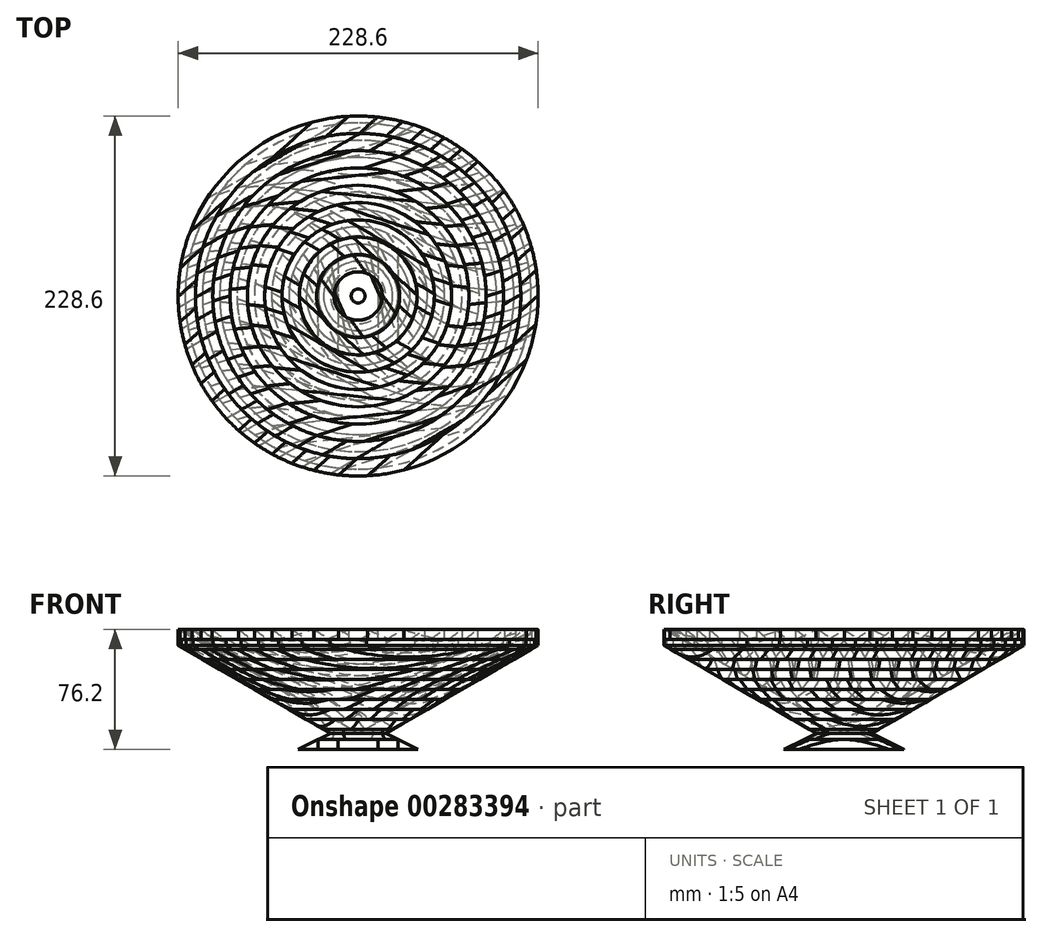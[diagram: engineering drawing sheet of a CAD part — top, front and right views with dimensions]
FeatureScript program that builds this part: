
annotation { "Feature Type Name" : "Feature", "Feature Type Description" : "" }
export const myFeature = defineFeature(function(context is Context, id is Id, definition is map)
    precondition{}
    {
        {
            var Q0;
            Q0=qCreatedBy(makeId("Top.planeOp"),FACE);
            var sketch = newSketch(context, id + "F0", { "sketchPlane" : qUnion([Q0])});
            skLineSegment(sketch, "E0.bottom", {"start": v(114.3, -114.3) * mm, "end": v(-114.3, -114.3) * mm});
            skLineSegment(sketch, "E0.top", {"start": v(114.3, 114.3) * mm, "end": v(-114.3, 114.3) * mm});
            skLineSegment(sketch, "E0.left", {"start": v(114.3, -114.3) * mm, "end": v(114.3, 114.3) * mm});
            skLineSegment(sketch, "E0.right", {"start": v(-114.3, -114.3) * mm, "end": v(-114.3, 114.3) * mm});
            skPoint(sketch, "E0.middle", {"position": v(0, 0) * mm});
            skLineSegment(sketch, "E1.bottom", {"start": v(-12.7, 114.3) * mm, "end": v(12.7, 114.3) * mm});
            skLineSegment(sketch, "E1.top", {"start": v(-12.7, -114.3) * mm, "end": v(12.7, -114.3) * mm});
            skLineSegment(sketch, "E1.left", {"start": v(-12.7, 114.3) * mm, "end": v(-12.7, -114.3) * mm});
            skLineSegment(sketch, "E1.right", {"start": v(12.7, 114.3) * mm, "end": v(12.7, -114.3) * mm});
            skLineSegment(sketch, "E2.bottom", {"start": v(-25.4, 114.3) * mm, "end": v(25.4, 114.3) * mm});
            skLineSegment(sketch, "E2.top", {"start": v(-25.4, -114.3) * mm, "end": v(25.4, -114.3) * mm});
            skLineSegment(sketch, "E2.left", {"start": v(-25.4, 114.3) * mm, "end": v(-25.4, -114.3) * mm});
            skLineSegment(sketch, "E2.right", {"start": v(25.4, 114.3) * mm, "end": v(25.4, -114.3) * mm});
            skLineSegment(sketch, "E3.bottom", {"start": v(-38.1, 114.3) * mm, "end": v(38.1, 114.3) * mm});
            skLineSegment(sketch, "E3.top", {"start": v(-38.1, -114.3) * mm, "end": v(38.1, -114.3) * mm});
            skLineSegment(sketch, "E3.left", {"start": v(-38.1, 114.3) * mm, "end": v(-38.1, -114.3) * mm});
            skLineSegment(sketch, "E3.right", {"start": v(38.1, 114.3) * mm, "end": v(38.1, -114.3) * mm});
            skLineSegment(sketch, "E4.bottom", {"start": v(-50.8, 114.3) * mm, "end": v(50.8, 114.3) * mm});
            skLineSegment(sketch, "E4.top", {"start": v(-50.8, -114.3) * mm, "end": v(50.8, -114.3) * mm});
            skLineSegment(sketch, "E4.left", {"start": v(-50.8, 114.3) * mm, "end": v(-50.8, -114.3) * mm});
            skLineSegment(sketch, "E4.right", {"start": v(50.8, 114.3) * mm, "end": v(50.8, -114.3) * mm});
            skLineSegment(sketch, "E5.bottom", {"start": v(-63.5, 114.3) * mm, "end": v(63.5, 114.3) * mm});
            skLineSegment(sketch, "E5.top", {"start": v(-63.5, -114.3) * mm, "end": v(63.5, -114.3) * mm});
            skLineSegment(sketch, "E5.left", {"start": v(-63.5, 114.3) * mm, "end": v(-63.5, -114.3) * mm});
            skLineSegment(sketch, "E5.right", {"start": v(63.5, 114.3) * mm, "end": v(63.5, -114.3) * mm});
            skLineSegment(sketch, "E6.bottom", {"start": v(-76.2, 114.3) * mm, "end": v(76.2, 114.3) * mm});
            skLineSegment(sketch, "E6.top", {"start": v(-76.2, -114.3) * mm, "end": v(76.2, -114.3) * mm});
            skLineSegment(sketch, "E6.left", {"start": v(-76.2, 114.3) * mm, "end": v(-76.2, -114.3) * mm});
            skLineSegment(sketch, "E6.right", {"start": v(76.2, 114.3) * mm, "end": v(76.2, -114.3) * mm});
            skLineSegment(sketch, "E7.bottom", {"start": v(-88.9, 114.3) * mm, "end": v(88.9, 114.3) * mm});
            skLineSegment(sketch, "E7.top", {"start": v(-88.9, -114.3) * mm, "end": v(88.9, -114.3) * mm});
            skLineSegment(sketch, "E7.left", {"start": v(-88.9, 114.3) * mm, "end": v(-88.9, -114.3) * mm});
            skLineSegment(sketch, "E7.right", {"start": v(88.9, 114.3) * mm, "end": v(88.9, -114.3) * mm});
            skLineSegment(sketch, "E8.bottom", {"start": v(-101.6, 114.3) * mm, "end": v(101.6, 114.3) * mm});
            skLineSegment(sketch, "E8.top", {"start": v(-101.6, -114.3) * mm, "end": v(101.6, -114.3) * mm});
            skLineSegment(sketch, "E8.left", {"start": v(-101.6, 114.3) * mm, "end": v(-101.6, -114.3) * mm});
            skLineSegment(sketch, "E8.right", {"start": v(101.6, 114.3) * mm, "end": v(101.6, -114.3) * mm});
            skSolve(sketch);
        }
        {
            var Q0;
            {var subQ0=sQuery(id+"F0.wireOp",EDGE,"E0.right");Q0=makeQuery(id+"F0.imprint","IMPRINT",FACE,{"disambiguationData":[TD([[makeQuery(id+"F0.imprint","IMPRINT",EDGE,{"derivedFrom":subQ0}),-1.0]])]});}
            var Q1;
            {var subQ0=sQuery(id+"F0.wireOp",EDGE,"E6.left");Q1=makeQuery(id+"F0.imprint","IMPRINT",FACE,{"disambiguationData":[TD([[makeQuery(id+"F0.imprint","IMPRINT",EDGE,{"derivedFrom":subQ0}),-1.0]])]});}
            var Q2;
            {var subQ0=sQuery(id+"F0.wireOp",EDGE,"E4.left");Q2=makeQuery(id+"F0.imprint","IMPRINT",FACE,{"disambiguationData":[TD([[makeQuery(id+"F0.imprint","IMPRINT",EDGE,{"derivedFrom":subQ0}),-1.0]])]});}
            var Q3;
            {var subQ0=sQuery(id+"F0.wireOp",EDGE,"E2.left");Q3=makeQuery(id+"F0.imprint","IMPRINT",FACE,{"disambiguationData":[TD([[makeQuery(id+"F0.imprint","IMPRINT",EDGE,{"derivedFrom":subQ0}),-1.0]])]});}
            var Q4;
            {var subQ0=sQuery(id+"F0.wireOp",EDGE,"E1.left");Q4=makeQuery(id+"F0.imprint","IMPRINT",FACE,{"disambiguationData":[TD([[makeQuery(id+"F0.imprint","IMPRINT",EDGE,{"derivedFrom":subQ0}),1.0]])]});}
            var Q5;
            {var subQ0=sQuery(id+"F0.wireOp",EDGE,"E2.right");Q5=makeQuery(id+"F0.imprint","IMPRINT",FACE,{"disambiguationData":[TD([[makeQuery(id+"F0.imprint","IMPRINT",EDGE,{"derivedFrom":subQ0}),1.0]])]});}
            var Q6;
            {var subQ0=sQuery(id+"F0.wireOp",EDGE,"E4.right");Q6=makeQuery(id+"F0.imprint","IMPRINT",FACE,{"disambiguationData":[TD([[makeQuery(id+"F0.imprint","IMPRINT",EDGE,{"derivedFrom":subQ0}),1.0]])]});}
            var Q7;
            {var subQ0=sQuery(id+"F0.wireOp",EDGE,"E6.right");Q7=makeQuery(id+"F0.imprint","IMPRINT",FACE,{"disambiguationData":[TD([[makeQuery(id+"F0.imprint","IMPRINT",EDGE,{"derivedFrom":subQ0}),1.0]])]});}
            var Q8;
            {var subQ0=sQuery(id+"F0.wireOp",EDGE,"E0.left");Q8=makeQuery(id+"F0.imprint","IMPRINT",FACE,{"disambiguationData":[TD([[makeQuery(id+"F0.imprint","IMPRINT",EDGE,{"derivedFrom":subQ0}),1.0]])]});}
            extrude(context, id + "F1", {"entities" : qUnion([Q0, Q1, Q2, Q3, Q4, Q5, Q6, Q7, Q8]), "depth" : 6.35 * mm});
        }
        {
            var Q0;
            {var subQ0=sQuery(id+"F0.wireOp",EDGE,"E7.right");Q0=makeQuery(id+"F0.imprint","IMPRINT",FACE,{"disambiguationData":[TD([[makeQuery(id+"F0.imprint","IMPRINT",EDGE,{"derivedFrom":subQ0}),1.0]])]});}
            var Q1;
            {var subQ0=sQuery(id+"F0.wireOp",EDGE,"E5.right");Q1=makeQuery(id+"F0.imprint","IMPRINT",FACE,{"disambiguationData":[TD([[makeQuery(id+"F0.imprint","IMPRINT",EDGE,{"derivedFrom":subQ0}),1.0]])]});}
            var Q2;
            {var subQ0=sQuery(id+"F0.wireOp",EDGE,"E3.right");Q2=makeQuery(id+"F0.imprint","IMPRINT",FACE,{"disambiguationData":[TD([[makeQuery(id+"F0.imprint","IMPRINT",EDGE,{"derivedFrom":subQ0}),1.0]])]});}
            var Q3;
            {var subQ0=sQuery(id+"F0.wireOp",EDGE,"E1.right");Q3=makeQuery(id+"F0.imprint","IMPRINT",FACE,{"disambiguationData":[TD([[makeQuery(id+"F0.imprint","IMPRINT",EDGE,{"derivedFrom":subQ0}),1.0]])]});}
            var Q4;
            {var subQ0=sQuery(id+"F0.wireOp",EDGE,"E1.left");Q4=makeQuery(id+"F0.imprint","IMPRINT",FACE,{"disambiguationData":[TD([[makeQuery(id+"F0.imprint","IMPRINT",EDGE,{"derivedFrom":subQ0}),-1.0]])]});}
            var Q5;
            {var subQ0=sQuery(id+"F0.wireOp",EDGE,"E3.left");Q5=makeQuery(id+"F0.imprint","IMPRINT",FACE,{"disambiguationData":[TD([[makeQuery(id+"F0.imprint","IMPRINT",EDGE,{"derivedFrom":subQ0}),-1.0]])]});}
            var Q6;
            {var subQ0=sQuery(id+"F0.wireOp",EDGE,"E5.left");Q6=makeQuery(id+"F0.imprint","IMPRINT",FACE,{"disambiguationData":[TD([[makeQuery(id+"F0.imprint","IMPRINT",EDGE,{"derivedFrom":subQ0}),-1.0]])]});}
            var Q7;
            {var subQ0=sQuery(id+"F0.wireOp",EDGE,"E7.left");Q7=makeQuery(id+"F0.imprint","IMPRINT",FACE,{"disambiguationData":[TD([[makeQuery(id+"F0.imprint","IMPRINT",EDGE,{"derivedFrom":subQ0}),-1.0]])]});}
            extrude(context, id + "F2", {"entities" : qUnion([Q0, Q1, Q2, Q3, Q4, Q5, Q6, Q7]), "depth" : 6.35 * mm});
        }
        {
            var Q0;
            Q0=makeQuery(id+"F2.opExtrude","SWEPT_BODY",BODY,{"disambiguationData":[OSD([sQuery(id+"F0.wireOp",EDGE,"E1.left"),sQuery(id+"F0.wireOp",EDGE,"E2.left"),sQuery(id+"F0.wireOp",EDGE,"E8.bottom"),sQuery(id+"F0.wireOp",EDGE,"E8.top")])]});
            var Q1;
            Q1=makeQuery(id+"F2.opExtrude","SWEPT_BODY",BODY,{"disambiguationData":[OSD([sQuery(id+"F0.wireOp",EDGE,"E1.right"),sQuery(id+"F0.wireOp",EDGE,"E2.right"),sQuery(id+"F0.wireOp",EDGE,"E8.bottom"),sQuery(id+"F0.wireOp",EDGE,"E8.top")])]});
            var Q2;
            Q2=makeQuery(id+"F2.opExtrude","SWEPT_BODY",BODY,{"disambiguationData":[OSD([sQuery(id+"F0.wireOp",EDGE,"E3.right"),sQuery(id+"F0.wireOp",EDGE,"E4.right"),sQuery(id+"F0.wireOp",EDGE,"E8.bottom"),sQuery(id+"F0.wireOp",EDGE,"E8.top")])]});
            var Q3;
            Q3=makeQuery(id+"F2.opExtrude","SWEPT_BODY",BODY,{"disambiguationData":[OSD([sQuery(id+"F0.wireOp",EDGE,"E5.right"),sQuery(id+"F0.wireOp",EDGE,"E6.right"),sQuery(id+"F0.wireOp",EDGE,"E8.bottom"),sQuery(id+"F0.wireOp",EDGE,"E8.top")])]});
            var Q4;
            Q4=makeQuery(id+"F2.opExtrude","SWEPT_BODY",BODY,{"disambiguationData":[OSD([sQuery(id+"F0.wireOp",EDGE,"E3.left"),sQuery(id+"F0.wireOp",EDGE,"E4.left"),sQuery(id+"F0.wireOp",EDGE,"E8.bottom"),sQuery(id+"F0.wireOp",EDGE,"E8.top")])]});
            var Q5;
            Q5=makeQuery(id+"F1.opExtrude","SWEPT_BODY",BODY,{"disambiguationData":[OSD([sQuery(id+"F0.wireOp",EDGE,"E6.right"),sQuery(id+"F0.wireOp",EDGE,"E7.right"),sQuery(id+"F0.wireOp",EDGE,"E8.bottom"),sQuery(id+"F0.wireOp",EDGE,"E8.top")])]});
            var Q6;
            Q6=makeQuery(id+"F1.opExtrude","SWEPT_BODY",BODY,{"disambiguationData":[OSD([sQuery(id+"F0.wireOp",EDGE,"E6.left"),sQuery(id+"F0.wireOp",EDGE,"E7.left"),sQuery(id+"F0.wireOp",EDGE,"E8.bottom"),sQuery(id+"F0.wireOp",EDGE,"E8.top")])]});
            var Q7;
            Q7=makeQuery(id+"F1.opExtrude","SWEPT_BODY",BODY,{"disambiguationData":[OSD([sQuery(id+"F0.wireOp",EDGE,"E4.right"),sQuery(id+"F0.wireOp",EDGE,"E5.right"),sQuery(id+"F0.wireOp",EDGE,"E8.bottom"),sQuery(id+"F0.wireOp",EDGE,"E8.top")])]});
            var Q8;
            Q8=makeQuery(id+"F1.opExtrude","SWEPT_BODY",BODY,{"disambiguationData":[OSD([sQuery(id+"F0.wireOp",EDGE,"E4.left"),sQuery(id+"F0.wireOp",EDGE,"E5.left"),sQuery(id+"F0.wireOp",EDGE,"E8.bottom"),sQuery(id+"F0.wireOp",EDGE,"E8.top")])]});
            var Q9;
            Q9=makeQuery(id+"F1.opExtrude","SWEPT_BODY",BODY,{"disambiguationData":[OSD([sQuery(id+"F0.wireOp",EDGE,"E2.right"),sQuery(id+"F0.wireOp",EDGE,"E3.right"),sQuery(id+"F0.wireOp",EDGE,"E8.bottom"),sQuery(id+"F0.wireOp",EDGE,"E8.top")])]});
            var Q10;
            Q10=makeQuery(id+"F1.opExtrude","SWEPT_BODY",BODY,{"disambiguationData":[OSD([sQuery(id+"F0.wireOp",EDGE,"E2.left"),sQuery(id+"F0.wireOp",EDGE,"E3.left"),sQuery(id+"F0.wireOp",EDGE,"E8.bottom"),sQuery(id+"F0.wireOp",EDGE,"E8.top")])]});
            var Q11;
            Q11=makeQuery(id+"F1.opExtrude","SWEPT_BODY",BODY,{"disambiguationData":[OSD([sQuery(id+"F0.wireOp",EDGE,"E0.bottom"),sQuery(id+"F0.wireOp",EDGE,"E0.top"),sQuery(id+"F0.wireOp",EDGE,"E0.right"),sQuery(id+"F0.wireOp",EDGE,"E8.left")])]});
            var Q12;
            Q12=makeQuery(id+"F1.opExtrude","SWEPT_BODY",BODY,{"disambiguationData":[OSD([sQuery(id+"F0.wireOp",EDGE,"E1.left"),sQuery(id+"F0.wireOp",EDGE,"E1.right"),sQuery(id+"F0.wireOp",EDGE,"E8.bottom"),sQuery(id+"F0.wireOp",EDGE,"E8.top")])]});
            var Q13;
            Q13=makeQuery(id+"F2.opExtrude","SWEPT_BODY",BODY,{"disambiguationData":[OSD([sQuery(id+"F0.wireOp",EDGE,"E5.left"),sQuery(id+"F0.wireOp",EDGE,"E6.left"),sQuery(id+"F0.wireOp",EDGE,"E8.bottom"),sQuery(id+"F0.wireOp",EDGE,"E8.top")])]});
            var Q14;
            Q14=makeQuery(id+"F1.opExtrude","SWEPT_BODY",BODY,{"disambiguationData":[OSD([sQuery(id+"F0.wireOp",EDGE,"E0.bottom"),sQuery(id+"F0.wireOp",EDGE,"E0.top"),sQuery(id+"F0.wireOp",EDGE,"E0.left"),sQuery(id+"F0.wireOp",EDGE,"E8.right")])]});
            var Q15;
            Q15=makeQuery(id+"F2.opExtrude","SWEPT_BODY",BODY,{"disambiguationData":[OSD([sQuery(id+"F0.wireOp",EDGE,"E7.right"),sQuery(id+"F0.wireOp",EDGE,"E8.bottom"),sQuery(id+"F0.wireOp",EDGE,"E8.top"),sQuery(id+"F0.wireOp",EDGE,"E8.right")])]});
            var Q16;
            Q16=makeQuery(id+"F2.opExtrude","SWEPT_BODY",BODY,{"disambiguationData":[OSD([sQuery(id+"F0.wireOp",EDGE,"E7.left"),sQuery(id+"F0.wireOp",EDGE,"E8.bottom"),sQuery(id+"F0.wireOp",EDGE,"E8.top"),sQuery(id+"F0.wireOp",EDGE,"E8.left")])]});
            transform(context, id + "F3", {"entities" : qUnion([Q0, Q1, Q2, Q3, Q4, Q5, Q6, Q7, Q8, Q9, Q10, Q11, Q12, Q13, Q14, Q15, Q16]), "transformType" : TransformType.TRANSLATION_3D, "dx" : 0 * mm, "dy" : 0 * mm, "dz" : 6.35 * mm, "makeCopy" : true});
        }
        {
            var Q0;
            Q0=qCreatedBy(makeId("Front.planeOp"),FACE);
            var sketch = newSketch(context, id + "F4", { "sketchPlane" : qUnion([Q0])});
            skLineSegment(sketch, "E9", {"start": v(0, 0) * mm, "end": v(0, 114.3) * mm, "construction": true});
            skSolve(sketch);
        }
        {
            var Q0;
            Q0=makeQuery(id+"F3.opPattern","COPY",BODY,{"derivedFrom":makeQuery(id+"F1.opExtrude","SWEPT_BODY",BODY,{"disambiguationData":[OSD([sQuery(id+"F0.wireOp",EDGE,"E0.bottom"),sQuery(id+"F0.wireOp",EDGE,"E0.top"),sQuery(id+"F0.wireOp",EDGE,"E0.right"),sQuery(id+"F0.wireOp",EDGE,"E8.left")])]}),"instanceName":"1"});
            var Q1;
            Q1=makeQuery(id+"F3.opPattern","COPY",BODY,{"derivedFrom":makeQuery(id+"F2.opExtrude","SWEPT_BODY",BODY,{"disambiguationData":[OSD([sQuery(id+"F0.wireOp",EDGE,"E7.left"),sQuery(id+"F0.wireOp",EDGE,"E8.bottom"),sQuery(id+"F0.wireOp",EDGE,"E8.top"),sQuery(id+"F0.wireOp",EDGE,"E8.left")])]}),"instanceName":"1"});
            var Q2;
            Q2=makeQuery(id+"F3.opPattern","COPY",BODY,{"derivedFrom":makeQuery(id+"F1.opExtrude","SWEPT_BODY",BODY,{"disambiguationData":[OSD([sQuery(id+"F0.wireOp",EDGE,"E6.left"),sQuery(id+"F0.wireOp",EDGE,"E7.left"),sQuery(id+"F0.wireOp",EDGE,"E8.bottom"),sQuery(id+"F0.wireOp",EDGE,"E8.top")])]}),"instanceName":"1"});
            var Q3;
            Q3=makeQuery(id+"F3.opPattern","COPY",BODY,{"derivedFrom":makeQuery(id+"F1.opExtrude","SWEPT_BODY",BODY,{"disambiguationData":[OSD([sQuery(id+"F0.wireOp",EDGE,"E4.left"),sQuery(id+"F0.wireOp",EDGE,"E5.left"),sQuery(id+"F0.wireOp",EDGE,"E8.bottom"),sQuery(id+"F0.wireOp",EDGE,"E8.top")])]}),"instanceName":"1"});
            var Q4;
            Q4=makeQuery(id+"F3.opPattern","COPY",BODY,{"derivedFrom":makeQuery(id+"F2.opExtrude","SWEPT_BODY",BODY,{"disambiguationData":[OSD([sQuery(id+"F0.wireOp",EDGE,"E5.left"),sQuery(id+"F0.wireOp",EDGE,"E6.left"),sQuery(id+"F0.wireOp",EDGE,"E8.bottom"),sQuery(id+"F0.wireOp",EDGE,"E8.top")])]}),"instanceName":"1"});
            var Q5;
            Q5=makeQuery(id+"F3.opPattern","COPY",BODY,{"derivedFrom":makeQuery(id+"F2.opExtrude","SWEPT_BODY",BODY,{"disambiguationData":[OSD([sQuery(id+"F0.wireOp",EDGE,"E3.left"),sQuery(id+"F0.wireOp",EDGE,"E4.left"),sQuery(id+"F0.wireOp",EDGE,"E8.bottom"),sQuery(id+"F0.wireOp",EDGE,"E8.top")])]}),"instanceName":"1"});
            var Q6;
            Q6=makeQuery(id+"F3.opPattern","COPY",BODY,{"derivedFrom":makeQuery(id+"F1.opExtrude","SWEPT_BODY",BODY,{"disambiguationData":[OSD([sQuery(id+"F0.wireOp",EDGE,"E2.left"),sQuery(id+"F0.wireOp",EDGE,"E3.left"),sQuery(id+"F0.wireOp",EDGE,"E8.bottom"),sQuery(id+"F0.wireOp",EDGE,"E8.top")])]}),"instanceName":"1"});
            var Q7;
            Q7=makeQuery(id+"F3.opPattern","COPY",BODY,{"derivedFrom":makeQuery(id+"F2.opExtrude","SWEPT_BODY",BODY,{"disambiguationData":[OSD([sQuery(id+"F0.wireOp",EDGE,"E1.left"),sQuery(id+"F0.wireOp",EDGE,"E2.left"),sQuery(id+"F0.wireOp",EDGE,"E8.bottom"),sQuery(id+"F0.wireOp",EDGE,"E8.top")])]}),"instanceName":"1"});
            var Q8;
            Q8=makeQuery(id+"F3.opPattern","COPY",BODY,{"derivedFrom":makeQuery(id+"F1.opExtrude","SWEPT_BODY",BODY,{"disambiguationData":[OSD([sQuery(id+"F0.wireOp",EDGE,"E1.left"),sQuery(id+"F0.wireOp",EDGE,"E1.right"),sQuery(id+"F0.wireOp",EDGE,"E8.bottom"),sQuery(id+"F0.wireOp",EDGE,"E8.top")])]}),"instanceName":"1"});
            var Q9;
            Q9=makeQuery(id+"F3.opPattern","COPY",BODY,{"derivedFrom":makeQuery(id+"F2.opExtrude","SWEPT_BODY",BODY,{"disambiguationData":[OSD([sQuery(id+"F0.wireOp",EDGE,"E1.right"),sQuery(id+"F0.wireOp",EDGE,"E2.right"),sQuery(id+"F0.wireOp",EDGE,"E8.bottom"),sQuery(id+"F0.wireOp",EDGE,"E8.top")])]}),"instanceName":"1"});
            var Q10;
            Q10=makeQuery(id+"F3.opPattern","COPY",BODY,{"derivedFrom":makeQuery(id+"F1.opExtrude","SWEPT_BODY",BODY,{"disambiguationData":[OSD([sQuery(id+"F0.wireOp",EDGE,"E2.right"),sQuery(id+"F0.wireOp",EDGE,"E3.right"),sQuery(id+"F0.wireOp",EDGE,"E8.bottom"),sQuery(id+"F0.wireOp",EDGE,"E8.top")])]}),"instanceName":"1"});
            var Q11;
            Q11=makeQuery(id+"F3.opPattern","COPY",BODY,{"derivedFrom":makeQuery(id+"F2.opExtrude","SWEPT_BODY",BODY,{"disambiguationData":[OSD([sQuery(id+"F0.wireOp",EDGE,"E3.right"),sQuery(id+"F0.wireOp",EDGE,"E4.right"),sQuery(id+"F0.wireOp",EDGE,"E8.bottom"),sQuery(id+"F0.wireOp",EDGE,"E8.top")])]}),"instanceName":"1"});
            var Q12;
            Q12=makeQuery(id+"F3.opPattern","COPY",BODY,{"derivedFrom":makeQuery(id+"F1.opExtrude","SWEPT_BODY",BODY,{"disambiguationData":[OSD([sQuery(id+"F0.wireOp",EDGE,"E4.right"),sQuery(id+"F0.wireOp",EDGE,"E5.right"),sQuery(id+"F0.wireOp",EDGE,"E8.bottom"),sQuery(id+"F0.wireOp",EDGE,"E8.top")])]}),"instanceName":"1"});
            var Q13;
            Q13=makeQuery(id+"F3.opPattern","COPY",BODY,{"derivedFrom":makeQuery(id+"F2.opExtrude","SWEPT_BODY",BODY,{"disambiguationData":[OSD([sQuery(id+"F0.wireOp",EDGE,"E5.right"),sQuery(id+"F0.wireOp",EDGE,"E6.right"),sQuery(id+"F0.wireOp",EDGE,"E8.bottom"),sQuery(id+"F0.wireOp",EDGE,"E8.top")])]}),"instanceName":"1"});
            var Q14;
            Q14=makeQuery(id+"F3.opPattern","COPY",BODY,{"derivedFrom":makeQuery(id+"F1.opExtrude","SWEPT_BODY",BODY,{"disambiguationData":[OSD([sQuery(id+"F0.wireOp",EDGE,"E6.right"),sQuery(id+"F0.wireOp",EDGE,"E7.right"),sQuery(id+"F0.wireOp",EDGE,"E8.bottom"),sQuery(id+"F0.wireOp",EDGE,"E8.top")])]}),"instanceName":"1"});
            var Q15;
            Q15=makeQuery(id+"F3.opPattern","COPY",BODY,{"derivedFrom":makeQuery(id+"F2.opExtrude","SWEPT_BODY",BODY,{"disambiguationData":[OSD([sQuery(id+"F0.wireOp",EDGE,"E7.right"),sQuery(id+"F0.wireOp",EDGE,"E8.bottom"),sQuery(id+"F0.wireOp",EDGE,"E8.top"),sQuery(id+"F0.wireOp",EDGE,"E8.right")])]}),"instanceName":"1"});
            var Q16;
            Q16=makeQuery(id+"F3.opPattern","COPY",BODY,{"derivedFrom":makeQuery(id+"F1.opExtrude","SWEPT_BODY",BODY,{"disambiguationData":[OSD([sQuery(id+"F0.wireOp",EDGE,"E0.bottom"),sQuery(id+"F0.wireOp",EDGE,"E0.top"),sQuery(id+"F0.wireOp",EDGE,"E0.left"),sQuery(id+"F0.wireOp",EDGE,"E8.right")])]}),"instanceName":"1"});
            var Q17;
            Q17=sQuery(id+"F4.wireOp",EDGE,"E9");
            transform(context, id + "F5", {"entities" : qUnion([Q0, Q1, Q2, Q3, Q4, Q5, Q6, Q7, Q8, Q9, Q10, Q11, Q12, Q13, Q14, Q15, Q16]), "transformType" : TransformType.ROTATION, "transformAxis" : qUnion([Q17]), "angle" : 12 * degree, "makeCopy" : false});
        }
        {
            var Q0;
            Q0=makeQuery(id+"F3.opPattern","COPY",BODY,{"derivedFrom":makeQuery(id+"F2.opExtrude","SWEPT_BODY",BODY,{"disambiguationData":[OSD([sQuery(id+"F0.wireOp",EDGE,"E1.right"),sQuery(id+"F0.wireOp",EDGE,"E2.right"),sQuery(id+"F0.wireOp",EDGE,"E8.bottom"),sQuery(id+"F0.wireOp",EDGE,"E8.top")])]}),"instanceName":"1"});
            var Q1;
            Q1=makeQuery(id+"F3.opPattern","COPY",BODY,{"derivedFrom":makeQuery(id+"F2.opExtrude","SWEPT_BODY",BODY,{"disambiguationData":[OSD([sQuery(id+"F0.wireOp",EDGE,"E3.left"),sQuery(id+"F0.wireOp",EDGE,"E4.left"),sQuery(id+"F0.wireOp",EDGE,"E8.bottom"),sQuery(id+"F0.wireOp",EDGE,"E8.top")])]}),"instanceName":"1"});
            var Q2;
            Q2=makeQuery(id+"F3.opPattern","COPY",BODY,{"derivedFrom":makeQuery(id+"F2.opExtrude","SWEPT_BODY",BODY,{"disambiguationData":[OSD([sQuery(id+"F0.wireOp",EDGE,"E3.right"),sQuery(id+"F0.wireOp",EDGE,"E4.right"),sQuery(id+"F0.wireOp",EDGE,"E8.bottom"),sQuery(id+"F0.wireOp",EDGE,"E8.top")])]}),"instanceName":"1"});
            var Q3;
            Q3=makeQuery(id+"F3.opPattern","COPY",BODY,{"derivedFrom":makeQuery(id+"F2.opExtrude","SWEPT_BODY",BODY,{"disambiguationData":[OSD([sQuery(id+"F0.wireOp",EDGE,"E5.left"),sQuery(id+"F0.wireOp",EDGE,"E6.left"),sQuery(id+"F0.wireOp",EDGE,"E8.bottom"),sQuery(id+"F0.wireOp",EDGE,"E8.top")])]}),"instanceName":"1"});
            var Q4;
            Q4=makeQuery(id+"F3.opPattern","COPY",BODY,{"derivedFrom":makeQuery(id+"F1.opExtrude","SWEPT_BODY",BODY,{"disambiguationData":[OSD([sQuery(id+"F0.wireOp",EDGE,"E6.right"),sQuery(id+"F0.wireOp",EDGE,"E7.right"),sQuery(id+"F0.wireOp",EDGE,"E8.bottom"),sQuery(id+"F0.wireOp",EDGE,"E8.top")])]}),"instanceName":"1"});
            var Q5;
            Q5=makeQuery(id+"F3.opPattern","COPY",BODY,{"derivedFrom":makeQuery(id+"F2.opExtrude","SWEPT_BODY",BODY,{"disambiguationData":[OSD([sQuery(id+"F0.wireOp",EDGE,"E1.left"),sQuery(id+"F0.wireOp",EDGE,"E2.left"),sQuery(id+"F0.wireOp",EDGE,"E8.bottom"),sQuery(id+"F0.wireOp",EDGE,"E8.top")])]}),"instanceName":"1"});
            var Q6;
            Q6=makeQuery(id+"F3.opPattern","COPY",BODY,{"derivedFrom":makeQuery(id+"F1.opExtrude","SWEPT_BODY",BODY,{"disambiguationData":[OSD([sQuery(id+"F0.wireOp",EDGE,"E4.right"),sQuery(id+"F0.wireOp",EDGE,"E5.right"),sQuery(id+"F0.wireOp",EDGE,"E8.bottom"),sQuery(id+"F0.wireOp",EDGE,"E8.top")])]}),"instanceName":"1"});
            var Q7;
            Q7=makeQuery(id+"F3.opPattern","COPY",BODY,{"derivedFrom":makeQuery(id+"F1.opExtrude","SWEPT_BODY",BODY,{"disambiguationData":[OSD([sQuery(id+"F0.wireOp",EDGE,"E6.left"),sQuery(id+"F0.wireOp",EDGE,"E7.left"),sQuery(id+"F0.wireOp",EDGE,"E8.bottom"),sQuery(id+"F0.wireOp",EDGE,"E8.top")])]}),"instanceName":"1"});
            var Q8;
            Q8=makeQuery(id+"F3.opPattern","COPY",BODY,{"derivedFrom":makeQuery(id+"F1.opExtrude","SWEPT_BODY",BODY,{"disambiguationData":[OSD([sQuery(id+"F0.wireOp",EDGE,"E4.left"),sQuery(id+"F0.wireOp",EDGE,"E5.left"),sQuery(id+"F0.wireOp",EDGE,"E8.bottom"),sQuery(id+"F0.wireOp",EDGE,"E8.top")])]}),"instanceName":"1"});
            var Q9;
            Q9=makeQuery(id+"F3.opPattern","COPY",BODY,{"derivedFrom":makeQuery(id+"F1.opExtrude","SWEPT_BODY",BODY,{"disambiguationData":[OSD([sQuery(id+"F0.wireOp",EDGE,"E2.right"),sQuery(id+"F0.wireOp",EDGE,"E3.right"),sQuery(id+"F0.wireOp",EDGE,"E8.bottom"),sQuery(id+"F0.wireOp",EDGE,"E8.top")])]}),"instanceName":"1"});
            var Q10;
            Q10=makeQuery(id+"F3.opPattern","COPY",BODY,{"derivedFrom":makeQuery(id+"F1.opExtrude","SWEPT_BODY",BODY,{"disambiguationData":[OSD([sQuery(id+"F0.wireOp",EDGE,"E2.left"),sQuery(id+"F0.wireOp",EDGE,"E3.left"),sQuery(id+"F0.wireOp",EDGE,"E8.bottom"),sQuery(id+"F0.wireOp",EDGE,"E8.top")])]}),"instanceName":"1"});
            var Q11;
            Q11=makeQuery(id+"F3.opPattern","COPY",BODY,{"derivedFrom":makeQuery(id+"F1.opExtrude","SWEPT_BODY",BODY,{"disambiguationData":[OSD([sQuery(id+"F0.wireOp",EDGE,"E1.left"),sQuery(id+"F0.wireOp",EDGE,"E1.right"),sQuery(id+"F0.wireOp",EDGE,"E8.bottom"),sQuery(id+"F0.wireOp",EDGE,"E8.top")])]}),"instanceName":"1"});
            var Q12;
            Q12=makeQuery(id+"F3.opPattern","COPY",BODY,{"derivedFrom":makeQuery(id+"F1.opExtrude","SWEPT_BODY",BODY,{"disambiguationData":[OSD([sQuery(id+"F0.wireOp",EDGE,"E0.bottom"),sQuery(id+"F0.wireOp",EDGE,"E0.top"),sQuery(id+"F0.wireOp",EDGE,"E0.right"),sQuery(id+"F0.wireOp",EDGE,"E8.left")])]}),"instanceName":"1"});
            var Q13;
            Q13=makeQuery(id+"F3.opPattern","COPY",BODY,{"derivedFrom":makeQuery(id+"F1.opExtrude","SWEPT_BODY",BODY,{"disambiguationData":[OSD([sQuery(id+"F0.wireOp",EDGE,"E0.bottom"),sQuery(id+"F0.wireOp",EDGE,"E0.top"),sQuery(id+"F0.wireOp",EDGE,"E0.left"),sQuery(id+"F0.wireOp",EDGE,"E8.right")])]}),"instanceName":"1"});
            var Q14;
            Q14=makeQuery(id+"F3.opPattern","COPY",BODY,{"derivedFrom":makeQuery(id+"F2.opExtrude","SWEPT_BODY",BODY,{"disambiguationData":[OSD([sQuery(id+"F0.wireOp",EDGE,"E5.right"),sQuery(id+"F0.wireOp",EDGE,"E6.right"),sQuery(id+"F0.wireOp",EDGE,"E8.bottom"),sQuery(id+"F0.wireOp",EDGE,"E8.top")])]}),"instanceName":"1"});
            var Q15;
            Q15=makeQuery(id+"F3.opPattern","COPY",BODY,{"derivedFrom":makeQuery(id+"F2.opExtrude","SWEPT_BODY",BODY,{"disambiguationData":[OSD([sQuery(id+"F0.wireOp",EDGE,"E7.left"),sQuery(id+"F0.wireOp",EDGE,"E8.bottom"),sQuery(id+"F0.wireOp",EDGE,"E8.top"),sQuery(id+"F0.wireOp",EDGE,"E8.left")])]}),"instanceName":"1"});
            var Q16;
            Q16=makeQuery(id+"F3.opPattern","COPY",BODY,{"derivedFrom":makeQuery(id+"F2.opExtrude","SWEPT_BODY",BODY,{"disambiguationData":[OSD([sQuery(id+"F0.wireOp",EDGE,"E7.right"),sQuery(id+"F0.wireOp",EDGE,"E8.bottom"),sQuery(id+"F0.wireOp",EDGE,"E8.top"),sQuery(id+"F0.wireOp",EDGE,"E8.right")])]}),"instanceName":"1"});
            var Q17;
            Q17=makeQuery(id+"F2.opExtrude","SWEPT_BODY",BODY,{"disambiguationData":[OSD([sQuery(id+"F0.wireOp",EDGE,"E1.left"),sQuery(id+"F0.wireOp",EDGE,"E2.left"),sQuery(id+"F0.wireOp",EDGE,"E8.bottom"),sQuery(id+"F0.wireOp",EDGE,"E8.top")])]});
            var Q18;
            Q18=makeQuery(id+"F2.opExtrude","SWEPT_BODY",BODY,{"disambiguationData":[OSD([sQuery(id+"F0.wireOp",EDGE,"E1.right"),sQuery(id+"F0.wireOp",EDGE,"E2.right"),sQuery(id+"F0.wireOp",EDGE,"E8.bottom"),sQuery(id+"F0.wireOp",EDGE,"E8.top")])]});
            var Q19;
            Q19=makeQuery(id+"F2.opExtrude","SWEPT_BODY",BODY,{"disambiguationData":[OSD([sQuery(id+"F0.wireOp",EDGE,"E3.right"),sQuery(id+"F0.wireOp",EDGE,"E4.right"),sQuery(id+"F0.wireOp",EDGE,"E8.bottom"),sQuery(id+"F0.wireOp",EDGE,"E8.top")])]});
            var Q20;
            Q20=makeQuery(id+"F2.opExtrude","SWEPT_BODY",BODY,{"disambiguationData":[OSD([sQuery(id+"F0.wireOp",EDGE,"E5.right"),sQuery(id+"F0.wireOp",EDGE,"E6.right"),sQuery(id+"F0.wireOp",EDGE,"E8.bottom"),sQuery(id+"F0.wireOp",EDGE,"E8.top")])]});
            var Q21;
            Q21=makeQuery(id+"F2.opExtrude","SWEPT_BODY",BODY,{"disambiguationData":[OSD([sQuery(id+"F0.wireOp",EDGE,"E3.left"),sQuery(id+"F0.wireOp",EDGE,"E4.left"),sQuery(id+"F0.wireOp",EDGE,"E8.bottom"),sQuery(id+"F0.wireOp",EDGE,"E8.top")])]});
            var Q22;
            Q22=makeQuery(id+"F1.opExtrude","SWEPT_BODY",BODY,{"disambiguationData":[OSD([sQuery(id+"F0.wireOp",EDGE,"E6.right"),sQuery(id+"F0.wireOp",EDGE,"E7.right"),sQuery(id+"F0.wireOp",EDGE,"E8.bottom"),sQuery(id+"F0.wireOp",EDGE,"E8.top")])]});
            var Q23;
            Q23=makeQuery(id+"F1.opExtrude","SWEPT_BODY",BODY,{"disambiguationData":[OSD([sQuery(id+"F0.wireOp",EDGE,"E6.left"),sQuery(id+"F0.wireOp",EDGE,"E7.left"),sQuery(id+"F0.wireOp",EDGE,"E8.bottom"),sQuery(id+"F0.wireOp",EDGE,"E8.top")])]});
            var Q24;
            Q24=makeQuery(id+"F1.opExtrude","SWEPT_BODY",BODY,{"disambiguationData":[OSD([sQuery(id+"F0.wireOp",EDGE,"E4.right"),sQuery(id+"F0.wireOp",EDGE,"E5.right"),sQuery(id+"F0.wireOp",EDGE,"E8.bottom"),sQuery(id+"F0.wireOp",EDGE,"E8.top")])]});
            var Q25;
            Q25=makeQuery(id+"F1.opExtrude","SWEPT_BODY",BODY,{"disambiguationData":[OSD([sQuery(id+"F0.wireOp",EDGE,"E4.left"),sQuery(id+"F0.wireOp",EDGE,"E5.left"),sQuery(id+"F0.wireOp",EDGE,"E8.bottom"),sQuery(id+"F0.wireOp",EDGE,"E8.top")])]});
            var Q26;
            Q26=makeQuery(id+"F1.opExtrude","SWEPT_BODY",BODY,{"disambiguationData":[OSD([sQuery(id+"F0.wireOp",EDGE,"E2.right"),sQuery(id+"F0.wireOp",EDGE,"E3.right"),sQuery(id+"F0.wireOp",EDGE,"E8.bottom"),sQuery(id+"F0.wireOp",EDGE,"E8.top")])]});
            var Q27;
            Q27=makeQuery(id+"F1.opExtrude","SWEPT_BODY",BODY,{"disambiguationData":[OSD([sQuery(id+"F0.wireOp",EDGE,"E2.left"),sQuery(id+"F0.wireOp",EDGE,"E3.left"),sQuery(id+"F0.wireOp",EDGE,"E8.bottom"),sQuery(id+"F0.wireOp",EDGE,"E8.top")])]});
            var Q28;
            Q28=makeQuery(id+"F1.opExtrude","SWEPT_BODY",BODY,{"disambiguationData":[OSD([sQuery(id+"F0.wireOp",EDGE,"E0.bottom"),sQuery(id+"F0.wireOp",EDGE,"E0.top"),sQuery(id+"F0.wireOp",EDGE,"E0.right"),sQuery(id+"F0.wireOp",EDGE,"E8.left")])]});
            var Q29;
            Q29=makeQuery(id+"F1.opExtrude","SWEPT_BODY",BODY,{"disambiguationData":[OSD([sQuery(id+"F0.wireOp",EDGE,"E1.left"),sQuery(id+"F0.wireOp",EDGE,"E1.right"),sQuery(id+"F0.wireOp",EDGE,"E8.bottom"),sQuery(id+"F0.wireOp",EDGE,"E8.top")])]});
            var Q30;
            Q30=makeQuery(id+"F2.opExtrude","SWEPT_BODY",BODY,{"disambiguationData":[OSD([sQuery(id+"F0.wireOp",EDGE,"E5.left"),sQuery(id+"F0.wireOp",EDGE,"E6.left"),sQuery(id+"F0.wireOp",EDGE,"E8.bottom"),sQuery(id+"F0.wireOp",EDGE,"E8.top")])]});
            var Q31;
            Q31=makeQuery(id+"F1.opExtrude","SWEPT_BODY",BODY,{"disambiguationData":[OSD([sQuery(id+"F0.wireOp",EDGE,"E0.bottom"),sQuery(id+"F0.wireOp",EDGE,"E0.top"),sQuery(id+"F0.wireOp",EDGE,"E0.left"),sQuery(id+"F0.wireOp",EDGE,"E8.right")])]});
            var Q32;
            Q32=makeQuery(id+"F2.opExtrude","SWEPT_BODY",BODY,{"disambiguationData":[OSD([sQuery(id+"F0.wireOp",EDGE,"E7.right"),sQuery(id+"F0.wireOp",EDGE,"E8.bottom"),sQuery(id+"F0.wireOp",EDGE,"E8.top"),sQuery(id+"F0.wireOp",EDGE,"E8.right")])]});
            var Q33;
            Q33=makeQuery(id+"F2.opExtrude","SWEPT_BODY",BODY,{"disambiguationData":[OSD([sQuery(id+"F0.wireOp",EDGE,"E7.left"),sQuery(id+"F0.wireOp",EDGE,"E8.bottom"),sQuery(id+"F0.wireOp",EDGE,"E8.top"),sQuery(id+"F0.wireOp",EDGE,"E8.left")])]});
            transform(context, id + "F6", {"entities" : qUnion([Q0, Q1, Q2, Q3, Q4, Q5, Q6, Q7, Q8, Q9, Q10, Q11, Q12, Q13, Q14, Q15, Q16, Q17, Q18, Q19, Q20, Q21, Q22, Q23, Q24, Q25, Q26, Q27, Q28, Q29, Q30, Q31, Q32, Q33]), "transformType" : TransformType.TRANSLATION_3D, "dx" : 0 * mm, "dy" : 0 * mm, "dz" : 12.7 * mm, "makeCopy" : true});
        }
        {
            var Q0;
            Q0=makeQuery(id+"F6.opPattern","COPY",BODY,{"derivedFrom":makeQuery(id+"F3.opPattern","COPY",BODY,{"derivedFrom":makeQuery(id+"F2.opExtrude","SWEPT_BODY",BODY,{"disambiguationData":[OSD([sQuery(id+"F0.wireOp",EDGE,"E3.right"),sQuery(id+"F0.wireOp",EDGE,"E4.right"),sQuery(id+"F0.wireOp",EDGE,"E8.bottom"),sQuery(id+"F0.wireOp",EDGE,"E8.top")])]}),"instanceName":"1"}),"instanceName":"1"});
            var Q1;
            Q1=makeQuery(id+"F6.opPattern","COPY",BODY,{"derivedFrom":makeQuery(id+"F1.opExtrude","SWEPT_BODY",BODY,{"disambiguationData":[OSD([sQuery(id+"F0.wireOp",EDGE,"E0.bottom"),sQuery(id+"F0.wireOp",EDGE,"E0.top"),sQuery(id+"F0.wireOp",EDGE,"E0.left"),sQuery(id+"F0.wireOp",EDGE,"E8.right")])]}),"instanceName":"1"});
            var Q2;
            Q2=makeQuery(id+"F6.opPattern","COPY",BODY,{"derivedFrom":makeQuery(id+"F3.opPattern","COPY",BODY,{"derivedFrom":makeQuery(id+"F2.opExtrude","SWEPT_BODY",BODY,{"disambiguationData":[OSD([sQuery(id+"F0.wireOp",EDGE,"E5.right"),sQuery(id+"F0.wireOp",EDGE,"E6.right"),sQuery(id+"F0.wireOp",EDGE,"E8.bottom"),sQuery(id+"F0.wireOp",EDGE,"E8.top")])]}),"instanceName":"1"}),"instanceName":"1"});
            var Q3;
            Q3=makeQuery(id+"F6.opPattern","COPY",BODY,{"derivedFrom":makeQuery(id+"F3.opPattern","COPY",BODY,{"derivedFrom":makeQuery(id+"F2.opExtrude","SWEPT_BODY",BODY,{"disambiguationData":[OSD([sQuery(id+"F0.wireOp",EDGE,"E1.right"),sQuery(id+"F0.wireOp",EDGE,"E2.right"),sQuery(id+"F0.wireOp",EDGE,"E8.bottom"),sQuery(id+"F0.wireOp",EDGE,"E8.top")])]}),"instanceName":"1"}),"instanceName":"1"});
            var Q4;
            Q4=makeQuery(id+"F6.opPattern","COPY",BODY,{"derivedFrom":makeQuery(id+"F3.opPattern","COPY",BODY,{"derivedFrom":makeQuery(id+"F2.opExtrude","SWEPT_BODY",BODY,{"disambiguationData":[OSD([sQuery(id+"F0.wireOp",EDGE,"E1.left"),sQuery(id+"F0.wireOp",EDGE,"E2.left"),sQuery(id+"F0.wireOp",EDGE,"E8.bottom"),sQuery(id+"F0.wireOp",EDGE,"E8.top")])]}),"instanceName":"1"}),"instanceName":"1"});
            var Q5;
            Q5=makeQuery(id+"F6.opPattern","COPY",BODY,{"derivedFrom":makeQuery(id+"F3.opPattern","COPY",BODY,{"derivedFrom":makeQuery(id+"F1.opExtrude","SWEPT_BODY",BODY,{"disambiguationData":[OSD([sQuery(id+"F0.wireOp",EDGE,"E6.left"),sQuery(id+"F0.wireOp",EDGE,"E7.left"),sQuery(id+"F0.wireOp",EDGE,"E8.bottom"),sQuery(id+"F0.wireOp",EDGE,"E8.top")])]}),"instanceName":"1"}),"instanceName":"1"});
            var Q6;
            Q6=makeQuery(id+"F6.opPattern","COPY",BODY,{"derivedFrom":makeQuery(id+"F3.opPattern","COPY",BODY,{"derivedFrom":makeQuery(id+"F1.opExtrude","SWEPT_BODY",BODY,{"disambiguationData":[OSD([sQuery(id+"F0.wireOp",EDGE,"E6.right"),sQuery(id+"F0.wireOp",EDGE,"E7.right"),sQuery(id+"F0.wireOp",EDGE,"E8.bottom"),sQuery(id+"F0.wireOp",EDGE,"E8.top")])]}),"instanceName":"1"}),"instanceName":"1"});
            var Q7;
            Q7=makeQuery(id+"F6.opPattern","COPY",BODY,{"derivedFrom":makeQuery(id+"F3.opPattern","COPY",BODY,{"derivedFrom":makeQuery(id+"F1.opExtrude","SWEPT_BODY",BODY,{"disambiguationData":[OSD([sQuery(id+"F0.wireOp",EDGE,"E4.right"),sQuery(id+"F0.wireOp",EDGE,"E5.right"),sQuery(id+"F0.wireOp",EDGE,"E8.bottom"),sQuery(id+"F0.wireOp",EDGE,"E8.top")])]}),"instanceName":"1"}),"instanceName":"1"});
            var Q8;
            Q8=makeQuery(id+"F6.opPattern","COPY",BODY,{"derivedFrom":makeQuery(id+"F3.opPattern","COPY",BODY,{"derivedFrom":makeQuery(id+"F1.opExtrude","SWEPT_BODY",BODY,{"disambiguationData":[OSD([sQuery(id+"F0.wireOp",EDGE,"E4.left"),sQuery(id+"F0.wireOp",EDGE,"E5.left"),sQuery(id+"F0.wireOp",EDGE,"E8.bottom"),sQuery(id+"F0.wireOp",EDGE,"E8.top")])]}),"instanceName":"1"}),"instanceName":"1"});
            var Q9;
            Q9=makeQuery(id+"F6.opPattern","COPY",BODY,{"derivedFrom":makeQuery(id+"F3.opPattern","COPY",BODY,{"derivedFrom":makeQuery(id+"F1.opExtrude","SWEPT_BODY",BODY,{"disambiguationData":[OSD([sQuery(id+"F0.wireOp",EDGE,"E2.right"),sQuery(id+"F0.wireOp",EDGE,"E3.right"),sQuery(id+"F0.wireOp",EDGE,"E8.bottom"),sQuery(id+"F0.wireOp",EDGE,"E8.top")])]}),"instanceName":"1"}),"instanceName":"1"});
            var Q10;
            Q10=makeQuery(id+"F6.opPattern","COPY",BODY,{"derivedFrom":makeQuery(id+"F3.opPattern","COPY",BODY,{"derivedFrom":makeQuery(id+"F1.opExtrude","SWEPT_BODY",BODY,{"disambiguationData":[OSD([sQuery(id+"F0.wireOp",EDGE,"E2.left"),sQuery(id+"F0.wireOp",EDGE,"E3.left"),sQuery(id+"F0.wireOp",EDGE,"E8.bottom"),sQuery(id+"F0.wireOp",EDGE,"E8.top")])]}),"instanceName":"1"}),"instanceName":"1"});
            var Q11;
            Q11=makeQuery(id+"F6.opPattern","COPY",BODY,{"derivedFrom":makeQuery(id+"F3.opPattern","COPY",BODY,{"derivedFrom":makeQuery(id+"F1.opExtrude","SWEPT_BODY",BODY,{"disambiguationData":[OSD([sQuery(id+"F0.wireOp",EDGE,"E1.left"),sQuery(id+"F0.wireOp",EDGE,"E1.right"),sQuery(id+"F0.wireOp",EDGE,"E8.bottom"),sQuery(id+"F0.wireOp",EDGE,"E8.top")])]}),"instanceName":"1"}),"instanceName":"1"});
            var Q12;
            Q12=makeQuery(id+"F6.opPattern","COPY",BODY,{"derivedFrom":makeQuery(id+"F3.opPattern","COPY",BODY,{"derivedFrom":makeQuery(id+"F1.opExtrude","SWEPT_BODY",BODY,{"disambiguationData":[OSD([sQuery(id+"F0.wireOp",EDGE,"E0.bottom"),sQuery(id+"F0.wireOp",EDGE,"E0.top"),sQuery(id+"F0.wireOp",EDGE,"E0.right"),sQuery(id+"F0.wireOp",EDGE,"E8.left")])]}),"instanceName":"1"}),"instanceName":"1"});
            var Q13;
            Q13=makeQuery(id+"F6.opPattern","COPY",BODY,{"derivedFrom":makeQuery(id+"F3.opPattern","COPY",BODY,{"derivedFrom":makeQuery(id+"F1.opExtrude","SWEPT_BODY",BODY,{"disambiguationData":[OSD([sQuery(id+"F0.wireOp",EDGE,"E0.bottom"),sQuery(id+"F0.wireOp",EDGE,"E0.top"),sQuery(id+"F0.wireOp",EDGE,"E0.left"),sQuery(id+"F0.wireOp",EDGE,"E8.right")])]}),"instanceName":"1"}),"instanceName":"1"});
            var Q14;
            Q14=makeQuery(id+"F6.opPattern","COPY",BODY,{"derivedFrom":makeQuery(id+"F2.opExtrude","SWEPT_BODY",BODY,{"disambiguationData":[OSD([sQuery(id+"F0.wireOp",EDGE,"E7.right"),sQuery(id+"F0.wireOp",EDGE,"E8.bottom"),sQuery(id+"F0.wireOp",EDGE,"E8.top"),sQuery(id+"F0.wireOp",EDGE,"E8.right")])]}),"instanceName":"1"});
            var Q15;
            Q15=makeQuery(id+"F6.opPattern","COPY",BODY,{"derivedFrom":makeQuery(id+"F2.opExtrude","SWEPT_BODY",BODY,{"disambiguationData":[OSD([sQuery(id+"F0.wireOp",EDGE,"E7.left"),sQuery(id+"F0.wireOp",EDGE,"E8.bottom"),sQuery(id+"F0.wireOp",EDGE,"E8.top"),sQuery(id+"F0.wireOp",EDGE,"E8.left")])]}),"instanceName":"1"});
            var Q16;
            Q16=makeQuery(id+"F6.opPattern","COPY",BODY,{"derivedFrom":makeQuery(id+"F2.opExtrude","SWEPT_BODY",BODY,{"disambiguationData":[OSD([sQuery(id+"F0.wireOp",EDGE,"E5.right"),sQuery(id+"F0.wireOp",EDGE,"E6.right"),sQuery(id+"F0.wireOp",EDGE,"E8.bottom"),sQuery(id+"F0.wireOp",EDGE,"E8.top")])]}),"instanceName":"1"});
            var Q17;
            Q17=makeQuery(id+"F6.opPattern","COPY",BODY,{"derivedFrom":makeQuery(id+"F2.opExtrude","SWEPT_BODY",BODY,{"disambiguationData":[OSD([sQuery(id+"F0.wireOp",EDGE,"E5.left"),sQuery(id+"F0.wireOp",EDGE,"E6.left"),sQuery(id+"F0.wireOp",EDGE,"E8.bottom"),sQuery(id+"F0.wireOp",EDGE,"E8.top")])]}),"instanceName":"1"});
            var Q18;
            Q18=makeQuery(id+"F6.opPattern","COPY",BODY,{"derivedFrom":makeQuery(id+"F2.opExtrude","SWEPT_BODY",BODY,{"disambiguationData":[OSD([sQuery(id+"F0.wireOp",EDGE,"E3.left"),sQuery(id+"F0.wireOp",EDGE,"E4.left"),sQuery(id+"F0.wireOp",EDGE,"E8.bottom"),sQuery(id+"F0.wireOp",EDGE,"E8.top")])]}),"instanceName":"1"});
            var Q19;
            Q19=makeQuery(id+"F6.opPattern","COPY",BODY,{"derivedFrom":makeQuery(id+"F2.opExtrude","SWEPT_BODY",BODY,{"disambiguationData":[OSD([sQuery(id+"F0.wireOp",EDGE,"E3.right"),sQuery(id+"F0.wireOp",EDGE,"E4.right"),sQuery(id+"F0.wireOp",EDGE,"E8.bottom"),sQuery(id+"F0.wireOp",EDGE,"E8.top")])]}),"instanceName":"1"});
            var Q20;
            Q20=makeQuery(id+"F6.opPattern","COPY",BODY,{"derivedFrom":makeQuery(id+"F2.opExtrude","SWEPT_BODY",BODY,{"disambiguationData":[OSD([sQuery(id+"F0.wireOp",EDGE,"E1.right"),sQuery(id+"F0.wireOp",EDGE,"E2.right"),sQuery(id+"F0.wireOp",EDGE,"E8.bottom"),sQuery(id+"F0.wireOp",EDGE,"E8.top")])]}),"instanceName":"1"});
            var Q21;
            Q21=makeQuery(id+"F6.opPattern","COPY",BODY,{"derivedFrom":makeQuery(id+"F2.opExtrude","SWEPT_BODY",BODY,{"disambiguationData":[OSD([sQuery(id+"F0.wireOp",EDGE,"E1.left"),sQuery(id+"F0.wireOp",EDGE,"E2.left"),sQuery(id+"F0.wireOp",EDGE,"E8.bottom"),sQuery(id+"F0.wireOp",EDGE,"E8.top")])]}),"instanceName":"1"});
            var Q22;
            Q22=makeQuery(id+"F6.opPattern","COPY",BODY,{"derivedFrom":makeQuery(id+"F1.opExtrude","SWEPT_BODY",BODY,{"disambiguationData":[OSD([sQuery(id+"F0.wireOp",EDGE,"E6.right"),sQuery(id+"F0.wireOp",EDGE,"E7.right"),sQuery(id+"F0.wireOp",EDGE,"E8.bottom"),sQuery(id+"F0.wireOp",EDGE,"E8.top")])]}),"instanceName":"1"});
            var Q23;
            Q23=makeQuery(id+"F6.opPattern","COPY",BODY,{"derivedFrom":makeQuery(id+"F1.opExtrude","SWEPT_BODY",BODY,{"disambiguationData":[OSD([sQuery(id+"F0.wireOp",EDGE,"E6.left"),sQuery(id+"F0.wireOp",EDGE,"E7.left"),sQuery(id+"F0.wireOp",EDGE,"E8.bottom"),sQuery(id+"F0.wireOp",EDGE,"E8.top")])]}),"instanceName":"1"});
            var Q24;
            Q24=makeQuery(id+"F6.opPattern","COPY",BODY,{"derivedFrom":makeQuery(id+"F1.opExtrude","SWEPT_BODY",BODY,{"disambiguationData":[OSD([sQuery(id+"F0.wireOp",EDGE,"E4.right"),sQuery(id+"F0.wireOp",EDGE,"E5.right"),sQuery(id+"F0.wireOp",EDGE,"E8.bottom"),sQuery(id+"F0.wireOp",EDGE,"E8.top")])]}),"instanceName":"1"});
            var Q25;
            Q25=makeQuery(id+"F6.opPattern","COPY",BODY,{"derivedFrom":makeQuery(id+"F1.opExtrude","SWEPT_BODY",BODY,{"disambiguationData":[OSD([sQuery(id+"F0.wireOp",EDGE,"E4.left"),sQuery(id+"F0.wireOp",EDGE,"E5.left"),sQuery(id+"F0.wireOp",EDGE,"E8.bottom"),sQuery(id+"F0.wireOp",EDGE,"E8.top")])]}),"instanceName":"1"});
            var Q26;
            Q26=makeQuery(id+"F6.opPattern","COPY",BODY,{"derivedFrom":makeQuery(id+"F1.opExtrude","SWEPT_BODY",BODY,{"disambiguationData":[OSD([sQuery(id+"F0.wireOp",EDGE,"E2.right"),sQuery(id+"F0.wireOp",EDGE,"E3.right"),sQuery(id+"F0.wireOp",EDGE,"E8.bottom"),sQuery(id+"F0.wireOp",EDGE,"E8.top")])]}),"instanceName":"1"});
            var Q27;
            Q27=makeQuery(id+"F6.opPattern","COPY",BODY,{"derivedFrom":makeQuery(id+"F1.opExtrude","SWEPT_BODY",BODY,{"disambiguationData":[OSD([sQuery(id+"F0.wireOp",EDGE,"E2.left"),sQuery(id+"F0.wireOp",EDGE,"E3.left"),sQuery(id+"F0.wireOp",EDGE,"E8.bottom"),sQuery(id+"F0.wireOp",EDGE,"E8.top")])]}),"instanceName":"1"});
            var Q28;
            Q28=makeQuery(id+"F6.opPattern","COPY",BODY,{"derivedFrom":makeQuery(id+"F1.opExtrude","SWEPT_BODY",BODY,{"disambiguationData":[OSD([sQuery(id+"F0.wireOp",EDGE,"E1.left"),sQuery(id+"F0.wireOp",EDGE,"E1.right"),sQuery(id+"F0.wireOp",EDGE,"E8.bottom"),sQuery(id+"F0.wireOp",EDGE,"E8.top")])]}),"instanceName":"1"});
            var Q29;
            Q29=makeQuery(id+"F6.opPattern","COPY",BODY,{"derivedFrom":makeQuery(id+"F1.opExtrude","SWEPT_BODY",BODY,{"disambiguationData":[OSD([sQuery(id+"F0.wireOp",EDGE,"E0.bottom"),sQuery(id+"F0.wireOp",EDGE,"E0.top"),sQuery(id+"F0.wireOp",EDGE,"E0.right"),sQuery(id+"F0.wireOp",EDGE,"E8.left")])]}),"instanceName":"1"});
            var Q30;
            Q30=makeQuery(id+"F6.opPattern","COPY",BODY,{"derivedFrom":makeQuery(id+"F3.opPattern","COPY",BODY,{"derivedFrom":makeQuery(id+"F2.opExtrude","SWEPT_BODY",BODY,{"disambiguationData":[OSD([sQuery(id+"F0.wireOp",EDGE,"E5.left"),sQuery(id+"F0.wireOp",EDGE,"E6.left"),sQuery(id+"F0.wireOp",EDGE,"E8.bottom"),sQuery(id+"F0.wireOp",EDGE,"E8.top")])]}),"instanceName":"1"}),"instanceName":"1"});
            var Q31;
            Q31=makeQuery(id+"F6.opPattern","COPY",BODY,{"derivedFrom":makeQuery(id+"F3.opPattern","COPY",BODY,{"derivedFrom":makeQuery(id+"F2.opExtrude","SWEPT_BODY",BODY,{"disambiguationData":[OSD([sQuery(id+"F0.wireOp",EDGE,"E7.left"),sQuery(id+"F0.wireOp",EDGE,"E8.bottom"),sQuery(id+"F0.wireOp",EDGE,"E8.top"),sQuery(id+"F0.wireOp",EDGE,"E8.left")])]}),"instanceName":"1"}),"instanceName":"1"});
            var Q32;
            Q32=makeQuery(id+"F6.opPattern","COPY",BODY,{"derivedFrom":makeQuery(id+"F3.opPattern","COPY",BODY,{"derivedFrom":makeQuery(id+"F2.opExtrude","SWEPT_BODY",BODY,{"disambiguationData":[OSD([sQuery(id+"F0.wireOp",EDGE,"E3.left"),sQuery(id+"F0.wireOp",EDGE,"E4.left"),sQuery(id+"F0.wireOp",EDGE,"E8.bottom"),sQuery(id+"F0.wireOp",EDGE,"E8.top")])]}),"instanceName":"1"}),"instanceName":"1"});
            var Q33;
            Q33=makeQuery(id+"F6.opPattern","COPY",BODY,{"derivedFrom":makeQuery(id+"F3.opPattern","COPY",BODY,{"derivedFrom":makeQuery(id+"F2.opExtrude","SWEPT_BODY",BODY,{"disambiguationData":[OSD([sQuery(id+"F0.wireOp",EDGE,"E7.right"),sQuery(id+"F0.wireOp",EDGE,"E8.bottom"),sQuery(id+"F0.wireOp",EDGE,"E8.top"),sQuery(id+"F0.wireOp",EDGE,"E8.right")])]}),"instanceName":"1"}),"instanceName":"1"});
            var Q34;
            Q34=sQuery(id+"F4.wireOp",EDGE,"E9");
            transform(context, id + "F7", {"entities" : qUnion([Q0, Q1, Q2, Q3, Q4, Q5, Q6, Q7, Q8, Q9, Q10, Q11, Q12, Q13, Q14, Q15, Q16, Q17, Q18, Q19, Q20, Q21, Q22, Q23, Q24, Q25, Q26, Q27, Q28, Q29, Q30, Q31, Q32, Q33]), "transformType" : TransformType.ROTATION, "transformAxis" : qUnion([Q34]), "angle" : 24 * degree, "makeCopy" : false});
        }
        {
            var Q0;
            Q0=makeQuery(id+"F3.opPattern","COPY",BODY,{"derivedFrom":makeQuery(id+"F2.opExtrude","SWEPT_BODY",BODY,{"disambiguationData":[OSD([sQuery(id+"F0.wireOp",EDGE,"E1.right"),sQuery(id+"F0.wireOp",EDGE,"E2.right"),sQuery(id+"F0.wireOp",EDGE,"E8.bottom"),sQuery(id+"F0.wireOp",EDGE,"E8.top")])]}),"instanceName":"1"});
            var Q1;
            Q1=makeQuery(id+"F3.opPattern","COPY",BODY,{"derivedFrom":makeQuery(id+"F2.opExtrude","SWEPT_BODY",BODY,{"disambiguationData":[OSD([sQuery(id+"F0.wireOp",EDGE,"E3.left"),sQuery(id+"F0.wireOp",EDGE,"E4.left"),sQuery(id+"F0.wireOp",EDGE,"E8.bottom"),sQuery(id+"F0.wireOp",EDGE,"E8.top")])]}),"instanceName":"1"});
            var Q2;
            Q2=makeQuery(id+"F3.opPattern","COPY",BODY,{"derivedFrom":makeQuery(id+"F2.opExtrude","SWEPT_BODY",BODY,{"disambiguationData":[OSD([sQuery(id+"F0.wireOp",EDGE,"E3.right"),sQuery(id+"F0.wireOp",EDGE,"E4.right"),sQuery(id+"F0.wireOp",EDGE,"E8.bottom"),sQuery(id+"F0.wireOp",EDGE,"E8.top")])]}),"instanceName":"1"});
            var Q3;
            Q3=makeQuery(id+"F3.opPattern","COPY",BODY,{"derivedFrom":makeQuery(id+"F2.opExtrude","SWEPT_BODY",BODY,{"disambiguationData":[OSD([sQuery(id+"F0.wireOp",EDGE,"E5.left"),sQuery(id+"F0.wireOp",EDGE,"E6.left"),sQuery(id+"F0.wireOp",EDGE,"E8.bottom"),sQuery(id+"F0.wireOp",EDGE,"E8.top")])]}),"instanceName":"1"});
            var Q4;
            Q4=makeQuery(id+"F6.opPattern","COPY",BODY,{"derivedFrom":makeQuery(id+"F1.opExtrude","SWEPT_BODY",BODY,{"disambiguationData":[OSD([sQuery(id+"F0.wireOp",EDGE,"E0.bottom"),sQuery(id+"F0.wireOp",EDGE,"E0.top"),sQuery(id+"F0.wireOp",EDGE,"E0.right"),sQuery(id+"F0.wireOp",EDGE,"E8.left")])]}),"instanceName":"1"});
            var Q5;
            Q5=makeQuery(id+"F6.opPattern","COPY",BODY,{"derivedFrom":makeQuery(id+"F3.opPattern","COPY",BODY,{"derivedFrom":makeQuery(id+"F2.opExtrude","SWEPT_BODY",BODY,{"disambiguationData":[OSD([sQuery(id+"F0.wireOp",EDGE,"E5.left"),sQuery(id+"F0.wireOp",EDGE,"E6.left"),sQuery(id+"F0.wireOp",EDGE,"E8.bottom"),sQuery(id+"F0.wireOp",EDGE,"E8.top")])]}),"instanceName":"1"}),"instanceName":"1"});
            var Q6;
            Q6=makeQuery(id+"F6.opPattern","COPY",BODY,{"derivedFrom":makeQuery(id+"F3.opPattern","COPY",BODY,{"derivedFrom":makeQuery(id+"F2.opExtrude","SWEPT_BODY",BODY,{"disambiguationData":[OSD([sQuery(id+"F0.wireOp",EDGE,"E7.left"),sQuery(id+"F0.wireOp",EDGE,"E8.bottom"),sQuery(id+"F0.wireOp",EDGE,"E8.top"),sQuery(id+"F0.wireOp",EDGE,"E8.left")])]}),"instanceName":"1"}),"instanceName":"1"});
            var Q7;
            Q7=makeQuery(id+"F6.opPattern","COPY",BODY,{"derivedFrom":makeQuery(id+"F3.opPattern","COPY",BODY,{"derivedFrom":makeQuery(id+"F2.opExtrude","SWEPT_BODY",BODY,{"disambiguationData":[OSD([sQuery(id+"F0.wireOp",EDGE,"E5.right"),sQuery(id+"F0.wireOp",EDGE,"E6.right"),sQuery(id+"F0.wireOp",EDGE,"E8.bottom"),sQuery(id+"F0.wireOp",EDGE,"E8.top")])]}),"instanceName":"1"}),"instanceName":"1"});
            var Q8;
            Q8=makeQuery(id+"F6.opPattern","COPY",BODY,{"derivedFrom":makeQuery(id+"F3.opPattern","COPY",BODY,{"derivedFrom":makeQuery(id+"F2.opExtrude","SWEPT_BODY",BODY,{"disambiguationData":[OSD([sQuery(id+"F0.wireOp",EDGE,"E7.right"),sQuery(id+"F0.wireOp",EDGE,"E8.bottom"),sQuery(id+"F0.wireOp",EDGE,"E8.top"),sQuery(id+"F0.wireOp",EDGE,"E8.right")])]}),"instanceName":"1"}),"instanceName":"1"});
            var Q9;
            Q9=makeQuery(id+"F3.opPattern","COPY",BODY,{"derivedFrom":makeQuery(id+"F1.opExtrude","SWEPT_BODY",BODY,{"disambiguationData":[OSD([sQuery(id+"F0.wireOp",EDGE,"E6.right"),sQuery(id+"F0.wireOp",EDGE,"E7.right"),sQuery(id+"F0.wireOp",EDGE,"E8.bottom"),sQuery(id+"F0.wireOp",EDGE,"E8.top")])]}),"instanceName":"1"});
            var Q10;
            Q10=makeQuery(id+"F3.opPattern","COPY",BODY,{"derivedFrom":makeQuery(id+"F1.opExtrude","SWEPT_BODY",BODY,{"disambiguationData":[OSD([sQuery(id+"F0.wireOp",EDGE,"E4.right"),sQuery(id+"F0.wireOp",EDGE,"E5.right"),sQuery(id+"F0.wireOp",EDGE,"E8.bottom"),sQuery(id+"F0.wireOp",EDGE,"E8.top")])]}),"instanceName":"1"});
            var Q11;
            Q11=makeQuery(id+"F3.opPattern","COPY",BODY,{"derivedFrom":makeQuery(id+"F1.opExtrude","SWEPT_BODY",BODY,{"disambiguationData":[OSD([sQuery(id+"F0.wireOp",EDGE,"E6.left"),sQuery(id+"F0.wireOp",EDGE,"E7.left"),sQuery(id+"F0.wireOp",EDGE,"E8.bottom"),sQuery(id+"F0.wireOp",EDGE,"E8.top")])]}),"instanceName":"1"});
            var Q12;
            Q12=makeQuery(id+"F3.opPattern","COPY",BODY,{"derivedFrom":makeQuery(id+"F1.opExtrude","SWEPT_BODY",BODY,{"disambiguationData":[OSD([sQuery(id+"F0.wireOp",EDGE,"E4.left"),sQuery(id+"F0.wireOp",EDGE,"E5.left"),sQuery(id+"F0.wireOp",EDGE,"E8.bottom"),sQuery(id+"F0.wireOp",EDGE,"E8.top")])]}),"instanceName":"1"});
            var Q13;
            Q13=makeQuery(id+"F3.opPattern","COPY",BODY,{"derivedFrom":makeQuery(id+"F1.opExtrude","SWEPT_BODY",BODY,{"disambiguationData":[OSD([sQuery(id+"F0.wireOp",EDGE,"E2.right"),sQuery(id+"F0.wireOp",EDGE,"E3.right"),sQuery(id+"F0.wireOp",EDGE,"E8.bottom"),sQuery(id+"F0.wireOp",EDGE,"E8.top")])]}),"instanceName":"1"});
            var Q14;
            Q14=makeQuery(id+"F3.opPattern","COPY",BODY,{"derivedFrom":makeQuery(id+"F1.opExtrude","SWEPT_BODY",BODY,{"disambiguationData":[OSD([sQuery(id+"F0.wireOp",EDGE,"E2.left"),sQuery(id+"F0.wireOp",EDGE,"E3.left"),sQuery(id+"F0.wireOp",EDGE,"E8.bottom"),sQuery(id+"F0.wireOp",EDGE,"E8.top")])]}),"instanceName":"1"});
            var Q15;
            Q15=makeQuery(id+"F3.opPattern","COPY",BODY,{"derivedFrom":makeQuery(id+"F1.opExtrude","SWEPT_BODY",BODY,{"disambiguationData":[OSD([sQuery(id+"F0.wireOp",EDGE,"E0.bottom"),sQuery(id+"F0.wireOp",EDGE,"E0.top"),sQuery(id+"F0.wireOp",EDGE,"E0.right"),sQuery(id+"F0.wireOp",EDGE,"E8.left")])]}),"instanceName":"1"});
            var Q16;
            Q16=makeQuery(id+"F3.opPattern","COPY",BODY,{"derivedFrom":makeQuery(id+"F1.opExtrude","SWEPT_BODY",BODY,{"disambiguationData":[OSD([sQuery(id+"F0.wireOp",EDGE,"E0.bottom"),sQuery(id+"F0.wireOp",EDGE,"E0.top"),sQuery(id+"F0.wireOp",EDGE,"E0.left"),sQuery(id+"F0.wireOp",EDGE,"E8.right")])]}),"instanceName":"1"});
            var Q17;
            Q17=makeQuery(id+"F6.opPattern","COPY",BODY,{"derivedFrom":makeQuery(id+"F1.opExtrude","SWEPT_BODY",BODY,{"disambiguationData":[OSD([sQuery(id+"F0.wireOp",EDGE,"E2.right"),sQuery(id+"F0.wireOp",EDGE,"E3.right"),sQuery(id+"F0.wireOp",EDGE,"E8.bottom"),sQuery(id+"F0.wireOp",EDGE,"E8.top")])]}),"instanceName":"1"});
            var Q18;
            Q18=makeQuery(id+"F6.opPattern","COPY",BODY,{"derivedFrom":makeQuery(id+"F1.opExtrude","SWEPT_BODY",BODY,{"disambiguationData":[OSD([sQuery(id+"F0.wireOp",EDGE,"E4.right"),sQuery(id+"F0.wireOp",EDGE,"E5.right"),sQuery(id+"F0.wireOp",EDGE,"E8.bottom"),sQuery(id+"F0.wireOp",EDGE,"E8.top")])]}),"instanceName":"1"});
            var Q19;
            Q19=makeQuery(id+"F6.opPattern","COPY",BODY,{"derivedFrom":makeQuery(id+"F1.opExtrude","SWEPT_BODY",BODY,{"disambiguationData":[OSD([sQuery(id+"F0.wireOp",EDGE,"E4.left"),sQuery(id+"F0.wireOp",EDGE,"E5.left"),sQuery(id+"F0.wireOp",EDGE,"E8.bottom"),sQuery(id+"F0.wireOp",EDGE,"E8.top")])]}),"instanceName":"1"});
            var Q20;
            Q20=makeQuery(id+"F6.opPattern","COPY",BODY,{"derivedFrom":makeQuery(id+"F1.opExtrude","SWEPT_BODY",BODY,{"disambiguationData":[OSD([sQuery(id+"F0.wireOp",EDGE,"E6.left"),sQuery(id+"F0.wireOp",EDGE,"E7.left"),sQuery(id+"F0.wireOp",EDGE,"E8.bottom"),sQuery(id+"F0.wireOp",EDGE,"E8.top")])]}),"instanceName":"1"});
            var Q21;
            Q21=makeQuery(id+"F6.opPattern","COPY",BODY,{"derivedFrom":makeQuery(id+"F1.opExtrude","SWEPT_BODY",BODY,{"disambiguationData":[OSD([sQuery(id+"F0.wireOp",EDGE,"E6.right"),sQuery(id+"F0.wireOp",EDGE,"E7.right"),sQuery(id+"F0.wireOp",EDGE,"E8.bottom"),sQuery(id+"F0.wireOp",EDGE,"E8.top")])]}),"instanceName":"1"});
            var Q22;
            Q22=makeQuery(id+"F6.opPattern","COPY",BODY,{"derivedFrom":makeQuery(id+"F2.opExtrude","SWEPT_BODY",BODY,{"disambiguationData":[OSD([sQuery(id+"F0.wireOp",EDGE,"E1.left"),sQuery(id+"F0.wireOp",EDGE,"E2.left"),sQuery(id+"F0.wireOp",EDGE,"E8.bottom"),sQuery(id+"F0.wireOp",EDGE,"E8.top")])]}),"instanceName":"1"});
            var Q23;
            Q23=makeQuery(id+"F6.opPattern","COPY",BODY,{"derivedFrom":makeQuery(id+"F2.opExtrude","SWEPT_BODY",BODY,{"disambiguationData":[OSD([sQuery(id+"F0.wireOp",EDGE,"E1.right"),sQuery(id+"F0.wireOp",EDGE,"E2.right"),sQuery(id+"F0.wireOp",EDGE,"E8.bottom"),sQuery(id+"F0.wireOp",EDGE,"E8.top")])]}),"instanceName":"1"});
            var Q24;
            Q24=makeQuery(id+"F6.opPattern","COPY",BODY,{"derivedFrom":makeQuery(id+"F2.opExtrude","SWEPT_BODY",BODY,{"disambiguationData":[OSD([sQuery(id+"F0.wireOp",EDGE,"E3.right"),sQuery(id+"F0.wireOp",EDGE,"E4.right"),sQuery(id+"F0.wireOp",EDGE,"E8.bottom"),sQuery(id+"F0.wireOp",EDGE,"E8.top")])]}),"instanceName":"1"});
            var Q25;
            Q25=makeQuery(id+"F6.opPattern","COPY",BODY,{"derivedFrom":makeQuery(id+"F2.opExtrude","SWEPT_BODY",BODY,{"disambiguationData":[OSD([sQuery(id+"F0.wireOp",EDGE,"E5.left"),sQuery(id+"F0.wireOp",EDGE,"E6.left"),sQuery(id+"F0.wireOp",EDGE,"E8.bottom"),sQuery(id+"F0.wireOp",EDGE,"E8.top")])]}),"instanceName":"1"});
            var Q26;
            Q26=makeQuery(id+"F6.opPattern","COPY",BODY,{"derivedFrom":makeQuery(id+"F2.opExtrude","SWEPT_BODY",BODY,{"disambiguationData":[OSD([sQuery(id+"F0.wireOp",EDGE,"E5.right"),sQuery(id+"F0.wireOp",EDGE,"E6.right"),sQuery(id+"F0.wireOp",EDGE,"E8.bottom"),sQuery(id+"F0.wireOp",EDGE,"E8.top")])]}),"instanceName":"1"});
            var Q27;
            Q27=makeQuery(id+"F6.opPattern","COPY",BODY,{"derivedFrom":makeQuery(id+"F2.opExtrude","SWEPT_BODY",BODY,{"disambiguationData":[OSD([sQuery(id+"F0.wireOp",EDGE,"E7.left"),sQuery(id+"F0.wireOp",EDGE,"E8.bottom"),sQuery(id+"F0.wireOp",EDGE,"E8.top"),sQuery(id+"F0.wireOp",EDGE,"E8.left")])]}),"instanceName":"1"});
            var Q28;
            Q28=makeQuery(id+"F6.opPattern","COPY",BODY,{"derivedFrom":makeQuery(id+"F2.opExtrude","SWEPT_BODY",BODY,{"disambiguationData":[OSD([sQuery(id+"F0.wireOp",EDGE,"E7.right"),sQuery(id+"F0.wireOp",EDGE,"E8.bottom"),sQuery(id+"F0.wireOp",EDGE,"E8.top"),sQuery(id+"F0.wireOp",EDGE,"E8.right")])]}),"instanceName":"1"});
            var Q29;
            Q29=makeQuery(id+"F6.opPattern","COPY",BODY,{"derivedFrom":makeQuery(id+"F3.opPattern","COPY",BODY,{"derivedFrom":makeQuery(id+"F1.opExtrude","SWEPT_BODY",BODY,{"disambiguationData":[OSD([sQuery(id+"F0.wireOp",EDGE,"E0.bottom"),sQuery(id+"F0.wireOp",EDGE,"E0.top"),sQuery(id+"F0.wireOp",EDGE,"E0.left"),sQuery(id+"F0.wireOp",EDGE,"E8.right")])]}),"instanceName":"1"}),"instanceName":"1"});
            var Q30;
            Q30=makeQuery(id+"F6.opPattern","COPY",BODY,{"derivedFrom":makeQuery(id+"F3.opPattern","COPY",BODY,{"derivedFrom":makeQuery(id+"F1.opExtrude","SWEPT_BODY",BODY,{"disambiguationData":[OSD([sQuery(id+"F0.wireOp",EDGE,"E1.left"),sQuery(id+"F0.wireOp",EDGE,"E1.right"),sQuery(id+"F0.wireOp",EDGE,"E8.bottom"),sQuery(id+"F0.wireOp",EDGE,"E8.top")])]}),"instanceName":"1"}),"instanceName":"1"});
            var Q31;
            Q31=makeQuery(id+"F6.opPattern","COPY",BODY,{"derivedFrom":makeQuery(id+"F3.opPattern","COPY",BODY,{"derivedFrom":makeQuery(id+"F1.opExtrude","SWEPT_BODY",BODY,{"disambiguationData":[OSD([sQuery(id+"F0.wireOp",EDGE,"E0.bottom"),sQuery(id+"F0.wireOp",EDGE,"E0.top"),sQuery(id+"F0.wireOp",EDGE,"E0.right"),sQuery(id+"F0.wireOp",EDGE,"E8.left")])]}),"instanceName":"1"}),"instanceName":"1"});
            var Q32;
            Q32=makeQuery(id+"F6.opPattern","COPY",BODY,{"derivedFrom":makeQuery(id+"F3.opPattern","COPY",BODY,{"derivedFrom":makeQuery(id+"F1.opExtrude","SWEPT_BODY",BODY,{"disambiguationData":[OSD([sQuery(id+"F0.wireOp",EDGE,"E2.left"),sQuery(id+"F0.wireOp",EDGE,"E3.left"),sQuery(id+"F0.wireOp",EDGE,"E8.bottom"),sQuery(id+"F0.wireOp",EDGE,"E8.top")])]}),"instanceName":"1"}),"instanceName":"1"});
            var Q33;
            Q33=makeQuery(id+"F6.opPattern","COPY",BODY,{"derivedFrom":makeQuery(id+"F3.opPattern","COPY",BODY,{"derivedFrom":makeQuery(id+"F1.opExtrude","SWEPT_BODY",BODY,{"disambiguationData":[OSD([sQuery(id+"F0.wireOp",EDGE,"E2.right"),sQuery(id+"F0.wireOp",EDGE,"E3.right"),sQuery(id+"F0.wireOp",EDGE,"E8.bottom"),sQuery(id+"F0.wireOp",EDGE,"E8.top")])]}),"instanceName":"1"}),"instanceName":"1"});
            var Q34;
            Q34=makeQuery(id+"F6.opPattern","COPY",BODY,{"derivedFrom":makeQuery(id+"F3.opPattern","COPY",BODY,{"derivedFrom":makeQuery(id+"F1.opExtrude","SWEPT_BODY",BODY,{"disambiguationData":[OSD([sQuery(id+"F0.wireOp",EDGE,"E4.left"),sQuery(id+"F0.wireOp",EDGE,"E5.left"),sQuery(id+"F0.wireOp",EDGE,"E8.bottom"),sQuery(id+"F0.wireOp",EDGE,"E8.top")])]}),"instanceName":"1"}),"instanceName":"1"});
            var Q35;
            Q35=makeQuery(id+"F6.opPattern","COPY",BODY,{"derivedFrom":makeQuery(id+"F3.opPattern","COPY",BODY,{"derivedFrom":makeQuery(id+"F1.opExtrude","SWEPT_BODY",BODY,{"disambiguationData":[OSD([sQuery(id+"F0.wireOp",EDGE,"E4.right"),sQuery(id+"F0.wireOp",EDGE,"E5.right"),sQuery(id+"F0.wireOp",EDGE,"E8.bottom"),sQuery(id+"F0.wireOp",EDGE,"E8.top")])]}),"instanceName":"1"}),"instanceName":"1"});
            var Q36;
            Q36=makeQuery(id+"F6.opPattern","COPY",BODY,{"derivedFrom":makeQuery(id+"F3.opPattern","COPY",BODY,{"derivedFrom":makeQuery(id+"F1.opExtrude","SWEPT_BODY",BODY,{"disambiguationData":[OSD([sQuery(id+"F0.wireOp",EDGE,"E6.left"),sQuery(id+"F0.wireOp",EDGE,"E7.left"),sQuery(id+"F0.wireOp",EDGE,"E8.bottom"),sQuery(id+"F0.wireOp",EDGE,"E8.top")])]}),"instanceName":"1"}),"instanceName":"1"});
            var Q37;
            Q37=makeQuery(id+"F6.opPattern","COPY",BODY,{"derivedFrom":makeQuery(id+"F3.opPattern","COPY",BODY,{"derivedFrom":makeQuery(id+"F1.opExtrude","SWEPT_BODY",BODY,{"disambiguationData":[OSD([sQuery(id+"F0.wireOp",EDGE,"E6.right"),sQuery(id+"F0.wireOp",EDGE,"E7.right"),sQuery(id+"F0.wireOp",EDGE,"E8.bottom"),sQuery(id+"F0.wireOp",EDGE,"E8.top")])]}),"instanceName":"1"}),"instanceName":"1"});
            var Q38;
            Q38=makeQuery(id+"F6.opPattern","COPY",BODY,{"derivedFrom":makeQuery(id+"F3.opPattern","COPY",BODY,{"derivedFrom":makeQuery(id+"F2.opExtrude","SWEPT_BODY",BODY,{"disambiguationData":[OSD([sQuery(id+"F0.wireOp",EDGE,"E1.left"),sQuery(id+"F0.wireOp",EDGE,"E2.left"),sQuery(id+"F0.wireOp",EDGE,"E8.bottom"),sQuery(id+"F0.wireOp",EDGE,"E8.top")])]}),"instanceName":"1"}),"instanceName":"1"});
            var Q39;
            Q39=makeQuery(id+"F6.opPattern","COPY",BODY,{"derivedFrom":makeQuery(id+"F3.opPattern","COPY",BODY,{"derivedFrom":makeQuery(id+"F2.opExtrude","SWEPT_BODY",BODY,{"disambiguationData":[OSD([sQuery(id+"F0.wireOp",EDGE,"E1.right"),sQuery(id+"F0.wireOp",EDGE,"E2.right"),sQuery(id+"F0.wireOp",EDGE,"E8.bottom"),sQuery(id+"F0.wireOp",EDGE,"E8.top")])]}),"instanceName":"1"}),"instanceName":"1"});
            var Q40;
            Q40=makeQuery(id+"F6.opPattern","COPY",BODY,{"derivedFrom":makeQuery(id+"F3.opPattern","COPY",BODY,{"derivedFrom":makeQuery(id+"F2.opExtrude","SWEPT_BODY",BODY,{"disambiguationData":[OSD([sQuery(id+"F0.wireOp",EDGE,"E3.left"),sQuery(id+"F0.wireOp",EDGE,"E4.left"),sQuery(id+"F0.wireOp",EDGE,"E8.bottom"),sQuery(id+"F0.wireOp",EDGE,"E8.top")])]}),"instanceName":"1"}),"instanceName":"1"});
            var Q41;
            Q41=makeQuery(id+"F6.opPattern","COPY",BODY,{"derivedFrom":makeQuery(id+"F3.opPattern","COPY",BODY,{"derivedFrom":makeQuery(id+"F2.opExtrude","SWEPT_BODY",BODY,{"disambiguationData":[OSD([sQuery(id+"F0.wireOp",EDGE,"E3.right"),sQuery(id+"F0.wireOp",EDGE,"E4.right"),sQuery(id+"F0.wireOp",EDGE,"E8.bottom"),sQuery(id+"F0.wireOp",EDGE,"E8.top")])]}),"instanceName":"1"}),"instanceName":"1"});
            var Q42;
            Q42=makeQuery(id+"F6.opPattern","COPY",BODY,{"derivedFrom":makeQuery(id+"F1.opExtrude","SWEPT_BODY",BODY,{"disambiguationData":[OSD([sQuery(id+"F0.wireOp",EDGE,"E0.bottom"),sQuery(id+"F0.wireOp",EDGE,"E0.top"),sQuery(id+"F0.wireOp",EDGE,"E0.left"),sQuery(id+"F0.wireOp",EDGE,"E8.right")])]}),"instanceName":"1"});
            var Q43;
            Q43=makeQuery(id+"F3.opPattern","COPY",BODY,{"derivedFrom":makeQuery(id+"F2.opExtrude","SWEPT_BODY",BODY,{"disambiguationData":[OSD([sQuery(id+"F0.wireOp",EDGE,"E5.right"),sQuery(id+"F0.wireOp",EDGE,"E6.right"),sQuery(id+"F0.wireOp",EDGE,"E8.bottom"),sQuery(id+"F0.wireOp",EDGE,"E8.top")])]}),"instanceName":"1"});
            var Q44;
            Q44=makeQuery(id+"F3.opPattern","COPY",BODY,{"derivedFrom":makeQuery(id+"F2.opExtrude","SWEPT_BODY",BODY,{"disambiguationData":[OSD([sQuery(id+"F0.wireOp",EDGE,"E7.left"),sQuery(id+"F0.wireOp",EDGE,"E8.bottom"),sQuery(id+"F0.wireOp",EDGE,"E8.top"),sQuery(id+"F0.wireOp",EDGE,"E8.left")])]}),"instanceName":"1"});
            var Q45;
            Q45=makeQuery(id+"F3.opPattern","COPY",BODY,{"derivedFrom":makeQuery(id+"F2.opExtrude","SWEPT_BODY",BODY,{"disambiguationData":[OSD([sQuery(id+"F0.wireOp",EDGE,"E7.right"),sQuery(id+"F0.wireOp",EDGE,"E8.bottom"),sQuery(id+"F0.wireOp",EDGE,"E8.top"),sQuery(id+"F0.wireOp",EDGE,"E8.right")])]}),"instanceName":"1"});
            var Q46;
            Q46=makeQuery(id+"F2.opExtrude","SWEPT_BODY",BODY,{"disambiguationData":[OSD([sQuery(id+"F0.wireOp",EDGE,"E1.left"),sQuery(id+"F0.wireOp",EDGE,"E2.left"),sQuery(id+"F0.wireOp",EDGE,"E8.bottom"),sQuery(id+"F0.wireOp",EDGE,"E8.top")])]});
            var Q47;
            Q47=makeQuery(id+"F2.opExtrude","SWEPT_BODY",BODY,{"disambiguationData":[OSD([sQuery(id+"F0.wireOp",EDGE,"E1.right"),sQuery(id+"F0.wireOp",EDGE,"E2.right"),sQuery(id+"F0.wireOp",EDGE,"E8.bottom"),sQuery(id+"F0.wireOp",EDGE,"E8.top")])]});
            var Q48;
            Q48=makeQuery(id+"F2.opExtrude","SWEPT_BODY",BODY,{"disambiguationData":[OSD([sQuery(id+"F0.wireOp",EDGE,"E3.right"),sQuery(id+"F0.wireOp",EDGE,"E4.right"),sQuery(id+"F0.wireOp",EDGE,"E8.bottom"),sQuery(id+"F0.wireOp",EDGE,"E8.top")])]});
            var Q49;
            Q49=makeQuery(id+"F2.opExtrude","SWEPT_BODY",BODY,{"disambiguationData":[OSD([sQuery(id+"F0.wireOp",EDGE,"E5.right"),sQuery(id+"F0.wireOp",EDGE,"E6.right"),sQuery(id+"F0.wireOp",EDGE,"E8.bottom"),sQuery(id+"F0.wireOp",EDGE,"E8.top")])]});
            var Q50;
            Q50=makeQuery(id+"F2.opExtrude","SWEPT_BODY",BODY,{"disambiguationData":[OSD([sQuery(id+"F0.wireOp",EDGE,"E3.left"),sQuery(id+"F0.wireOp",EDGE,"E4.left"),sQuery(id+"F0.wireOp",EDGE,"E8.bottom"),sQuery(id+"F0.wireOp",EDGE,"E8.top")])]});
            var Q51;
            Q51=makeQuery(id+"F1.opExtrude","SWEPT_BODY",BODY,{"disambiguationData":[OSD([sQuery(id+"F0.wireOp",EDGE,"E6.right"),sQuery(id+"F0.wireOp",EDGE,"E7.right"),sQuery(id+"F0.wireOp",EDGE,"E8.bottom"),sQuery(id+"F0.wireOp",EDGE,"E8.top")])]});
            var Q52;
            Q52=makeQuery(id+"F1.opExtrude","SWEPT_BODY",BODY,{"disambiguationData":[OSD([sQuery(id+"F0.wireOp",EDGE,"E6.left"),sQuery(id+"F0.wireOp",EDGE,"E7.left"),sQuery(id+"F0.wireOp",EDGE,"E8.bottom"),sQuery(id+"F0.wireOp",EDGE,"E8.top")])]});
            var Q53;
            Q53=makeQuery(id+"F1.opExtrude","SWEPT_BODY",BODY,{"disambiguationData":[OSD([sQuery(id+"F0.wireOp",EDGE,"E4.right"),sQuery(id+"F0.wireOp",EDGE,"E5.right"),sQuery(id+"F0.wireOp",EDGE,"E8.bottom"),sQuery(id+"F0.wireOp",EDGE,"E8.top")])]});
            var Q54;
            Q54=makeQuery(id+"F1.opExtrude","SWEPT_BODY",BODY,{"disambiguationData":[OSD([sQuery(id+"F0.wireOp",EDGE,"E4.left"),sQuery(id+"F0.wireOp",EDGE,"E5.left"),sQuery(id+"F0.wireOp",EDGE,"E8.bottom"),sQuery(id+"F0.wireOp",EDGE,"E8.top")])]});
            var Q55;
            Q55=makeQuery(id+"F1.opExtrude","SWEPT_BODY",BODY,{"disambiguationData":[OSD([sQuery(id+"F0.wireOp",EDGE,"E2.right"),sQuery(id+"F0.wireOp",EDGE,"E3.right"),sQuery(id+"F0.wireOp",EDGE,"E8.bottom"),sQuery(id+"F0.wireOp",EDGE,"E8.top")])]});
            var Q56;
            Q56=makeQuery(id+"F1.opExtrude","SWEPT_BODY",BODY,{"disambiguationData":[OSD([sQuery(id+"F0.wireOp",EDGE,"E2.left"),sQuery(id+"F0.wireOp",EDGE,"E3.left"),sQuery(id+"F0.wireOp",EDGE,"E8.bottom"),sQuery(id+"F0.wireOp",EDGE,"E8.top")])]});
            var Q57;
            Q57=makeQuery(id+"F1.opExtrude","SWEPT_BODY",BODY,{"disambiguationData":[OSD([sQuery(id+"F0.wireOp",EDGE,"E0.bottom"),sQuery(id+"F0.wireOp",EDGE,"E0.top"),sQuery(id+"F0.wireOp",EDGE,"E0.right"),sQuery(id+"F0.wireOp",EDGE,"E8.left")])]});
            var Q58;
            Q58=makeQuery(id+"F1.opExtrude","SWEPT_BODY",BODY,{"disambiguationData":[OSD([sQuery(id+"F0.wireOp",EDGE,"E1.left"),sQuery(id+"F0.wireOp",EDGE,"E1.right"),sQuery(id+"F0.wireOp",EDGE,"E8.bottom"),sQuery(id+"F0.wireOp",EDGE,"E8.top")])]});
            var Q59;
            Q59=makeQuery(id+"F2.opExtrude","SWEPT_BODY",BODY,{"disambiguationData":[OSD([sQuery(id+"F0.wireOp",EDGE,"E5.left"),sQuery(id+"F0.wireOp",EDGE,"E6.left"),sQuery(id+"F0.wireOp",EDGE,"E8.bottom"),sQuery(id+"F0.wireOp",EDGE,"E8.top")])]});
            var Q60;
            Q60=makeQuery(id+"F1.opExtrude","SWEPT_BODY",BODY,{"disambiguationData":[OSD([sQuery(id+"F0.wireOp",EDGE,"E0.bottom"),sQuery(id+"F0.wireOp",EDGE,"E0.top"),sQuery(id+"F0.wireOp",EDGE,"E0.left"),sQuery(id+"F0.wireOp",EDGE,"E8.right")])]});
            var Q61;
            Q61=makeQuery(id+"F2.opExtrude","SWEPT_BODY",BODY,{"disambiguationData":[OSD([sQuery(id+"F0.wireOp",EDGE,"E7.right"),sQuery(id+"F0.wireOp",EDGE,"E8.bottom"),sQuery(id+"F0.wireOp",EDGE,"E8.top"),sQuery(id+"F0.wireOp",EDGE,"E8.right")])]});
            var Q62;
            Q62=makeQuery(id+"F2.opExtrude","SWEPT_BODY",BODY,{"disambiguationData":[OSD([sQuery(id+"F0.wireOp",EDGE,"E7.left"),sQuery(id+"F0.wireOp",EDGE,"E8.bottom"),sQuery(id+"F0.wireOp",EDGE,"E8.top"),sQuery(id+"F0.wireOp",EDGE,"E8.left")])]});
            var Q63;
            Q63=makeQuery(id+"F3.opPattern","COPY",BODY,{"derivedFrom":makeQuery(id+"F2.opExtrude","SWEPT_BODY",BODY,{"disambiguationData":[OSD([sQuery(id+"F0.wireOp",EDGE,"E1.left"),sQuery(id+"F0.wireOp",EDGE,"E2.left"),sQuery(id+"F0.wireOp",EDGE,"E8.bottom"),sQuery(id+"F0.wireOp",EDGE,"E8.top")])]}),"instanceName":"1"});
            var Q64;
            Q64=makeQuery(id+"F6.opPattern","COPY",BODY,{"derivedFrom":makeQuery(id+"F1.opExtrude","SWEPT_BODY",BODY,{"disambiguationData":[OSD([sQuery(id+"F0.wireOp",EDGE,"E2.left"),sQuery(id+"F0.wireOp",EDGE,"E3.left"),sQuery(id+"F0.wireOp",EDGE,"E8.bottom"),sQuery(id+"F0.wireOp",EDGE,"E8.top")])]}),"instanceName":"1"});
            var Q65;
            Q65=makeQuery(id+"F6.opPattern","COPY",BODY,{"derivedFrom":makeQuery(id+"F2.opExtrude","SWEPT_BODY",BODY,{"disambiguationData":[OSD([sQuery(id+"F0.wireOp",EDGE,"E3.left"),sQuery(id+"F0.wireOp",EDGE,"E4.left"),sQuery(id+"F0.wireOp",EDGE,"E8.bottom"),sQuery(id+"F0.wireOp",EDGE,"E8.top")])]}),"instanceName":"1"});
            var Q66;
            Q66=makeQuery(id+"F3.opPattern","COPY",BODY,{"derivedFrom":makeQuery(id+"F1.opExtrude","SWEPT_BODY",BODY,{"disambiguationData":[OSD([sQuery(id+"F0.wireOp",EDGE,"E1.left"),sQuery(id+"F0.wireOp",EDGE,"E1.right"),sQuery(id+"F0.wireOp",EDGE,"E8.bottom"),sQuery(id+"F0.wireOp",EDGE,"E8.top")])]}),"instanceName":"1"});
            var Q67;
            Q67=makeQuery(id+"F6.opPattern","COPY",BODY,{"derivedFrom":makeQuery(id+"F1.opExtrude","SWEPT_BODY",BODY,{"disambiguationData":[OSD([sQuery(id+"F0.wireOp",EDGE,"E1.left"),sQuery(id+"F0.wireOp",EDGE,"E1.right"),sQuery(id+"F0.wireOp",EDGE,"E8.bottom"),sQuery(id+"F0.wireOp",EDGE,"E8.top")])]}),"instanceName":"1"});
            transform(context, id + "F8", {"entities" : qUnion([Q0, Q1, Q2, Q3, Q4, Q5, Q6, Q7, Q8, Q9, Q10, Q11, Q12, Q13, Q14, Q15, Q16, Q17, Q18, Q19, Q20, Q21, Q22, Q23, Q24, Q25, Q26, Q27, Q28, Q29, Q30, Q31, Q32, Q33, Q34, Q35, Q36, Q37, Q38, Q39, Q40, Q41, Q42, Q43, Q44, Q45, Q46, Q47, Q48, Q49, Q50, Q51, Q52, Q53, Q54, Q55, Q56, Q57, Q58, Q59, Q60, Q61, Q62, Q63, Q64, Q65, Q66, Q67]), "transformType" : TransformType.TRANSLATION_3D, "dx" : 0 * mm, "dy" : 0 * mm, "dz" : 25.4 * mm, "makeCopy" : true});
        }
        {
            var Q0;
            Q0=makeQuery(id+"F8.opPattern","COPY",BODY,{"derivedFrom":makeQuery(id+"F6.opPattern","COPY",BODY,{"derivedFrom":makeQuery(id+"F1.opExtrude","SWEPT_BODY",BODY,{"disambiguationData":[OSD([sQuery(id+"F0.wireOp",EDGE,"E2.left"),sQuery(id+"F0.wireOp",EDGE,"E3.left"),sQuery(id+"F0.wireOp",EDGE,"E8.bottom"),sQuery(id+"F0.wireOp",EDGE,"E8.top")])]}),"instanceName":"1"}),"instanceName":"1"});
            var Q1;
            Q1=makeQuery(id+"F8.opPattern","COPY",BODY,{"derivedFrom":makeQuery(id+"F6.opPattern","COPY",BODY,{"derivedFrom":makeQuery(id+"F1.opExtrude","SWEPT_BODY",BODY,{"disambiguationData":[OSD([sQuery(id+"F0.wireOp",EDGE,"E6.left"),sQuery(id+"F0.wireOp",EDGE,"E7.left"),sQuery(id+"F0.wireOp",EDGE,"E8.bottom"),sQuery(id+"F0.wireOp",EDGE,"E8.top")])]}),"instanceName":"1"}),"instanceName":"1"});
            var Q2;
            Q2=makeQuery(id+"F8.opPattern","COPY",BODY,{"derivedFrom":makeQuery(id+"F3.opPattern","COPY",BODY,{"derivedFrom":makeQuery(id+"F1.opExtrude","SWEPT_BODY",BODY,{"disambiguationData":[OSD([sQuery(id+"F0.wireOp",EDGE,"E4.right"),sQuery(id+"F0.wireOp",EDGE,"E5.right"),sQuery(id+"F0.wireOp",EDGE,"E8.bottom"),sQuery(id+"F0.wireOp",EDGE,"E8.top")])]}),"instanceName":"1"}),"instanceName":"1"});
            var Q3;
            Q3=makeQuery(id+"F8.opPattern","COPY",BODY,{"derivedFrom":makeQuery(id+"F6.opPattern","COPY",BODY,{"derivedFrom":makeQuery(id+"F1.opExtrude","SWEPT_BODY",BODY,{"disambiguationData":[OSD([sQuery(id+"F0.wireOp",EDGE,"E0.bottom"),sQuery(id+"F0.wireOp",EDGE,"E0.top"),sQuery(id+"F0.wireOp",EDGE,"E0.right"),sQuery(id+"F0.wireOp",EDGE,"E8.left")])]}),"instanceName":"1"}),"instanceName":"1"});
            var Q4;
            Q4=makeQuery(id+"F8.opPattern","COPY",BODY,{"derivedFrom":makeQuery(id+"F6.opPattern","COPY",BODY,{"derivedFrom":makeQuery(id+"F1.opExtrude","SWEPT_BODY",BODY,{"disambiguationData":[OSD([sQuery(id+"F0.wireOp",EDGE,"E0.bottom"),sQuery(id+"F0.wireOp",EDGE,"E0.top"),sQuery(id+"F0.wireOp",EDGE,"E0.left"),sQuery(id+"F0.wireOp",EDGE,"E8.right")])]}),"instanceName":"1"}),"instanceName":"1"});
            var Q5;
            Q5=makeQuery(id+"F8.opPattern","COPY",BODY,{"derivedFrom":makeQuery(id+"F3.opPattern","COPY",BODY,{"derivedFrom":makeQuery(id+"F2.opExtrude","SWEPT_BODY",BODY,{"disambiguationData":[OSD([sQuery(id+"F0.wireOp",EDGE,"E7.right"),sQuery(id+"F0.wireOp",EDGE,"E8.bottom"),sQuery(id+"F0.wireOp",EDGE,"E8.top"),sQuery(id+"F0.wireOp",EDGE,"E8.right")])]}),"instanceName":"1"}),"instanceName":"1"});
            var Q6;
            Q6=makeQuery(id+"F8.opPattern","COPY",BODY,{"derivedFrom":makeQuery(id+"F3.opPattern","COPY",BODY,{"derivedFrom":makeQuery(id+"F2.opExtrude","SWEPT_BODY",BODY,{"disambiguationData":[OSD([sQuery(id+"F0.wireOp",EDGE,"E7.left"),sQuery(id+"F0.wireOp",EDGE,"E8.bottom"),sQuery(id+"F0.wireOp",EDGE,"E8.top"),sQuery(id+"F0.wireOp",EDGE,"E8.left")])]}),"instanceName":"1"}),"instanceName":"1"});
            var Q7;
            Q7=makeQuery(id+"F8.opPattern","COPY",BODY,{"derivedFrom":makeQuery(id+"F3.opPattern","COPY",BODY,{"derivedFrom":makeQuery(id+"F2.opExtrude","SWEPT_BODY",BODY,{"disambiguationData":[OSD([sQuery(id+"F0.wireOp",EDGE,"E5.right"),sQuery(id+"F0.wireOp",EDGE,"E6.right"),sQuery(id+"F0.wireOp",EDGE,"E8.bottom"),sQuery(id+"F0.wireOp",EDGE,"E8.top")])]}),"instanceName":"1"}),"instanceName":"1"});
            var Q8;
            Q8=makeQuery(id+"F8.opPattern","COPY",BODY,{"derivedFrom":makeQuery(id+"F3.opPattern","COPY",BODY,{"derivedFrom":makeQuery(id+"F2.opExtrude","SWEPT_BODY",BODY,{"disambiguationData":[OSD([sQuery(id+"F0.wireOp",EDGE,"E5.left"),sQuery(id+"F0.wireOp",EDGE,"E6.left"),sQuery(id+"F0.wireOp",EDGE,"E8.bottom"),sQuery(id+"F0.wireOp",EDGE,"E8.top")])]}),"instanceName":"1"}),"instanceName":"1"});
            var Q9;
            Q9=makeQuery(id+"F8.opPattern","COPY",BODY,{"derivedFrom":makeQuery(id+"F3.opPattern","COPY",BODY,{"derivedFrom":makeQuery(id+"F2.opExtrude","SWEPT_BODY",BODY,{"disambiguationData":[OSD([sQuery(id+"F0.wireOp",EDGE,"E3.right"),sQuery(id+"F0.wireOp",EDGE,"E4.right"),sQuery(id+"F0.wireOp",EDGE,"E8.bottom"),sQuery(id+"F0.wireOp",EDGE,"E8.top")])]}),"instanceName":"1"}),"instanceName":"1"});
            var Q10;
            Q10=makeQuery(id+"F8.opPattern","COPY",BODY,{"derivedFrom":makeQuery(id+"F3.opPattern","COPY",BODY,{"derivedFrom":makeQuery(id+"F2.opExtrude","SWEPT_BODY",BODY,{"disambiguationData":[OSD([sQuery(id+"F0.wireOp",EDGE,"E3.left"),sQuery(id+"F0.wireOp",EDGE,"E4.left"),sQuery(id+"F0.wireOp",EDGE,"E8.bottom"),sQuery(id+"F0.wireOp",EDGE,"E8.top")])]}),"instanceName":"1"}),"instanceName":"1"});
            var Q11;
            Q11=makeQuery(id+"F8.opPattern","COPY",BODY,{"derivedFrom":makeQuery(id+"F3.opPattern","COPY",BODY,{"derivedFrom":makeQuery(id+"F2.opExtrude","SWEPT_BODY",BODY,{"disambiguationData":[OSD([sQuery(id+"F0.wireOp",EDGE,"E1.right"),sQuery(id+"F0.wireOp",EDGE,"E2.right"),sQuery(id+"F0.wireOp",EDGE,"E8.bottom"),sQuery(id+"F0.wireOp",EDGE,"E8.top")])]}),"instanceName":"1"}),"instanceName":"1"});
            var Q12;
            Q12=makeQuery(id+"F8.opPattern","COPY",BODY,{"derivedFrom":makeQuery(id+"F3.opPattern","COPY",BODY,{"derivedFrom":makeQuery(id+"F2.opExtrude","SWEPT_BODY",BODY,{"disambiguationData":[OSD([sQuery(id+"F0.wireOp",EDGE,"E1.left"),sQuery(id+"F0.wireOp",EDGE,"E2.left"),sQuery(id+"F0.wireOp",EDGE,"E8.bottom"),sQuery(id+"F0.wireOp",EDGE,"E8.top")])]}),"instanceName":"1"}),"instanceName":"1"});
            var Q13;
            Q13=makeQuery(id+"F8.opPattern","COPY",BODY,{"derivedFrom":makeQuery(id+"F3.opPattern","COPY",BODY,{"derivedFrom":makeQuery(id+"F1.opExtrude","SWEPT_BODY",BODY,{"disambiguationData":[OSD([sQuery(id+"F0.wireOp",EDGE,"E6.right"),sQuery(id+"F0.wireOp",EDGE,"E7.right"),sQuery(id+"F0.wireOp",EDGE,"E8.bottom"),sQuery(id+"F0.wireOp",EDGE,"E8.top")])]}),"instanceName":"1"}),"instanceName":"1"});
            var Q14;
            Q14=makeQuery(id+"F8.opPattern","COPY",BODY,{"derivedFrom":makeQuery(id+"F6.opPattern","COPY",BODY,{"derivedFrom":makeQuery(id+"F1.opExtrude","SWEPT_BODY",BODY,{"disambiguationData":[OSD([sQuery(id+"F0.wireOp",EDGE,"E4.right"),sQuery(id+"F0.wireOp",EDGE,"E5.right"),sQuery(id+"F0.wireOp",EDGE,"E8.bottom"),sQuery(id+"F0.wireOp",EDGE,"E8.top")])]}),"instanceName":"1"}),"instanceName":"1"});
            var Q15;
            Q15=makeQuery(id+"F8.opPattern","COPY",BODY,{"derivedFrom":makeQuery(id+"F6.opPattern","COPY",BODY,{"derivedFrom":makeQuery(id+"F1.opExtrude","SWEPT_BODY",BODY,{"disambiguationData":[OSD([sQuery(id+"F0.wireOp",EDGE,"E4.left"),sQuery(id+"F0.wireOp",EDGE,"E5.left"),sQuery(id+"F0.wireOp",EDGE,"E8.bottom"),sQuery(id+"F0.wireOp",EDGE,"E8.top")])]}),"instanceName":"1"}),"instanceName":"1"});
            var Q16;
            Q16=makeQuery(id+"F8.opPattern","COPY",BODY,{"derivedFrom":makeQuery(id+"F3.opPattern","COPY",BODY,{"derivedFrom":makeQuery(id+"F1.opExtrude","SWEPT_BODY",BODY,{"disambiguationData":[OSD([sQuery(id+"F0.wireOp",EDGE,"E4.left"),sQuery(id+"F0.wireOp",EDGE,"E5.left"),sQuery(id+"F0.wireOp",EDGE,"E8.bottom"),sQuery(id+"F0.wireOp",EDGE,"E8.top")])]}),"instanceName":"1"}),"instanceName":"1"});
            var Q17;
            Q17=makeQuery(id+"F8.opPattern","COPY",BODY,{"derivedFrom":makeQuery(id+"F3.opPattern","COPY",BODY,{"derivedFrom":makeQuery(id+"F1.opExtrude","SWEPT_BODY",BODY,{"disambiguationData":[OSD([sQuery(id+"F0.wireOp",EDGE,"E2.right"),sQuery(id+"F0.wireOp",EDGE,"E3.right"),sQuery(id+"F0.wireOp",EDGE,"E8.bottom"),sQuery(id+"F0.wireOp",EDGE,"E8.top")])]}),"instanceName":"1"}),"instanceName":"1"});
            var Q18;
            Q18=makeQuery(id+"F8.opPattern","COPY",BODY,{"derivedFrom":makeQuery(id+"F3.opPattern","COPY",BODY,{"derivedFrom":makeQuery(id+"F1.opExtrude","SWEPT_BODY",BODY,{"disambiguationData":[OSD([sQuery(id+"F0.wireOp",EDGE,"E2.left"),sQuery(id+"F0.wireOp",EDGE,"E3.left"),sQuery(id+"F0.wireOp",EDGE,"E8.bottom"),sQuery(id+"F0.wireOp",EDGE,"E8.top")])]}),"instanceName":"1"}),"instanceName":"1"});
            var Q19;
            Q19=makeQuery(id+"F8.opPattern","COPY",BODY,{"derivedFrom":makeQuery(id+"F1.opExtrude","SWEPT_BODY",BODY,{"disambiguationData":[OSD([sQuery(id+"F0.wireOp",EDGE,"E0.bottom"),sQuery(id+"F0.wireOp",EDGE,"E0.top"),sQuery(id+"F0.wireOp",EDGE,"E0.left"),sQuery(id+"F0.wireOp",EDGE,"E8.right")])]}),"instanceName":"1"});
            var Q20;
            Q20=makeQuery(id+"F8.opPattern","COPY",BODY,{"derivedFrom":makeQuery(id+"F1.opExtrude","SWEPT_BODY",BODY,{"disambiguationData":[OSD([sQuery(id+"F0.wireOp",EDGE,"E0.bottom"),sQuery(id+"F0.wireOp",EDGE,"E0.top"),sQuery(id+"F0.wireOp",EDGE,"E0.right"),sQuery(id+"F0.wireOp",EDGE,"E8.left")])]}),"instanceName":"1"});
            var Q21;
            Q21=makeQuery(id+"F8.opPattern","COPY",BODY,{"derivedFrom":makeQuery(id+"F1.opExtrude","SWEPT_BODY",BODY,{"disambiguationData":[OSD([sQuery(id+"F0.wireOp",EDGE,"E1.left"),sQuery(id+"F0.wireOp",EDGE,"E1.right"),sQuery(id+"F0.wireOp",EDGE,"E8.bottom"),sQuery(id+"F0.wireOp",EDGE,"E8.top")])]}),"instanceName":"1"});
            var Q22;
            Q22=makeQuery(id+"F8.opPattern","COPY",BODY,{"derivedFrom":makeQuery(id+"F1.opExtrude","SWEPT_BODY",BODY,{"disambiguationData":[OSD([sQuery(id+"F0.wireOp",EDGE,"E2.left"),sQuery(id+"F0.wireOp",EDGE,"E3.left"),sQuery(id+"F0.wireOp",EDGE,"E8.bottom"),sQuery(id+"F0.wireOp",EDGE,"E8.top")])]}),"instanceName":"1"});
            var Q23;
            Q23=makeQuery(id+"F8.opPattern","COPY",BODY,{"derivedFrom":makeQuery(id+"F1.opExtrude","SWEPT_BODY",BODY,{"disambiguationData":[OSD([sQuery(id+"F0.wireOp",EDGE,"E2.right"),sQuery(id+"F0.wireOp",EDGE,"E3.right"),sQuery(id+"F0.wireOp",EDGE,"E8.bottom"),sQuery(id+"F0.wireOp",EDGE,"E8.top")])]}),"instanceName":"1"});
            var Q24;
            Q24=makeQuery(id+"F8.opPattern","COPY",BODY,{"derivedFrom":makeQuery(id+"F1.opExtrude","SWEPT_BODY",BODY,{"disambiguationData":[OSD([sQuery(id+"F0.wireOp",EDGE,"E4.right"),sQuery(id+"F0.wireOp",EDGE,"E5.right"),sQuery(id+"F0.wireOp",EDGE,"E8.bottom"),sQuery(id+"F0.wireOp",EDGE,"E8.top")])]}),"instanceName":"1"});
            var Q25;
            Q25=makeQuery(id+"F8.opPattern","COPY",BODY,{"derivedFrom":makeQuery(id+"F1.opExtrude","SWEPT_BODY",BODY,{"disambiguationData":[OSD([sQuery(id+"F0.wireOp",EDGE,"E4.left"),sQuery(id+"F0.wireOp",EDGE,"E5.left"),sQuery(id+"F0.wireOp",EDGE,"E8.bottom"),sQuery(id+"F0.wireOp",EDGE,"E8.top")])]}),"instanceName":"1"});
            var Q26;
            Q26=makeQuery(id+"F8.opPattern","COPY",BODY,{"derivedFrom":makeQuery(id+"F1.opExtrude","SWEPT_BODY",BODY,{"disambiguationData":[OSD([sQuery(id+"F0.wireOp",EDGE,"E6.left"),sQuery(id+"F0.wireOp",EDGE,"E7.left"),sQuery(id+"F0.wireOp",EDGE,"E8.bottom"),sQuery(id+"F0.wireOp",EDGE,"E8.top")])]}),"instanceName":"1"});
            var Q27;
            Q27=makeQuery(id+"F8.opPattern","COPY",BODY,{"derivedFrom":makeQuery(id+"F1.opExtrude","SWEPT_BODY",BODY,{"disambiguationData":[OSD([sQuery(id+"F0.wireOp",EDGE,"E6.right"),sQuery(id+"F0.wireOp",EDGE,"E7.right"),sQuery(id+"F0.wireOp",EDGE,"E8.bottom"),sQuery(id+"F0.wireOp",EDGE,"E8.top")])]}),"instanceName":"1"});
            var Q28;
            Q28=makeQuery(id+"F8.opPattern","COPY",BODY,{"derivedFrom":makeQuery(id+"F2.opExtrude","SWEPT_BODY",BODY,{"disambiguationData":[OSD([sQuery(id+"F0.wireOp",EDGE,"E1.left"),sQuery(id+"F0.wireOp",EDGE,"E2.left"),sQuery(id+"F0.wireOp",EDGE,"E8.bottom"),sQuery(id+"F0.wireOp",EDGE,"E8.top")])]}),"instanceName":"1"});
            var Q29;
            Q29=makeQuery(id+"F8.opPattern","COPY",BODY,{"derivedFrom":makeQuery(id+"F2.opExtrude","SWEPT_BODY",BODY,{"disambiguationData":[OSD([sQuery(id+"F0.wireOp",EDGE,"E1.right"),sQuery(id+"F0.wireOp",EDGE,"E2.right"),sQuery(id+"F0.wireOp",EDGE,"E8.bottom"),sQuery(id+"F0.wireOp",EDGE,"E8.top")])]}),"instanceName":"1"});
            var Q30;
            Q30=makeQuery(id+"F8.opPattern","COPY",BODY,{"derivedFrom":makeQuery(id+"F2.opExtrude","SWEPT_BODY",BODY,{"disambiguationData":[OSD([sQuery(id+"F0.wireOp",EDGE,"E3.left"),sQuery(id+"F0.wireOp",EDGE,"E4.left"),sQuery(id+"F0.wireOp",EDGE,"E8.bottom"),sQuery(id+"F0.wireOp",EDGE,"E8.top")])]}),"instanceName":"1"});
            var Q31;
            Q31=makeQuery(id+"F8.opPattern","COPY",BODY,{"derivedFrom":makeQuery(id+"F2.opExtrude","SWEPT_BODY",BODY,{"disambiguationData":[OSD([sQuery(id+"F0.wireOp",EDGE,"E3.right"),sQuery(id+"F0.wireOp",EDGE,"E4.right"),sQuery(id+"F0.wireOp",EDGE,"E8.bottom"),sQuery(id+"F0.wireOp",EDGE,"E8.top")])]}),"instanceName":"1"});
            var Q32;
            Q32=makeQuery(id+"F8.opPattern","COPY",BODY,{"derivedFrom":makeQuery(id+"F2.opExtrude","SWEPT_BODY",BODY,{"disambiguationData":[OSD([sQuery(id+"F0.wireOp",EDGE,"E5.left"),sQuery(id+"F0.wireOp",EDGE,"E6.left"),sQuery(id+"F0.wireOp",EDGE,"E8.bottom"),sQuery(id+"F0.wireOp",EDGE,"E8.top")])]}),"instanceName":"1"});
            var Q33;
            Q33=makeQuery(id+"F8.opPattern","COPY",BODY,{"derivedFrom":makeQuery(id+"F2.opExtrude","SWEPT_BODY",BODY,{"disambiguationData":[OSD([sQuery(id+"F0.wireOp",EDGE,"E5.right"),sQuery(id+"F0.wireOp",EDGE,"E6.right"),sQuery(id+"F0.wireOp",EDGE,"E8.bottom"),sQuery(id+"F0.wireOp",EDGE,"E8.top")])]}),"instanceName":"1"});
            var Q34;
            Q34=makeQuery(id+"F8.opPattern","COPY",BODY,{"derivedFrom":makeQuery(id+"F2.opExtrude","SWEPT_BODY",BODY,{"disambiguationData":[OSD([sQuery(id+"F0.wireOp",EDGE,"E7.left"),sQuery(id+"F0.wireOp",EDGE,"E8.bottom"),sQuery(id+"F0.wireOp",EDGE,"E8.top"),sQuery(id+"F0.wireOp",EDGE,"E8.left")])]}),"instanceName":"1"});
            var Q35;
            Q35=makeQuery(id+"F8.opPattern","COPY",BODY,{"derivedFrom":makeQuery(id+"F2.opExtrude","SWEPT_BODY",BODY,{"disambiguationData":[OSD([sQuery(id+"F0.wireOp",EDGE,"E7.right"),sQuery(id+"F0.wireOp",EDGE,"E8.bottom"),sQuery(id+"F0.wireOp",EDGE,"E8.top"),sQuery(id+"F0.wireOp",EDGE,"E8.right")])]}),"instanceName":"1"});
            var Q36;
            Q36=makeQuery(id+"F8.opPattern","COPY",BODY,{"derivedFrom":makeQuery(id+"F3.opPattern","COPY",BODY,{"derivedFrom":makeQuery(id+"F1.opExtrude","SWEPT_BODY",BODY,{"disambiguationData":[OSD([sQuery(id+"F0.wireOp",EDGE,"E0.bottom"),sQuery(id+"F0.wireOp",EDGE,"E0.top"),sQuery(id+"F0.wireOp",EDGE,"E0.left"),sQuery(id+"F0.wireOp",EDGE,"E8.right")])]}),"instanceName":"1"}),"instanceName":"1"});
            var Q37;
            Q37=makeQuery(id+"F8.opPattern","COPY",BODY,{"derivedFrom":makeQuery(id+"F3.opPattern","COPY",BODY,{"derivedFrom":makeQuery(id+"F1.opExtrude","SWEPT_BODY",BODY,{"disambiguationData":[OSD([sQuery(id+"F0.wireOp",EDGE,"E0.bottom"),sQuery(id+"F0.wireOp",EDGE,"E0.top"),sQuery(id+"F0.wireOp",EDGE,"E0.right"),sQuery(id+"F0.wireOp",EDGE,"E8.left")])]}),"instanceName":"1"}),"instanceName":"1"});
            var Q38;
            Q38=makeQuery(id+"F8.opPattern","COPY",BODY,{"derivedFrom":makeQuery(id+"F3.opPattern","COPY",BODY,{"derivedFrom":makeQuery(id+"F1.opExtrude","SWEPT_BODY",BODY,{"disambiguationData":[OSD([sQuery(id+"F0.wireOp",EDGE,"E6.left"),sQuery(id+"F0.wireOp",EDGE,"E7.left"),sQuery(id+"F0.wireOp",EDGE,"E8.bottom"),sQuery(id+"F0.wireOp",EDGE,"E8.top")])]}),"instanceName":"1"}),"instanceName":"1"});
            var Q39;
            Q39=makeQuery(id+"F8.opPattern","COPY",BODY,{"derivedFrom":makeQuery(id+"F6.opPattern","COPY",BODY,{"derivedFrom":makeQuery(id+"F1.opExtrude","SWEPT_BODY",BODY,{"disambiguationData":[OSD([sQuery(id+"F0.wireOp",EDGE,"E2.right"),sQuery(id+"F0.wireOp",EDGE,"E3.right"),sQuery(id+"F0.wireOp",EDGE,"E8.bottom"),sQuery(id+"F0.wireOp",EDGE,"E8.top")])]}),"instanceName":"1"}),"instanceName":"1"});
            var Q40;
            Q40=makeQuery(id+"F8.opPattern","COPY",BODY,{"derivedFrom":makeQuery(id+"F6.opPattern","COPY",BODY,{"derivedFrom":makeQuery(id+"F2.opExtrude","SWEPT_BODY",BODY,{"disambiguationData":[OSD([sQuery(id+"F0.wireOp",EDGE,"E1.left"),sQuery(id+"F0.wireOp",EDGE,"E2.left"),sQuery(id+"F0.wireOp",EDGE,"E8.bottom"),sQuery(id+"F0.wireOp",EDGE,"E8.top")])]}),"instanceName":"1"}),"instanceName":"1"});
            var Q41;
            Q41=makeQuery(id+"F8.opPattern","COPY",BODY,{"derivedFrom":makeQuery(id+"F6.opPattern","COPY",BODY,{"derivedFrom":makeQuery(id+"F1.opExtrude","SWEPT_BODY",BODY,{"disambiguationData":[OSD([sQuery(id+"F0.wireOp",EDGE,"E6.right"),sQuery(id+"F0.wireOp",EDGE,"E7.right"),sQuery(id+"F0.wireOp",EDGE,"E8.bottom"),sQuery(id+"F0.wireOp",EDGE,"E8.top")])]}),"instanceName":"1"}),"instanceName":"1"});
            var Q42;
            Q42=makeQuery(id+"F8.opPattern","COPY",BODY,{"derivedFrom":makeQuery(id+"F6.opPattern","COPY",BODY,{"derivedFrom":makeQuery(id+"F2.opExtrude","SWEPT_BODY",BODY,{"disambiguationData":[OSD([sQuery(id+"F0.wireOp",EDGE,"E1.right"),sQuery(id+"F0.wireOp",EDGE,"E2.right"),sQuery(id+"F0.wireOp",EDGE,"E8.bottom"),sQuery(id+"F0.wireOp",EDGE,"E8.top")])]}),"instanceName":"1"}),"instanceName":"1"});
            var Q43;
            Q43=makeQuery(id+"F8.opPattern","COPY",BODY,{"derivedFrom":makeQuery(id+"F6.opPattern","COPY",BODY,{"derivedFrom":makeQuery(id+"F2.opExtrude","SWEPT_BODY",BODY,{"disambiguationData":[OSD([sQuery(id+"F0.wireOp",EDGE,"E3.left"),sQuery(id+"F0.wireOp",EDGE,"E4.left"),sQuery(id+"F0.wireOp",EDGE,"E8.bottom"),sQuery(id+"F0.wireOp",EDGE,"E8.top")])]}),"instanceName":"1"}),"instanceName":"1"});
            var Q44;
            Q44=makeQuery(id+"F8.opPattern","COPY",BODY,{"derivedFrom":makeQuery(id+"F6.opPattern","COPY",BODY,{"derivedFrom":makeQuery(id+"F2.opExtrude","SWEPT_BODY",BODY,{"disambiguationData":[OSD([sQuery(id+"F0.wireOp",EDGE,"E3.right"),sQuery(id+"F0.wireOp",EDGE,"E4.right"),sQuery(id+"F0.wireOp",EDGE,"E8.bottom"),sQuery(id+"F0.wireOp",EDGE,"E8.top")])]}),"instanceName":"1"}),"instanceName":"1"});
            var Q45;
            Q45=makeQuery(id+"F8.opPattern","COPY",BODY,{"derivedFrom":makeQuery(id+"F6.opPattern","COPY",BODY,{"derivedFrom":makeQuery(id+"F2.opExtrude","SWEPT_BODY",BODY,{"disambiguationData":[OSD([sQuery(id+"F0.wireOp",EDGE,"E5.left"),sQuery(id+"F0.wireOp",EDGE,"E6.left"),sQuery(id+"F0.wireOp",EDGE,"E8.bottom"),sQuery(id+"F0.wireOp",EDGE,"E8.top")])]}),"instanceName":"1"}),"instanceName":"1"});
            var Q46;
            Q46=makeQuery(id+"F8.opPattern","COPY",BODY,{"derivedFrom":makeQuery(id+"F6.opPattern","COPY",BODY,{"derivedFrom":makeQuery(id+"F2.opExtrude","SWEPT_BODY",BODY,{"disambiguationData":[OSD([sQuery(id+"F0.wireOp",EDGE,"E5.right"),sQuery(id+"F0.wireOp",EDGE,"E6.right"),sQuery(id+"F0.wireOp",EDGE,"E8.bottom"),sQuery(id+"F0.wireOp",EDGE,"E8.top")])]}),"instanceName":"1"}),"instanceName":"1"});
            var Q47;
            Q47=makeQuery(id+"F8.opPattern","COPY",BODY,{"derivedFrom":makeQuery(id+"F6.opPattern","COPY",BODY,{"derivedFrom":makeQuery(id+"F2.opExtrude","SWEPT_BODY",BODY,{"disambiguationData":[OSD([sQuery(id+"F0.wireOp",EDGE,"E7.left"),sQuery(id+"F0.wireOp",EDGE,"E8.bottom"),sQuery(id+"F0.wireOp",EDGE,"E8.top"),sQuery(id+"F0.wireOp",EDGE,"E8.left")])]}),"instanceName":"1"}),"instanceName":"1"});
            var Q48;
            Q48=makeQuery(id+"F8.opPattern","COPY",BODY,{"derivedFrom":makeQuery(id+"F6.opPattern","COPY",BODY,{"derivedFrom":makeQuery(id+"F2.opExtrude","SWEPT_BODY",BODY,{"disambiguationData":[OSD([sQuery(id+"F0.wireOp",EDGE,"E7.right"),sQuery(id+"F0.wireOp",EDGE,"E8.bottom"),sQuery(id+"F0.wireOp",EDGE,"E8.top"),sQuery(id+"F0.wireOp",EDGE,"E8.right")])]}),"instanceName":"1"}),"instanceName":"1"});
            var Q49;
            Q49=makeQuery(id+"F8.opPattern","COPY",BODY,{"derivedFrom":makeQuery(id+"F6.opPattern","COPY",BODY,{"derivedFrom":makeQuery(id+"F3.opPattern","COPY",BODY,{"derivedFrom":makeQuery(id+"F1.opExtrude","SWEPT_BODY",BODY,{"disambiguationData":[OSD([sQuery(id+"F0.wireOp",EDGE,"E0.bottom"),sQuery(id+"F0.wireOp",EDGE,"E0.top"),sQuery(id+"F0.wireOp",EDGE,"E0.left"),sQuery(id+"F0.wireOp",EDGE,"E8.right")])]}),"instanceName":"1"}),"instanceName":"1"}),"instanceName":"1"});
            var Q50;
            Q50=makeQuery(id+"F8.opPattern","COPY",BODY,{"derivedFrom":makeQuery(id+"F6.opPattern","COPY",BODY,{"derivedFrom":makeQuery(id+"F3.opPattern","COPY",BODY,{"derivedFrom":makeQuery(id+"F1.opExtrude","SWEPT_BODY",BODY,{"disambiguationData":[OSD([sQuery(id+"F0.wireOp",EDGE,"E0.bottom"),sQuery(id+"F0.wireOp",EDGE,"E0.top"),sQuery(id+"F0.wireOp",EDGE,"E0.right"),sQuery(id+"F0.wireOp",EDGE,"E8.left")])]}),"instanceName":"1"}),"instanceName":"1"}),"instanceName":"1"});
            var Q51;
            Q51=makeQuery(id+"F8.opPattern","COPY",BODY,{"derivedFrom":makeQuery(id+"F6.opPattern","COPY",BODY,{"derivedFrom":makeQuery(id+"F3.opPattern","COPY",BODY,{"derivedFrom":makeQuery(id+"F1.opExtrude","SWEPT_BODY",BODY,{"disambiguationData":[OSD([sQuery(id+"F0.wireOp",EDGE,"E1.left"),sQuery(id+"F0.wireOp",EDGE,"E1.right"),sQuery(id+"F0.wireOp",EDGE,"E8.bottom"),sQuery(id+"F0.wireOp",EDGE,"E8.top")])]}),"instanceName":"1"}),"instanceName":"1"}),"instanceName":"1"});
            var Q52;
            Q52=makeQuery(id+"F8.opPattern","COPY",BODY,{"derivedFrom":makeQuery(id+"F6.opPattern","COPY",BODY,{"derivedFrom":makeQuery(id+"F3.opPattern","COPY",BODY,{"derivedFrom":makeQuery(id+"F1.opExtrude","SWEPT_BODY",BODY,{"disambiguationData":[OSD([sQuery(id+"F0.wireOp",EDGE,"E2.left"),sQuery(id+"F0.wireOp",EDGE,"E3.left"),sQuery(id+"F0.wireOp",EDGE,"E8.bottom"),sQuery(id+"F0.wireOp",EDGE,"E8.top")])]}),"instanceName":"1"}),"instanceName":"1"}),"instanceName":"1"});
            var Q53;
            Q53=makeQuery(id+"F8.opPattern","COPY",BODY,{"derivedFrom":makeQuery(id+"F6.opPattern","COPY",BODY,{"derivedFrom":makeQuery(id+"F3.opPattern","COPY",BODY,{"derivedFrom":makeQuery(id+"F1.opExtrude","SWEPT_BODY",BODY,{"disambiguationData":[OSD([sQuery(id+"F0.wireOp",EDGE,"E2.right"),sQuery(id+"F0.wireOp",EDGE,"E3.right"),sQuery(id+"F0.wireOp",EDGE,"E8.bottom"),sQuery(id+"F0.wireOp",EDGE,"E8.top")])]}),"instanceName":"1"}),"instanceName":"1"}),"instanceName":"1"});
            var Q54;
            Q54=makeQuery(id+"F8.opPattern","COPY",BODY,{"derivedFrom":makeQuery(id+"F6.opPattern","COPY",BODY,{"derivedFrom":makeQuery(id+"F3.opPattern","COPY",BODY,{"derivedFrom":makeQuery(id+"F1.opExtrude","SWEPT_BODY",BODY,{"disambiguationData":[OSD([sQuery(id+"F0.wireOp",EDGE,"E4.left"),sQuery(id+"F0.wireOp",EDGE,"E5.left"),sQuery(id+"F0.wireOp",EDGE,"E8.bottom"),sQuery(id+"F0.wireOp",EDGE,"E8.top")])]}),"instanceName":"1"}),"instanceName":"1"}),"instanceName":"1"});
            var Q55;
            Q55=makeQuery(id+"F8.opPattern","COPY",BODY,{"derivedFrom":makeQuery(id+"F6.opPattern","COPY",BODY,{"derivedFrom":makeQuery(id+"F3.opPattern","COPY",BODY,{"derivedFrom":makeQuery(id+"F1.opExtrude","SWEPT_BODY",BODY,{"disambiguationData":[OSD([sQuery(id+"F0.wireOp",EDGE,"E4.right"),sQuery(id+"F0.wireOp",EDGE,"E5.right"),sQuery(id+"F0.wireOp",EDGE,"E8.bottom"),sQuery(id+"F0.wireOp",EDGE,"E8.top")])]}),"instanceName":"1"}),"instanceName":"1"}),"instanceName":"1"});
            var Q56;
            Q56=makeQuery(id+"F8.opPattern","COPY",BODY,{"derivedFrom":makeQuery(id+"F6.opPattern","COPY",BODY,{"derivedFrom":makeQuery(id+"F3.opPattern","COPY",BODY,{"derivedFrom":makeQuery(id+"F1.opExtrude","SWEPT_BODY",BODY,{"disambiguationData":[OSD([sQuery(id+"F0.wireOp",EDGE,"E6.left"),sQuery(id+"F0.wireOp",EDGE,"E7.left"),sQuery(id+"F0.wireOp",EDGE,"E8.bottom"),sQuery(id+"F0.wireOp",EDGE,"E8.top")])]}),"instanceName":"1"}),"instanceName":"1"}),"instanceName":"1"});
            var Q57;
            Q57=makeQuery(id+"F8.opPattern","COPY",BODY,{"derivedFrom":makeQuery(id+"F6.opPattern","COPY",BODY,{"derivedFrom":makeQuery(id+"F3.opPattern","COPY",BODY,{"derivedFrom":makeQuery(id+"F1.opExtrude","SWEPT_BODY",BODY,{"disambiguationData":[OSD([sQuery(id+"F0.wireOp",EDGE,"E6.right"),sQuery(id+"F0.wireOp",EDGE,"E7.right"),sQuery(id+"F0.wireOp",EDGE,"E8.bottom"),sQuery(id+"F0.wireOp",EDGE,"E8.top")])]}),"instanceName":"1"}),"instanceName":"1"}),"instanceName":"1"});
            var Q58;
            Q58=makeQuery(id+"F8.opPattern","COPY",BODY,{"derivedFrom":makeQuery(id+"F6.opPattern","COPY",BODY,{"derivedFrom":makeQuery(id+"F3.opPattern","COPY",BODY,{"derivedFrom":makeQuery(id+"F2.opExtrude","SWEPT_BODY",BODY,{"disambiguationData":[OSD([sQuery(id+"F0.wireOp",EDGE,"E1.left"),sQuery(id+"F0.wireOp",EDGE,"E2.left"),sQuery(id+"F0.wireOp",EDGE,"E8.bottom"),sQuery(id+"F0.wireOp",EDGE,"E8.top")])]}),"instanceName":"1"}),"instanceName":"1"}),"instanceName":"1"});
            var Q59;
            Q59=makeQuery(id+"F8.opPattern","COPY",BODY,{"derivedFrom":makeQuery(id+"F6.opPattern","COPY",BODY,{"derivedFrom":makeQuery(id+"F3.opPattern","COPY",BODY,{"derivedFrom":makeQuery(id+"F2.opExtrude","SWEPT_BODY",BODY,{"disambiguationData":[OSD([sQuery(id+"F0.wireOp",EDGE,"E1.right"),sQuery(id+"F0.wireOp",EDGE,"E2.right"),sQuery(id+"F0.wireOp",EDGE,"E8.bottom"),sQuery(id+"F0.wireOp",EDGE,"E8.top")])]}),"instanceName":"1"}),"instanceName":"1"}),"instanceName":"1"});
            var Q60;
            Q60=makeQuery(id+"F8.opPattern","COPY",BODY,{"derivedFrom":makeQuery(id+"F6.opPattern","COPY",BODY,{"derivedFrom":makeQuery(id+"F3.opPattern","COPY",BODY,{"derivedFrom":makeQuery(id+"F2.opExtrude","SWEPT_BODY",BODY,{"disambiguationData":[OSD([sQuery(id+"F0.wireOp",EDGE,"E3.left"),sQuery(id+"F0.wireOp",EDGE,"E4.left"),sQuery(id+"F0.wireOp",EDGE,"E8.bottom"),sQuery(id+"F0.wireOp",EDGE,"E8.top")])]}),"instanceName":"1"}),"instanceName":"1"}),"instanceName":"1"});
            var Q61;
            Q61=makeQuery(id+"F8.opPattern","COPY",BODY,{"derivedFrom":makeQuery(id+"F6.opPattern","COPY",BODY,{"derivedFrom":makeQuery(id+"F3.opPattern","COPY",BODY,{"derivedFrom":makeQuery(id+"F2.opExtrude","SWEPT_BODY",BODY,{"disambiguationData":[OSD([sQuery(id+"F0.wireOp",EDGE,"E3.right"),sQuery(id+"F0.wireOp",EDGE,"E4.right"),sQuery(id+"F0.wireOp",EDGE,"E8.bottom"),sQuery(id+"F0.wireOp",EDGE,"E8.top")])]}),"instanceName":"1"}),"instanceName":"1"}),"instanceName":"1"});
            var Q62;
            Q62=makeQuery(id+"F8.opPattern","COPY",BODY,{"derivedFrom":makeQuery(id+"F6.opPattern","COPY",BODY,{"derivedFrom":makeQuery(id+"F3.opPattern","COPY",BODY,{"derivedFrom":makeQuery(id+"F2.opExtrude","SWEPT_BODY",BODY,{"disambiguationData":[OSD([sQuery(id+"F0.wireOp",EDGE,"E5.left"),sQuery(id+"F0.wireOp",EDGE,"E6.left"),sQuery(id+"F0.wireOp",EDGE,"E8.bottom"),sQuery(id+"F0.wireOp",EDGE,"E8.top")])]}),"instanceName":"1"}),"instanceName":"1"}),"instanceName":"1"});
            var Q63;
            Q63=makeQuery(id+"F8.opPattern","COPY",BODY,{"derivedFrom":makeQuery(id+"F6.opPattern","COPY",BODY,{"derivedFrom":makeQuery(id+"F3.opPattern","COPY",BODY,{"derivedFrom":makeQuery(id+"F2.opExtrude","SWEPT_BODY",BODY,{"disambiguationData":[OSD([sQuery(id+"F0.wireOp",EDGE,"E5.right"),sQuery(id+"F0.wireOp",EDGE,"E6.right"),sQuery(id+"F0.wireOp",EDGE,"E8.bottom"),sQuery(id+"F0.wireOp",EDGE,"E8.top")])]}),"instanceName":"1"}),"instanceName":"1"}),"instanceName":"1"});
            var Q64;
            Q64=makeQuery(id+"F8.opPattern","COPY",BODY,{"derivedFrom":makeQuery(id+"F6.opPattern","COPY",BODY,{"derivedFrom":makeQuery(id+"F3.opPattern","COPY",BODY,{"derivedFrom":makeQuery(id+"F2.opExtrude","SWEPT_BODY",BODY,{"disambiguationData":[OSD([sQuery(id+"F0.wireOp",EDGE,"E7.left"),sQuery(id+"F0.wireOp",EDGE,"E8.bottom"),sQuery(id+"F0.wireOp",EDGE,"E8.top"),sQuery(id+"F0.wireOp",EDGE,"E8.left")])]}),"instanceName":"1"}),"instanceName":"1"}),"instanceName":"1"});
            var Q65;
            Q65=makeQuery(id+"F8.opPattern","COPY",BODY,{"derivedFrom":makeQuery(id+"F6.opPattern","COPY",BODY,{"derivedFrom":makeQuery(id+"F3.opPattern","COPY",BODY,{"derivedFrom":makeQuery(id+"F2.opExtrude","SWEPT_BODY",BODY,{"disambiguationData":[OSD([sQuery(id+"F0.wireOp",EDGE,"E7.right"),sQuery(id+"F0.wireOp",EDGE,"E8.bottom"),sQuery(id+"F0.wireOp",EDGE,"E8.top"),sQuery(id+"F0.wireOp",EDGE,"E8.right")])]}),"instanceName":"1"}),"instanceName":"1"}),"instanceName":"1"});
            var Q66;
            Q66=makeQuery(id+"F8.opPattern","COPY",BODY,{"derivedFrom":makeQuery(id+"F6.opPattern","COPY",BODY,{"derivedFrom":makeQuery(id+"F1.opExtrude","SWEPT_BODY",BODY,{"disambiguationData":[OSD([sQuery(id+"F0.wireOp",EDGE,"E1.left"),sQuery(id+"F0.wireOp",EDGE,"E1.right"),sQuery(id+"F0.wireOp",EDGE,"E8.bottom"),sQuery(id+"F0.wireOp",EDGE,"E8.top")])]}),"instanceName":"1"}),"instanceName":"1"});
            var Q67;
            Q67=makeQuery(id+"F8.opPattern","COPY",BODY,{"derivedFrom":makeQuery(id+"F3.opPattern","COPY",BODY,{"derivedFrom":makeQuery(id+"F1.opExtrude","SWEPT_BODY",BODY,{"disambiguationData":[OSD([sQuery(id+"F0.wireOp",EDGE,"E1.left"),sQuery(id+"F0.wireOp",EDGE,"E1.right"),sQuery(id+"F0.wireOp",EDGE,"E8.bottom"),sQuery(id+"F0.wireOp",EDGE,"E8.top")])]}),"instanceName":"1"}),"instanceName":"1"});
            var Q68;
            Q68=sQuery(id+"F4.wireOp",EDGE,"E9");
            transform(context, id + "F9", {"entities" : qUnion([Q0, Q1, Q2, Q3, Q4, Q5, Q6, Q7, Q8, Q9, Q10, Q11, Q12, Q13, Q14, Q15, Q16, Q17, Q18, Q19, Q20, Q21, Q22, Q23, Q24, Q25, Q26, Q27, Q28, Q29, Q30, Q31, Q32, Q33, Q34, Q35, Q36, Q37, Q38, Q39, Q40, Q41, Q42, Q43, Q44, Q45, Q46, Q47, Q48, Q49, Q50, Q51, Q52, Q53, Q54, Q55, Q56, Q57, Q58, Q59, Q60, Q61, Q62, Q63, Q64, Q65, Q66, Q67]), "transformType" : TransformType.ROTATION, "transformAxis" : qUnion([Q68]), "angle" : 48 * degree, "makeCopy" : false});
        }
        {
            var Q0;
            Q0=makeQuery(id+"F8.opPattern","COPY",BODY,{"derivedFrom":makeQuery(id+"F6.opPattern","COPY",BODY,{"derivedFrom":makeQuery(id+"F1.opExtrude","SWEPT_BODY",BODY,{"disambiguationData":[OSD([sQuery(id+"F0.wireOp",EDGE,"E2.left"),sQuery(id+"F0.wireOp",EDGE,"E3.left"),sQuery(id+"F0.wireOp",EDGE,"E8.bottom"),sQuery(id+"F0.wireOp",EDGE,"E8.top")])]}),"instanceName":"1"}),"instanceName":"1"});
            var Q1;
            Q1=makeQuery(id+"F8.opPattern","COPY",BODY,{"derivedFrom":makeQuery(id+"F6.opPattern","COPY",BODY,{"derivedFrom":makeQuery(id+"F1.opExtrude","SWEPT_BODY",BODY,{"disambiguationData":[OSD([sQuery(id+"F0.wireOp",EDGE,"E6.left"),sQuery(id+"F0.wireOp",EDGE,"E7.left"),sQuery(id+"F0.wireOp",EDGE,"E8.bottom"),sQuery(id+"F0.wireOp",EDGE,"E8.top")])]}),"instanceName":"1"}),"instanceName":"1"});
            var Q2;
            Q2=makeQuery(id+"F8.opPattern","COPY",BODY,{"derivedFrom":makeQuery(id+"F3.opPattern","COPY",BODY,{"derivedFrom":makeQuery(id+"F1.opExtrude","SWEPT_BODY",BODY,{"disambiguationData":[OSD([sQuery(id+"F0.wireOp",EDGE,"E4.right"),sQuery(id+"F0.wireOp",EDGE,"E5.right"),sQuery(id+"F0.wireOp",EDGE,"E8.bottom"),sQuery(id+"F0.wireOp",EDGE,"E8.top")])]}),"instanceName":"1"}),"instanceName":"1"});
            var Q3;
            Q3=makeQuery(id+"F8.opPattern","COPY",BODY,{"derivedFrom":makeQuery(id+"F6.opPattern","COPY",BODY,{"derivedFrom":makeQuery(id+"F1.opExtrude","SWEPT_BODY",BODY,{"disambiguationData":[OSD([sQuery(id+"F0.wireOp",EDGE,"E1.left"),sQuery(id+"F0.wireOp",EDGE,"E1.right"),sQuery(id+"F0.wireOp",EDGE,"E8.bottom"),sQuery(id+"F0.wireOp",EDGE,"E8.top")])]}),"instanceName":"1"}),"instanceName":"1"});
            var Q4;
            Q4=makeQuery(id+"F8.opPattern","COPY",BODY,{"derivedFrom":makeQuery(id+"F6.opPattern","COPY",BODY,{"derivedFrom":makeQuery(id+"F1.opExtrude","SWEPT_BODY",BODY,{"disambiguationData":[OSD([sQuery(id+"F0.wireOp",EDGE,"E0.bottom"),sQuery(id+"F0.wireOp",EDGE,"E0.top"),sQuery(id+"F0.wireOp",EDGE,"E0.right"),sQuery(id+"F0.wireOp",EDGE,"E8.left")])]}),"instanceName":"1"}),"instanceName":"1"});
            var Q5;
            Q5=makeQuery(id+"F8.opPattern","COPY",BODY,{"derivedFrom":makeQuery(id+"F6.opPattern","COPY",BODY,{"derivedFrom":makeQuery(id+"F1.opExtrude","SWEPT_BODY",BODY,{"disambiguationData":[OSD([sQuery(id+"F0.wireOp",EDGE,"E0.bottom"),sQuery(id+"F0.wireOp",EDGE,"E0.top"),sQuery(id+"F0.wireOp",EDGE,"E0.left"),sQuery(id+"F0.wireOp",EDGE,"E8.right")])]}),"instanceName":"1"}),"instanceName":"1"});
            var Q6;
            Q6=makeQuery(id+"F8.opPattern","COPY",BODY,{"derivedFrom":makeQuery(id+"F3.opPattern","COPY",BODY,{"derivedFrom":makeQuery(id+"F2.opExtrude","SWEPT_BODY",BODY,{"disambiguationData":[OSD([sQuery(id+"F0.wireOp",EDGE,"E7.right"),sQuery(id+"F0.wireOp",EDGE,"E8.bottom"),sQuery(id+"F0.wireOp",EDGE,"E8.top"),sQuery(id+"F0.wireOp",EDGE,"E8.right")])]}),"instanceName":"1"}),"instanceName":"1"});
            var Q7;
            Q7=makeQuery(id+"F8.opPattern","COPY",BODY,{"derivedFrom":makeQuery(id+"F3.opPattern","COPY",BODY,{"derivedFrom":makeQuery(id+"F2.opExtrude","SWEPT_BODY",BODY,{"disambiguationData":[OSD([sQuery(id+"F0.wireOp",EDGE,"E7.left"),sQuery(id+"F0.wireOp",EDGE,"E8.bottom"),sQuery(id+"F0.wireOp",EDGE,"E8.top"),sQuery(id+"F0.wireOp",EDGE,"E8.left")])]}),"instanceName":"1"}),"instanceName":"1"});
            var Q8;
            Q8=makeQuery(id+"F8.opPattern","COPY",BODY,{"derivedFrom":makeQuery(id+"F3.opPattern","COPY",BODY,{"derivedFrom":makeQuery(id+"F2.opExtrude","SWEPT_BODY",BODY,{"disambiguationData":[OSD([sQuery(id+"F0.wireOp",EDGE,"E5.right"),sQuery(id+"F0.wireOp",EDGE,"E6.right"),sQuery(id+"F0.wireOp",EDGE,"E8.bottom"),sQuery(id+"F0.wireOp",EDGE,"E8.top")])]}),"instanceName":"1"}),"instanceName":"1"});
            var Q9;
            Q9=makeQuery(id+"F8.opPattern","COPY",BODY,{"derivedFrom":makeQuery(id+"F3.opPattern","COPY",BODY,{"derivedFrom":makeQuery(id+"F2.opExtrude","SWEPT_BODY",BODY,{"disambiguationData":[OSD([sQuery(id+"F0.wireOp",EDGE,"E5.left"),sQuery(id+"F0.wireOp",EDGE,"E6.left"),sQuery(id+"F0.wireOp",EDGE,"E8.bottom"),sQuery(id+"F0.wireOp",EDGE,"E8.top")])]}),"instanceName":"1"}),"instanceName":"1"});
            var Q10;
            Q10=makeQuery(id+"F8.opPattern","COPY",BODY,{"derivedFrom":makeQuery(id+"F3.opPattern","COPY",BODY,{"derivedFrom":makeQuery(id+"F2.opExtrude","SWEPT_BODY",BODY,{"disambiguationData":[OSD([sQuery(id+"F0.wireOp",EDGE,"E3.right"),sQuery(id+"F0.wireOp",EDGE,"E4.right"),sQuery(id+"F0.wireOp",EDGE,"E8.bottom"),sQuery(id+"F0.wireOp",EDGE,"E8.top")])]}),"instanceName":"1"}),"instanceName":"1"});
            var Q11;
            Q11=makeQuery(id+"F8.opPattern","COPY",BODY,{"derivedFrom":makeQuery(id+"F3.opPattern","COPY",BODY,{"derivedFrom":makeQuery(id+"F2.opExtrude","SWEPT_BODY",BODY,{"disambiguationData":[OSD([sQuery(id+"F0.wireOp",EDGE,"E3.left"),sQuery(id+"F0.wireOp",EDGE,"E4.left"),sQuery(id+"F0.wireOp",EDGE,"E8.bottom"),sQuery(id+"F0.wireOp",EDGE,"E8.top")])]}),"instanceName":"1"}),"instanceName":"1"});
            var Q12;
            Q12=makeQuery(id+"F8.opPattern","COPY",BODY,{"derivedFrom":makeQuery(id+"F3.opPattern","COPY",BODY,{"derivedFrom":makeQuery(id+"F2.opExtrude","SWEPT_BODY",BODY,{"disambiguationData":[OSD([sQuery(id+"F0.wireOp",EDGE,"E1.right"),sQuery(id+"F0.wireOp",EDGE,"E2.right"),sQuery(id+"F0.wireOp",EDGE,"E8.bottom"),sQuery(id+"F0.wireOp",EDGE,"E8.top")])]}),"instanceName":"1"}),"instanceName":"1"});
            var Q13;
            Q13=makeQuery(id+"F8.opPattern","COPY",BODY,{"derivedFrom":makeQuery(id+"F3.opPattern","COPY",BODY,{"derivedFrom":makeQuery(id+"F2.opExtrude","SWEPT_BODY",BODY,{"disambiguationData":[OSD([sQuery(id+"F0.wireOp",EDGE,"E1.left"),sQuery(id+"F0.wireOp",EDGE,"E2.left"),sQuery(id+"F0.wireOp",EDGE,"E8.bottom"),sQuery(id+"F0.wireOp",EDGE,"E8.top")])]}),"instanceName":"1"}),"instanceName":"1"});
            var Q14;
            Q14=makeQuery(id+"F8.opPattern","COPY",BODY,{"derivedFrom":makeQuery(id+"F3.opPattern","COPY",BODY,{"derivedFrom":makeQuery(id+"F1.opExtrude","SWEPT_BODY",BODY,{"disambiguationData":[OSD([sQuery(id+"F0.wireOp",EDGE,"E6.right"),sQuery(id+"F0.wireOp",EDGE,"E7.right"),sQuery(id+"F0.wireOp",EDGE,"E8.bottom"),sQuery(id+"F0.wireOp",EDGE,"E8.top")])]}),"instanceName":"1"}),"instanceName":"1"});
            var Q15;
            Q15=makeQuery(id+"F8.opPattern","COPY",BODY,{"derivedFrom":makeQuery(id+"F6.opPattern","COPY",BODY,{"derivedFrom":makeQuery(id+"F1.opExtrude","SWEPT_BODY",BODY,{"disambiguationData":[OSD([sQuery(id+"F0.wireOp",EDGE,"E4.right"),sQuery(id+"F0.wireOp",EDGE,"E5.right"),sQuery(id+"F0.wireOp",EDGE,"E8.bottom"),sQuery(id+"F0.wireOp",EDGE,"E8.top")])]}),"instanceName":"1"}),"instanceName":"1"});
            var Q16;
            Q16=makeQuery(id+"F8.opPattern","COPY",BODY,{"derivedFrom":makeQuery(id+"F6.opPattern","COPY",BODY,{"derivedFrom":makeQuery(id+"F1.opExtrude","SWEPT_BODY",BODY,{"disambiguationData":[OSD([sQuery(id+"F0.wireOp",EDGE,"E4.left"),sQuery(id+"F0.wireOp",EDGE,"E5.left"),sQuery(id+"F0.wireOp",EDGE,"E8.bottom"),sQuery(id+"F0.wireOp",EDGE,"E8.top")])]}),"instanceName":"1"}),"instanceName":"1"});
            var Q17;
            Q17=makeQuery(id+"F8.opPattern","COPY",BODY,{"derivedFrom":makeQuery(id+"F3.opPattern","COPY",BODY,{"derivedFrom":makeQuery(id+"F1.opExtrude","SWEPT_BODY",BODY,{"disambiguationData":[OSD([sQuery(id+"F0.wireOp",EDGE,"E4.left"),sQuery(id+"F0.wireOp",EDGE,"E5.left"),sQuery(id+"F0.wireOp",EDGE,"E8.bottom"),sQuery(id+"F0.wireOp",EDGE,"E8.top")])]}),"instanceName":"1"}),"instanceName":"1"});
            var Q18;
            Q18=makeQuery(id+"F8.opPattern","COPY",BODY,{"derivedFrom":makeQuery(id+"F3.opPattern","COPY",BODY,{"derivedFrom":makeQuery(id+"F1.opExtrude","SWEPT_BODY",BODY,{"disambiguationData":[OSD([sQuery(id+"F0.wireOp",EDGE,"E2.right"),sQuery(id+"F0.wireOp",EDGE,"E3.right"),sQuery(id+"F0.wireOp",EDGE,"E8.bottom"),sQuery(id+"F0.wireOp",EDGE,"E8.top")])]}),"instanceName":"1"}),"instanceName":"1"});
            var Q19;
            Q19=makeQuery(id+"F8.opPattern","COPY",BODY,{"derivedFrom":makeQuery(id+"F3.opPattern","COPY",BODY,{"derivedFrom":makeQuery(id+"F1.opExtrude","SWEPT_BODY",BODY,{"disambiguationData":[OSD([sQuery(id+"F0.wireOp",EDGE,"E2.left"),sQuery(id+"F0.wireOp",EDGE,"E3.left"),sQuery(id+"F0.wireOp",EDGE,"E8.bottom"),sQuery(id+"F0.wireOp",EDGE,"E8.top")])]}),"instanceName":"1"}),"instanceName":"1"});
            var Q20;
            Q20=makeQuery(id+"F8.opPattern","COPY",BODY,{"derivedFrom":makeQuery(id+"F3.opPattern","COPY",BODY,{"derivedFrom":makeQuery(id+"F1.opExtrude","SWEPT_BODY",BODY,{"disambiguationData":[OSD([sQuery(id+"F0.wireOp",EDGE,"E1.left"),sQuery(id+"F0.wireOp",EDGE,"E1.right"),sQuery(id+"F0.wireOp",EDGE,"E8.bottom"),sQuery(id+"F0.wireOp",EDGE,"E8.top")])]}),"instanceName":"1"}),"instanceName":"1"});
            var Q21;
            Q21=makeQuery(id+"F8.opPattern","COPY",BODY,{"derivedFrom":makeQuery(id+"F1.opExtrude","SWEPT_BODY",BODY,{"disambiguationData":[OSD([sQuery(id+"F0.wireOp",EDGE,"E0.bottom"),sQuery(id+"F0.wireOp",EDGE,"E0.top"),sQuery(id+"F0.wireOp",EDGE,"E0.left"),sQuery(id+"F0.wireOp",EDGE,"E8.right")])]}),"instanceName":"1"});
            var Q22;
            Q22=makeQuery(id+"F8.opPattern","COPY",BODY,{"derivedFrom":makeQuery(id+"F1.opExtrude","SWEPT_BODY",BODY,{"disambiguationData":[OSD([sQuery(id+"F0.wireOp",EDGE,"E0.bottom"),sQuery(id+"F0.wireOp",EDGE,"E0.top"),sQuery(id+"F0.wireOp",EDGE,"E0.right"),sQuery(id+"F0.wireOp",EDGE,"E8.left")])]}),"instanceName":"1"});
            var Q23;
            Q23=makeQuery(id+"F8.opPattern","COPY",BODY,{"derivedFrom":makeQuery(id+"F1.opExtrude","SWEPT_BODY",BODY,{"disambiguationData":[OSD([sQuery(id+"F0.wireOp",EDGE,"E1.left"),sQuery(id+"F0.wireOp",EDGE,"E1.right"),sQuery(id+"F0.wireOp",EDGE,"E8.bottom"),sQuery(id+"F0.wireOp",EDGE,"E8.top")])]}),"instanceName":"1"});
            var Q24;
            Q24=makeQuery(id+"F8.opPattern","COPY",BODY,{"derivedFrom":makeQuery(id+"F1.opExtrude","SWEPT_BODY",BODY,{"disambiguationData":[OSD([sQuery(id+"F0.wireOp",EDGE,"E2.left"),sQuery(id+"F0.wireOp",EDGE,"E3.left"),sQuery(id+"F0.wireOp",EDGE,"E8.bottom"),sQuery(id+"F0.wireOp",EDGE,"E8.top")])]}),"instanceName":"1"});
            var Q25;
            Q25=makeQuery(id+"F8.opPattern","COPY",BODY,{"derivedFrom":makeQuery(id+"F1.opExtrude","SWEPT_BODY",BODY,{"disambiguationData":[OSD([sQuery(id+"F0.wireOp",EDGE,"E2.right"),sQuery(id+"F0.wireOp",EDGE,"E3.right"),sQuery(id+"F0.wireOp",EDGE,"E8.bottom"),sQuery(id+"F0.wireOp",EDGE,"E8.top")])]}),"instanceName":"1"});
            var Q26;
            Q26=makeQuery(id+"F8.opPattern","COPY",BODY,{"derivedFrom":makeQuery(id+"F1.opExtrude","SWEPT_BODY",BODY,{"disambiguationData":[OSD([sQuery(id+"F0.wireOp",EDGE,"E4.right"),sQuery(id+"F0.wireOp",EDGE,"E5.right"),sQuery(id+"F0.wireOp",EDGE,"E8.bottom"),sQuery(id+"F0.wireOp",EDGE,"E8.top")])]}),"instanceName":"1"});
            var Q27;
            Q27=makeQuery(id+"F8.opPattern","COPY",BODY,{"derivedFrom":makeQuery(id+"F1.opExtrude","SWEPT_BODY",BODY,{"disambiguationData":[OSD([sQuery(id+"F0.wireOp",EDGE,"E4.left"),sQuery(id+"F0.wireOp",EDGE,"E5.left"),sQuery(id+"F0.wireOp",EDGE,"E8.bottom"),sQuery(id+"F0.wireOp",EDGE,"E8.top")])]}),"instanceName":"1"});
            var Q28;
            Q28=makeQuery(id+"F8.opPattern","COPY",BODY,{"derivedFrom":makeQuery(id+"F1.opExtrude","SWEPT_BODY",BODY,{"disambiguationData":[OSD([sQuery(id+"F0.wireOp",EDGE,"E6.left"),sQuery(id+"F0.wireOp",EDGE,"E7.left"),sQuery(id+"F0.wireOp",EDGE,"E8.bottom"),sQuery(id+"F0.wireOp",EDGE,"E8.top")])]}),"instanceName":"1"});
            var Q29;
            Q29=makeQuery(id+"F8.opPattern","COPY",BODY,{"derivedFrom":makeQuery(id+"F1.opExtrude","SWEPT_BODY",BODY,{"disambiguationData":[OSD([sQuery(id+"F0.wireOp",EDGE,"E6.right"),sQuery(id+"F0.wireOp",EDGE,"E7.right"),sQuery(id+"F0.wireOp",EDGE,"E8.bottom"),sQuery(id+"F0.wireOp",EDGE,"E8.top")])]}),"instanceName":"1"});
            var Q30;
            Q30=makeQuery(id+"F8.opPattern","COPY",BODY,{"derivedFrom":makeQuery(id+"F2.opExtrude","SWEPT_BODY",BODY,{"disambiguationData":[OSD([sQuery(id+"F0.wireOp",EDGE,"E1.left"),sQuery(id+"F0.wireOp",EDGE,"E2.left"),sQuery(id+"F0.wireOp",EDGE,"E8.bottom"),sQuery(id+"F0.wireOp",EDGE,"E8.top")])]}),"instanceName":"1"});
            var Q31;
            Q31=makeQuery(id+"F8.opPattern","COPY",BODY,{"derivedFrom":makeQuery(id+"F2.opExtrude","SWEPT_BODY",BODY,{"disambiguationData":[OSD([sQuery(id+"F0.wireOp",EDGE,"E1.right"),sQuery(id+"F0.wireOp",EDGE,"E2.right"),sQuery(id+"F0.wireOp",EDGE,"E8.bottom"),sQuery(id+"F0.wireOp",EDGE,"E8.top")])]}),"instanceName":"1"});
            var Q32;
            Q32=makeQuery(id+"F8.opPattern","COPY",BODY,{"derivedFrom":makeQuery(id+"F2.opExtrude","SWEPT_BODY",BODY,{"disambiguationData":[OSD([sQuery(id+"F0.wireOp",EDGE,"E3.left"),sQuery(id+"F0.wireOp",EDGE,"E4.left"),sQuery(id+"F0.wireOp",EDGE,"E8.bottom"),sQuery(id+"F0.wireOp",EDGE,"E8.top")])]}),"instanceName":"1"});
            var Q33;
            Q33=makeQuery(id+"F8.opPattern","COPY",BODY,{"derivedFrom":makeQuery(id+"F2.opExtrude","SWEPT_BODY",BODY,{"disambiguationData":[OSD([sQuery(id+"F0.wireOp",EDGE,"E3.right"),sQuery(id+"F0.wireOp",EDGE,"E4.right"),sQuery(id+"F0.wireOp",EDGE,"E8.bottom"),sQuery(id+"F0.wireOp",EDGE,"E8.top")])]}),"instanceName":"1"});
            var Q34;
            Q34=makeQuery(id+"F8.opPattern","COPY",BODY,{"derivedFrom":makeQuery(id+"F2.opExtrude","SWEPT_BODY",BODY,{"disambiguationData":[OSD([sQuery(id+"F0.wireOp",EDGE,"E5.left"),sQuery(id+"F0.wireOp",EDGE,"E6.left"),sQuery(id+"F0.wireOp",EDGE,"E8.bottom"),sQuery(id+"F0.wireOp",EDGE,"E8.top")])]}),"instanceName":"1"});
            var Q35;
            Q35=makeQuery(id+"F8.opPattern","COPY",BODY,{"derivedFrom":makeQuery(id+"F2.opExtrude","SWEPT_BODY",BODY,{"disambiguationData":[OSD([sQuery(id+"F0.wireOp",EDGE,"E5.right"),sQuery(id+"F0.wireOp",EDGE,"E6.right"),sQuery(id+"F0.wireOp",EDGE,"E8.bottom"),sQuery(id+"F0.wireOp",EDGE,"E8.top")])]}),"instanceName":"1"});
            var Q36;
            Q36=makeQuery(id+"F8.opPattern","COPY",BODY,{"derivedFrom":makeQuery(id+"F2.opExtrude","SWEPT_BODY",BODY,{"disambiguationData":[OSD([sQuery(id+"F0.wireOp",EDGE,"E7.left"),sQuery(id+"F0.wireOp",EDGE,"E8.bottom"),sQuery(id+"F0.wireOp",EDGE,"E8.top"),sQuery(id+"F0.wireOp",EDGE,"E8.left")])]}),"instanceName":"1"});
            var Q37;
            Q37=makeQuery(id+"F8.opPattern","COPY",BODY,{"derivedFrom":makeQuery(id+"F2.opExtrude","SWEPT_BODY",BODY,{"disambiguationData":[OSD([sQuery(id+"F0.wireOp",EDGE,"E7.right"),sQuery(id+"F0.wireOp",EDGE,"E8.bottom"),sQuery(id+"F0.wireOp",EDGE,"E8.top"),sQuery(id+"F0.wireOp",EDGE,"E8.right")])]}),"instanceName":"1"});
            var Q38;
            Q38=makeQuery(id+"F8.opPattern","COPY",BODY,{"derivedFrom":makeQuery(id+"F3.opPattern","COPY",BODY,{"derivedFrom":makeQuery(id+"F1.opExtrude","SWEPT_BODY",BODY,{"disambiguationData":[OSD([sQuery(id+"F0.wireOp",EDGE,"E0.bottom"),sQuery(id+"F0.wireOp",EDGE,"E0.top"),sQuery(id+"F0.wireOp",EDGE,"E0.left"),sQuery(id+"F0.wireOp",EDGE,"E8.right")])]}),"instanceName":"1"}),"instanceName":"1"});
            var Q39;
            Q39=makeQuery(id+"F8.opPattern","COPY",BODY,{"derivedFrom":makeQuery(id+"F3.opPattern","COPY",BODY,{"derivedFrom":makeQuery(id+"F1.opExtrude","SWEPT_BODY",BODY,{"disambiguationData":[OSD([sQuery(id+"F0.wireOp",EDGE,"E0.bottom"),sQuery(id+"F0.wireOp",EDGE,"E0.top"),sQuery(id+"F0.wireOp",EDGE,"E0.right"),sQuery(id+"F0.wireOp",EDGE,"E8.left")])]}),"instanceName":"1"}),"instanceName":"1"});
            var Q40;
            Q40=makeQuery(id+"F8.opPattern","COPY",BODY,{"derivedFrom":makeQuery(id+"F3.opPattern","COPY",BODY,{"derivedFrom":makeQuery(id+"F1.opExtrude","SWEPT_BODY",BODY,{"disambiguationData":[OSD([sQuery(id+"F0.wireOp",EDGE,"E6.left"),sQuery(id+"F0.wireOp",EDGE,"E7.left"),sQuery(id+"F0.wireOp",EDGE,"E8.bottom"),sQuery(id+"F0.wireOp",EDGE,"E8.top")])]}),"instanceName":"1"}),"instanceName":"1"});
            var Q41;
            Q41=makeQuery(id+"F8.opPattern","COPY",BODY,{"derivedFrom":makeQuery(id+"F6.opPattern","COPY",BODY,{"derivedFrom":makeQuery(id+"F1.opExtrude","SWEPT_BODY",BODY,{"disambiguationData":[OSD([sQuery(id+"F0.wireOp",EDGE,"E2.right"),sQuery(id+"F0.wireOp",EDGE,"E3.right"),sQuery(id+"F0.wireOp",EDGE,"E8.bottom"),sQuery(id+"F0.wireOp",EDGE,"E8.top")])]}),"instanceName":"1"}),"instanceName":"1"});
            var Q42;
            Q42=makeQuery(id+"F8.opPattern","COPY",BODY,{"derivedFrom":makeQuery(id+"F6.opPattern","COPY",BODY,{"derivedFrom":makeQuery(id+"F2.opExtrude","SWEPT_BODY",BODY,{"disambiguationData":[OSD([sQuery(id+"F0.wireOp",EDGE,"E1.left"),sQuery(id+"F0.wireOp",EDGE,"E2.left"),sQuery(id+"F0.wireOp",EDGE,"E8.bottom"),sQuery(id+"F0.wireOp",EDGE,"E8.top")])]}),"instanceName":"1"}),"instanceName":"1"});
            var Q43;
            Q43=makeQuery(id+"F8.opPattern","COPY",BODY,{"derivedFrom":makeQuery(id+"F6.opPattern","COPY",BODY,{"derivedFrom":makeQuery(id+"F1.opExtrude","SWEPT_BODY",BODY,{"disambiguationData":[OSD([sQuery(id+"F0.wireOp",EDGE,"E6.right"),sQuery(id+"F0.wireOp",EDGE,"E7.right"),sQuery(id+"F0.wireOp",EDGE,"E8.bottom"),sQuery(id+"F0.wireOp",EDGE,"E8.top")])]}),"instanceName":"1"}),"instanceName":"1"});
            var Q44;
            Q44=makeQuery(id+"F8.opPattern","COPY",BODY,{"derivedFrom":makeQuery(id+"F6.opPattern","COPY",BODY,{"derivedFrom":makeQuery(id+"F2.opExtrude","SWEPT_BODY",BODY,{"disambiguationData":[OSD([sQuery(id+"F0.wireOp",EDGE,"E1.right"),sQuery(id+"F0.wireOp",EDGE,"E2.right"),sQuery(id+"F0.wireOp",EDGE,"E8.bottom"),sQuery(id+"F0.wireOp",EDGE,"E8.top")])]}),"instanceName":"1"}),"instanceName":"1"});
            var Q45;
            Q45=makeQuery(id+"F8.opPattern","COPY",BODY,{"derivedFrom":makeQuery(id+"F6.opPattern","COPY",BODY,{"derivedFrom":makeQuery(id+"F2.opExtrude","SWEPT_BODY",BODY,{"disambiguationData":[OSD([sQuery(id+"F0.wireOp",EDGE,"E3.left"),sQuery(id+"F0.wireOp",EDGE,"E4.left"),sQuery(id+"F0.wireOp",EDGE,"E8.bottom"),sQuery(id+"F0.wireOp",EDGE,"E8.top")])]}),"instanceName":"1"}),"instanceName":"1"});
            var Q46;
            Q46=makeQuery(id+"F8.opPattern","COPY",BODY,{"derivedFrom":makeQuery(id+"F6.opPattern","COPY",BODY,{"derivedFrom":makeQuery(id+"F2.opExtrude","SWEPT_BODY",BODY,{"disambiguationData":[OSD([sQuery(id+"F0.wireOp",EDGE,"E3.right"),sQuery(id+"F0.wireOp",EDGE,"E4.right"),sQuery(id+"F0.wireOp",EDGE,"E8.bottom"),sQuery(id+"F0.wireOp",EDGE,"E8.top")])]}),"instanceName":"1"}),"instanceName":"1"});
            var Q47;
            Q47=makeQuery(id+"F8.opPattern","COPY",BODY,{"derivedFrom":makeQuery(id+"F6.opPattern","COPY",BODY,{"derivedFrom":makeQuery(id+"F2.opExtrude","SWEPT_BODY",BODY,{"disambiguationData":[OSD([sQuery(id+"F0.wireOp",EDGE,"E5.left"),sQuery(id+"F0.wireOp",EDGE,"E6.left"),sQuery(id+"F0.wireOp",EDGE,"E8.bottom"),sQuery(id+"F0.wireOp",EDGE,"E8.top")])]}),"instanceName":"1"}),"instanceName":"1"});
            var Q48;
            Q48=makeQuery(id+"F8.opPattern","COPY",BODY,{"derivedFrom":makeQuery(id+"F6.opPattern","COPY",BODY,{"derivedFrom":makeQuery(id+"F2.opExtrude","SWEPT_BODY",BODY,{"disambiguationData":[OSD([sQuery(id+"F0.wireOp",EDGE,"E5.right"),sQuery(id+"F0.wireOp",EDGE,"E6.right"),sQuery(id+"F0.wireOp",EDGE,"E8.bottom"),sQuery(id+"F0.wireOp",EDGE,"E8.top")])]}),"instanceName":"1"}),"instanceName":"1"});
            var Q49;
            Q49=makeQuery(id+"F8.opPattern","COPY",BODY,{"derivedFrom":makeQuery(id+"F6.opPattern","COPY",BODY,{"derivedFrom":makeQuery(id+"F2.opExtrude","SWEPT_BODY",BODY,{"disambiguationData":[OSD([sQuery(id+"F0.wireOp",EDGE,"E7.left"),sQuery(id+"F0.wireOp",EDGE,"E8.bottom"),sQuery(id+"F0.wireOp",EDGE,"E8.top"),sQuery(id+"F0.wireOp",EDGE,"E8.left")])]}),"instanceName":"1"}),"instanceName":"1"});
            var Q50;
            Q50=makeQuery(id+"F8.opPattern","COPY",BODY,{"derivedFrom":makeQuery(id+"F6.opPattern","COPY",BODY,{"derivedFrom":makeQuery(id+"F2.opExtrude","SWEPT_BODY",BODY,{"disambiguationData":[OSD([sQuery(id+"F0.wireOp",EDGE,"E7.right"),sQuery(id+"F0.wireOp",EDGE,"E8.bottom"),sQuery(id+"F0.wireOp",EDGE,"E8.top"),sQuery(id+"F0.wireOp",EDGE,"E8.right")])]}),"instanceName":"1"}),"instanceName":"1"});
            var Q51;
            Q51=makeQuery(id+"F8.opPattern","COPY",BODY,{"derivedFrom":makeQuery(id+"F6.opPattern","COPY",BODY,{"derivedFrom":makeQuery(id+"F3.opPattern","COPY",BODY,{"derivedFrom":makeQuery(id+"F1.opExtrude","SWEPT_BODY",BODY,{"disambiguationData":[OSD([sQuery(id+"F0.wireOp",EDGE,"E0.bottom"),sQuery(id+"F0.wireOp",EDGE,"E0.top"),sQuery(id+"F0.wireOp",EDGE,"E0.left"),sQuery(id+"F0.wireOp",EDGE,"E8.right")])]}),"instanceName":"1"}),"instanceName":"1"}),"instanceName":"1"});
            var Q52;
            Q52=makeQuery(id+"F8.opPattern","COPY",BODY,{"derivedFrom":makeQuery(id+"F6.opPattern","COPY",BODY,{"derivedFrom":makeQuery(id+"F3.opPattern","COPY",BODY,{"derivedFrom":makeQuery(id+"F1.opExtrude","SWEPT_BODY",BODY,{"disambiguationData":[OSD([sQuery(id+"F0.wireOp",EDGE,"E0.bottom"),sQuery(id+"F0.wireOp",EDGE,"E0.top"),sQuery(id+"F0.wireOp",EDGE,"E0.right"),sQuery(id+"F0.wireOp",EDGE,"E8.left")])]}),"instanceName":"1"}),"instanceName":"1"}),"instanceName":"1"});
            var Q53;
            Q53=makeQuery(id+"F8.opPattern","COPY",BODY,{"derivedFrom":makeQuery(id+"F6.opPattern","COPY",BODY,{"derivedFrom":makeQuery(id+"F3.opPattern","COPY",BODY,{"derivedFrom":makeQuery(id+"F1.opExtrude","SWEPT_BODY",BODY,{"disambiguationData":[OSD([sQuery(id+"F0.wireOp",EDGE,"E1.left"),sQuery(id+"F0.wireOp",EDGE,"E1.right"),sQuery(id+"F0.wireOp",EDGE,"E8.bottom"),sQuery(id+"F0.wireOp",EDGE,"E8.top")])]}),"instanceName":"1"}),"instanceName":"1"}),"instanceName":"1"});
            var Q54;
            Q54=makeQuery(id+"F8.opPattern","COPY",BODY,{"derivedFrom":makeQuery(id+"F6.opPattern","COPY",BODY,{"derivedFrom":makeQuery(id+"F3.opPattern","COPY",BODY,{"derivedFrom":makeQuery(id+"F1.opExtrude","SWEPT_BODY",BODY,{"disambiguationData":[OSD([sQuery(id+"F0.wireOp",EDGE,"E2.left"),sQuery(id+"F0.wireOp",EDGE,"E3.left"),sQuery(id+"F0.wireOp",EDGE,"E8.bottom"),sQuery(id+"F0.wireOp",EDGE,"E8.top")])]}),"instanceName":"1"}),"instanceName":"1"}),"instanceName":"1"});
            var Q55;
            Q55=makeQuery(id+"F8.opPattern","COPY",BODY,{"derivedFrom":makeQuery(id+"F6.opPattern","COPY",BODY,{"derivedFrom":makeQuery(id+"F3.opPattern","COPY",BODY,{"derivedFrom":makeQuery(id+"F1.opExtrude","SWEPT_BODY",BODY,{"disambiguationData":[OSD([sQuery(id+"F0.wireOp",EDGE,"E2.right"),sQuery(id+"F0.wireOp",EDGE,"E3.right"),sQuery(id+"F0.wireOp",EDGE,"E8.bottom"),sQuery(id+"F0.wireOp",EDGE,"E8.top")])]}),"instanceName":"1"}),"instanceName":"1"}),"instanceName":"1"});
            var Q56;
            Q56=makeQuery(id+"F8.opPattern","COPY",BODY,{"derivedFrom":makeQuery(id+"F6.opPattern","COPY",BODY,{"derivedFrom":makeQuery(id+"F3.opPattern","COPY",BODY,{"derivedFrom":makeQuery(id+"F1.opExtrude","SWEPT_BODY",BODY,{"disambiguationData":[OSD([sQuery(id+"F0.wireOp",EDGE,"E4.left"),sQuery(id+"F0.wireOp",EDGE,"E5.left"),sQuery(id+"F0.wireOp",EDGE,"E8.bottom"),sQuery(id+"F0.wireOp",EDGE,"E8.top")])]}),"instanceName":"1"}),"instanceName":"1"}),"instanceName":"1"});
            var Q57;
            Q57=makeQuery(id+"F8.opPattern","COPY",BODY,{"derivedFrom":makeQuery(id+"F6.opPattern","COPY",BODY,{"derivedFrom":makeQuery(id+"F3.opPattern","COPY",BODY,{"derivedFrom":makeQuery(id+"F1.opExtrude","SWEPT_BODY",BODY,{"disambiguationData":[OSD([sQuery(id+"F0.wireOp",EDGE,"E4.right"),sQuery(id+"F0.wireOp",EDGE,"E5.right"),sQuery(id+"F0.wireOp",EDGE,"E8.bottom"),sQuery(id+"F0.wireOp",EDGE,"E8.top")])]}),"instanceName":"1"}),"instanceName":"1"}),"instanceName":"1"});
            var Q58;
            Q58=makeQuery(id+"F8.opPattern","COPY",BODY,{"derivedFrom":makeQuery(id+"F6.opPattern","COPY",BODY,{"derivedFrom":makeQuery(id+"F3.opPattern","COPY",BODY,{"derivedFrom":makeQuery(id+"F1.opExtrude","SWEPT_BODY",BODY,{"disambiguationData":[OSD([sQuery(id+"F0.wireOp",EDGE,"E6.left"),sQuery(id+"F0.wireOp",EDGE,"E7.left"),sQuery(id+"F0.wireOp",EDGE,"E8.bottom"),sQuery(id+"F0.wireOp",EDGE,"E8.top")])]}),"instanceName":"1"}),"instanceName":"1"}),"instanceName":"1"});
            var Q59;
            Q59=makeQuery(id+"F8.opPattern","COPY",BODY,{"derivedFrom":makeQuery(id+"F6.opPattern","COPY",BODY,{"derivedFrom":makeQuery(id+"F3.opPattern","COPY",BODY,{"derivedFrom":makeQuery(id+"F1.opExtrude","SWEPT_BODY",BODY,{"disambiguationData":[OSD([sQuery(id+"F0.wireOp",EDGE,"E6.right"),sQuery(id+"F0.wireOp",EDGE,"E7.right"),sQuery(id+"F0.wireOp",EDGE,"E8.bottom"),sQuery(id+"F0.wireOp",EDGE,"E8.top")])]}),"instanceName":"1"}),"instanceName":"1"}),"instanceName":"1"});
            var Q60;
            Q60=makeQuery(id+"F8.opPattern","COPY",BODY,{"derivedFrom":makeQuery(id+"F6.opPattern","COPY",BODY,{"derivedFrom":makeQuery(id+"F3.opPattern","COPY",BODY,{"derivedFrom":makeQuery(id+"F2.opExtrude","SWEPT_BODY",BODY,{"disambiguationData":[OSD([sQuery(id+"F0.wireOp",EDGE,"E1.left"),sQuery(id+"F0.wireOp",EDGE,"E2.left"),sQuery(id+"F0.wireOp",EDGE,"E8.bottom"),sQuery(id+"F0.wireOp",EDGE,"E8.top")])]}),"instanceName":"1"}),"instanceName":"1"}),"instanceName":"1"});
            var Q61;
            Q61=makeQuery(id+"F8.opPattern","COPY",BODY,{"derivedFrom":makeQuery(id+"F6.opPattern","COPY",BODY,{"derivedFrom":makeQuery(id+"F3.opPattern","COPY",BODY,{"derivedFrom":makeQuery(id+"F2.opExtrude","SWEPT_BODY",BODY,{"disambiguationData":[OSD([sQuery(id+"F0.wireOp",EDGE,"E1.right"),sQuery(id+"F0.wireOp",EDGE,"E2.right"),sQuery(id+"F0.wireOp",EDGE,"E8.bottom"),sQuery(id+"F0.wireOp",EDGE,"E8.top")])]}),"instanceName":"1"}),"instanceName":"1"}),"instanceName":"1"});
            var Q62;
            Q62=makeQuery(id+"F8.opPattern","COPY",BODY,{"derivedFrom":makeQuery(id+"F6.opPattern","COPY",BODY,{"derivedFrom":makeQuery(id+"F3.opPattern","COPY",BODY,{"derivedFrom":makeQuery(id+"F2.opExtrude","SWEPT_BODY",BODY,{"disambiguationData":[OSD([sQuery(id+"F0.wireOp",EDGE,"E3.left"),sQuery(id+"F0.wireOp",EDGE,"E4.left"),sQuery(id+"F0.wireOp",EDGE,"E8.bottom"),sQuery(id+"F0.wireOp",EDGE,"E8.top")])]}),"instanceName":"1"}),"instanceName":"1"}),"instanceName":"1"});
            var Q63;
            Q63=makeQuery(id+"F8.opPattern","COPY",BODY,{"derivedFrom":makeQuery(id+"F6.opPattern","COPY",BODY,{"derivedFrom":makeQuery(id+"F3.opPattern","COPY",BODY,{"derivedFrom":makeQuery(id+"F2.opExtrude","SWEPT_BODY",BODY,{"disambiguationData":[OSD([sQuery(id+"F0.wireOp",EDGE,"E3.right"),sQuery(id+"F0.wireOp",EDGE,"E4.right"),sQuery(id+"F0.wireOp",EDGE,"E8.bottom"),sQuery(id+"F0.wireOp",EDGE,"E8.top")])]}),"instanceName":"1"}),"instanceName":"1"}),"instanceName":"1"});
            var Q64;
            Q64=makeQuery(id+"F8.opPattern","COPY",BODY,{"derivedFrom":makeQuery(id+"F6.opPattern","COPY",BODY,{"derivedFrom":makeQuery(id+"F3.opPattern","COPY",BODY,{"derivedFrom":makeQuery(id+"F2.opExtrude","SWEPT_BODY",BODY,{"disambiguationData":[OSD([sQuery(id+"F0.wireOp",EDGE,"E5.left"),sQuery(id+"F0.wireOp",EDGE,"E6.left"),sQuery(id+"F0.wireOp",EDGE,"E8.bottom"),sQuery(id+"F0.wireOp",EDGE,"E8.top")])]}),"instanceName":"1"}),"instanceName":"1"}),"instanceName":"1"});
            var Q65;
            Q65=makeQuery(id+"F8.opPattern","COPY",BODY,{"derivedFrom":makeQuery(id+"F6.opPattern","COPY",BODY,{"derivedFrom":makeQuery(id+"F3.opPattern","COPY",BODY,{"derivedFrom":makeQuery(id+"F2.opExtrude","SWEPT_BODY",BODY,{"disambiguationData":[OSD([sQuery(id+"F0.wireOp",EDGE,"E5.right"),sQuery(id+"F0.wireOp",EDGE,"E6.right"),sQuery(id+"F0.wireOp",EDGE,"E8.bottom"),sQuery(id+"F0.wireOp",EDGE,"E8.top")])]}),"instanceName":"1"}),"instanceName":"1"}),"instanceName":"1"});
            var Q66;
            Q66=makeQuery(id+"F8.opPattern","COPY",BODY,{"derivedFrom":makeQuery(id+"F6.opPattern","COPY",BODY,{"derivedFrom":makeQuery(id+"F3.opPattern","COPY",BODY,{"derivedFrom":makeQuery(id+"F2.opExtrude","SWEPT_BODY",BODY,{"disambiguationData":[OSD([sQuery(id+"F0.wireOp",EDGE,"E7.left"),sQuery(id+"F0.wireOp",EDGE,"E8.bottom"),sQuery(id+"F0.wireOp",EDGE,"E8.top"),sQuery(id+"F0.wireOp",EDGE,"E8.left")])]}),"instanceName":"1"}),"instanceName":"1"}),"instanceName":"1"});
            var Q67;
            Q67=makeQuery(id+"F8.opPattern","COPY",BODY,{"derivedFrom":makeQuery(id+"F6.opPattern","COPY",BODY,{"derivedFrom":makeQuery(id+"F3.opPattern","COPY",BODY,{"derivedFrom":makeQuery(id+"F2.opExtrude","SWEPT_BODY",BODY,{"disambiguationData":[OSD([sQuery(id+"F0.wireOp",EDGE,"E7.right"),sQuery(id+"F0.wireOp",EDGE,"E8.bottom"),sQuery(id+"F0.wireOp",EDGE,"E8.top"),sQuery(id+"F0.wireOp",EDGE,"E8.right")])]}),"instanceName":"1"}),"instanceName":"1"}),"instanceName":"1"});
            transform(context, id + "F10", {"entities" : qUnion([Q0, Q1, Q2, Q3, Q4, Q5, Q6, Q7, Q8, Q9, Q10, Q11, Q12, Q13, Q14, Q15, Q16, Q17, Q18, Q19, Q20, Q21, Q22, Q23, Q24, Q25, Q26, Q27, Q28, Q29, Q30, Q31, Q32, Q33, Q34, Q35, Q36, Q37, Q38, Q39, Q40, Q41, Q42, Q43, Q44, Q45, Q46, Q47, Q48, Q49, Q50, Q51, Q52, Q53, Q54, Q55, Q56, Q57, Q58, Q59, Q60, Q61, Q62, Q63, Q64, Q65, Q66, Q67]), "transformType" : TransformType.TRANSLATION_3D, "dx" : 0 * mm, "dy" : 0 * mm, "dz" : 25.4 * mm, "makeCopy" : true});
        }
        {
            var Q0;
            Q0=makeQuery(id+"F10.opPattern","COPY",BODY,{"derivedFrom":makeQuery(id+"F8.opPattern","COPY",BODY,{"derivedFrom":makeQuery(id+"F3.opPattern","COPY",BODY,{"derivedFrom":makeQuery(id+"F2.opExtrude","SWEPT_BODY",BODY,{"disambiguationData":[OSD([sQuery(id+"F0.wireOp",EDGE,"E5.left"),sQuery(id+"F0.wireOp",EDGE,"E6.left"),sQuery(id+"F0.wireOp",EDGE,"E8.bottom"),sQuery(id+"F0.wireOp",EDGE,"E8.top")])]}),"instanceName":"1"}),"instanceName":"1"}),"instanceName":"1"});
            var Q1;
            Q1=makeQuery(id+"F10.opPattern","COPY",BODY,{"derivedFrom":makeQuery(id+"F8.opPattern","COPY",BODY,{"derivedFrom":makeQuery(id+"F6.opPattern","COPY",BODY,{"derivedFrom":makeQuery(id+"F1.opExtrude","SWEPT_BODY",BODY,{"disambiguationData":[OSD([sQuery(id+"F0.wireOp",EDGE,"E0.bottom"),sQuery(id+"F0.wireOp",EDGE,"E0.top"),sQuery(id+"F0.wireOp",EDGE,"E0.left"),sQuery(id+"F0.wireOp",EDGE,"E8.right")])]}),"instanceName":"1"}),"instanceName":"1"}),"instanceName":"1"});
            var Q2;
            Q2=makeQuery(id+"F10.opPattern","COPY",BODY,{"derivedFrom":makeQuery(id+"F8.opPattern","COPY",BODY,{"derivedFrom":makeQuery(id+"F2.opExtrude","SWEPT_BODY",BODY,{"disambiguationData":[OSD([sQuery(id+"F0.wireOp",EDGE,"E7.right"),sQuery(id+"F0.wireOp",EDGE,"E8.bottom"),sQuery(id+"F0.wireOp",EDGE,"E8.top"),sQuery(id+"F0.wireOp",EDGE,"E8.right")])]}),"instanceName":"1"}),"instanceName":"1"});
            var Q3;
            Q3=makeQuery(id+"F10.opPattern","COPY",BODY,{"derivedFrom":makeQuery(id+"F8.opPattern","COPY",BODY,{"derivedFrom":makeQuery(id+"F3.opPattern","COPY",BODY,{"derivedFrom":makeQuery(id+"F2.opExtrude","SWEPT_BODY",BODY,{"disambiguationData":[OSD([sQuery(id+"F0.wireOp",EDGE,"E3.right"),sQuery(id+"F0.wireOp",EDGE,"E4.right"),sQuery(id+"F0.wireOp",EDGE,"E8.bottom"),sQuery(id+"F0.wireOp",EDGE,"E8.top")])]}),"instanceName":"1"}),"instanceName":"1"}),"instanceName":"1"});
            var Q4;
            Q4=makeQuery(id+"F10.opPattern","COPY",BODY,{"derivedFrom":makeQuery(id+"F8.opPattern","COPY",BODY,{"derivedFrom":makeQuery(id+"F3.opPattern","COPY",BODY,{"derivedFrom":makeQuery(id+"F2.opExtrude","SWEPT_BODY",BODY,{"disambiguationData":[OSD([sQuery(id+"F0.wireOp",EDGE,"E3.left"),sQuery(id+"F0.wireOp",EDGE,"E4.left"),sQuery(id+"F0.wireOp",EDGE,"E8.bottom"),sQuery(id+"F0.wireOp",EDGE,"E8.top")])]}),"instanceName":"1"}),"instanceName":"1"}),"instanceName":"1"});
            var Q5;
            Q5=makeQuery(id+"F10.opPattern","COPY",BODY,{"derivedFrom":makeQuery(id+"F8.opPattern","COPY",BODY,{"derivedFrom":makeQuery(id+"F3.opPattern","COPY",BODY,{"derivedFrom":makeQuery(id+"F2.opExtrude","SWEPT_BODY",BODY,{"disambiguationData":[OSD([sQuery(id+"F0.wireOp",EDGE,"E1.right"),sQuery(id+"F0.wireOp",EDGE,"E2.right"),sQuery(id+"F0.wireOp",EDGE,"E8.bottom"),sQuery(id+"F0.wireOp",EDGE,"E8.top")])]}),"instanceName":"1"}),"instanceName":"1"}),"instanceName":"1"});
            var Q6;
            Q6=makeQuery(id+"F10.opPattern","COPY",BODY,{"derivedFrom":makeQuery(id+"F8.opPattern","COPY",BODY,{"derivedFrom":makeQuery(id+"F3.opPattern","COPY",BODY,{"derivedFrom":makeQuery(id+"F2.opExtrude","SWEPT_BODY",BODY,{"disambiguationData":[OSD([sQuery(id+"F0.wireOp",EDGE,"E1.left"),sQuery(id+"F0.wireOp",EDGE,"E2.left"),sQuery(id+"F0.wireOp",EDGE,"E8.bottom"),sQuery(id+"F0.wireOp",EDGE,"E8.top")])]}),"instanceName":"1"}),"instanceName":"1"}),"instanceName":"1"});
            var Q7;
            Q7=makeQuery(id+"F10.opPattern","COPY",BODY,{"derivedFrom":makeQuery(id+"F8.opPattern","COPY",BODY,{"derivedFrom":makeQuery(id+"F3.opPattern","COPY",BODY,{"derivedFrom":makeQuery(id+"F1.opExtrude","SWEPT_BODY",BODY,{"disambiguationData":[OSD([sQuery(id+"F0.wireOp",EDGE,"E6.right"),sQuery(id+"F0.wireOp",EDGE,"E7.right"),sQuery(id+"F0.wireOp",EDGE,"E8.bottom"),sQuery(id+"F0.wireOp",EDGE,"E8.top")])]}),"instanceName":"1"}),"instanceName":"1"}),"instanceName":"1"});
            var Q8;
            Q8=makeQuery(id+"F10.opPattern","COPY",BODY,{"derivedFrom":makeQuery(id+"F8.opPattern","COPY",BODY,{"derivedFrom":makeQuery(id+"F3.opPattern","COPY",BODY,{"derivedFrom":makeQuery(id+"F1.opExtrude","SWEPT_BODY",BODY,{"disambiguationData":[OSD([sQuery(id+"F0.wireOp",EDGE,"E6.left"),sQuery(id+"F0.wireOp",EDGE,"E7.left"),sQuery(id+"F0.wireOp",EDGE,"E8.bottom"),sQuery(id+"F0.wireOp",EDGE,"E8.top")])]}),"instanceName":"1"}),"instanceName":"1"}),"instanceName":"1"});
            var Q9;
            Q9=makeQuery(id+"F10.opPattern","COPY",BODY,{"derivedFrom":makeQuery(id+"F8.opPattern","COPY",BODY,{"derivedFrom":makeQuery(id+"F3.opPattern","COPY",BODY,{"derivedFrom":makeQuery(id+"F1.opExtrude","SWEPT_BODY",BODY,{"disambiguationData":[OSD([sQuery(id+"F0.wireOp",EDGE,"E4.right"),sQuery(id+"F0.wireOp",EDGE,"E5.right"),sQuery(id+"F0.wireOp",EDGE,"E8.bottom"),sQuery(id+"F0.wireOp",EDGE,"E8.top")])]}),"instanceName":"1"}),"instanceName":"1"}),"instanceName":"1"});
            var Q10;
            Q10=makeQuery(id+"F10.opPattern","COPY",BODY,{"derivedFrom":makeQuery(id+"F8.opPattern","COPY",BODY,{"derivedFrom":makeQuery(id+"F3.opPattern","COPY",BODY,{"derivedFrom":makeQuery(id+"F1.opExtrude","SWEPT_BODY",BODY,{"disambiguationData":[OSD([sQuery(id+"F0.wireOp",EDGE,"E4.left"),sQuery(id+"F0.wireOp",EDGE,"E5.left"),sQuery(id+"F0.wireOp",EDGE,"E8.bottom"),sQuery(id+"F0.wireOp",EDGE,"E8.top")])]}),"instanceName":"1"}),"instanceName":"1"}),"instanceName":"1"});
            var Q11;
            Q11=makeQuery(id+"F10.opPattern","COPY",BODY,{"derivedFrom":makeQuery(id+"F8.opPattern","COPY",BODY,{"derivedFrom":makeQuery(id+"F3.opPattern","COPY",BODY,{"derivedFrom":makeQuery(id+"F1.opExtrude","SWEPT_BODY",BODY,{"disambiguationData":[OSD([sQuery(id+"F0.wireOp",EDGE,"E2.right"),sQuery(id+"F0.wireOp",EDGE,"E3.right"),sQuery(id+"F0.wireOp",EDGE,"E8.bottom"),sQuery(id+"F0.wireOp",EDGE,"E8.top")])]}),"instanceName":"1"}),"instanceName":"1"}),"instanceName":"1"});
            var Q12;
            Q12=makeQuery(id+"F10.opPattern","COPY",BODY,{"derivedFrom":makeQuery(id+"F8.opPattern","COPY",BODY,{"derivedFrom":makeQuery(id+"F3.opPattern","COPY",BODY,{"derivedFrom":makeQuery(id+"F1.opExtrude","SWEPT_BODY",BODY,{"disambiguationData":[OSD([sQuery(id+"F0.wireOp",EDGE,"E2.left"),sQuery(id+"F0.wireOp",EDGE,"E3.left"),sQuery(id+"F0.wireOp",EDGE,"E8.bottom"),sQuery(id+"F0.wireOp",EDGE,"E8.top")])]}),"instanceName":"1"}),"instanceName":"1"}),"instanceName":"1"});
            var Q13;
            Q13=makeQuery(id+"F10.opPattern","COPY",BODY,{"derivedFrom":makeQuery(id+"F8.opPattern","COPY",BODY,{"derivedFrom":makeQuery(id+"F3.opPattern","COPY",BODY,{"derivedFrom":makeQuery(id+"F1.opExtrude","SWEPT_BODY",BODY,{"disambiguationData":[OSD([sQuery(id+"F0.wireOp",EDGE,"E1.left"),sQuery(id+"F0.wireOp",EDGE,"E1.right"),sQuery(id+"F0.wireOp",EDGE,"E8.bottom"),sQuery(id+"F0.wireOp",EDGE,"E8.top")])]}),"instanceName":"1"}),"instanceName":"1"}),"instanceName":"1"});
            var Q14;
            Q14=makeQuery(id+"F10.opPattern","COPY",BODY,{"derivedFrom":makeQuery(id+"F8.opPattern","COPY",BODY,{"derivedFrom":makeQuery(id+"F3.opPattern","COPY",BODY,{"derivedFrom":makeQuery(id+"F1.opExtrude","SWEPT_BODY",BODY,{"disambiguationData":[OSD([sQuery(id+"F0.wireOp",EDGE,"E0.bottom"),sQuery(id+"F0.wireOp",EDGE,"E0.top"),sQuery(id+"F0.wireOp",EDGE,"E0.right"),sQuery(id+"F0.wireOp",EDGE,"E8.left")])]}),"instanceName":"1"}),"instanceName":"1"}),"instanceName":"1"});
            var Q15;
            Q15=makeQuery(id+"F10.opPattern","COPY",BODY,{"derivedFrom":makeQuery(id+"F8.opPattern","COPY",BODY,{"derivedFrom":makeQuery(id+"F3.opPattern","COPY",BODY,{"derivedFrom":makeQuery(id+"F2.opExtrude","SWEPT_BODY",BODY,{"disambiguationData":[OSD([sQuery(id+"F0.wireOp",EDGE,"E7.right"),sQuery(id+"F0.wireOp",EDGE,"E8.bottom"),sQuery(id+"F0.wireOp",EDGE,"E8.top"),sQuery(id+"F0.wireOp",EDGE,"E8.right")])]}),"instanceName":"1"}),"instanceName":"1"}),"instanceName":"1"});
            var Q16;
            Q16=makeQuery(id+"F10.opPattern","COPY",BODY,{"derivedFrom":makeQuery(id+"F8.opPattern","COPY",BODY,{"derivedFrom":makeQuery(id+"F3.opPattern","COPY",BODY,{"derivedFrom":makeQuery(id+"F2.opExtrude","SWEPT_BODY",BODY,{"disambiguationData":[OSD([sQuery(id+"F0.wireOp",EDGE,"E7.left"),sQuery(id+"F0.wireOp",EDGE,"E8.bottom"),sQuery(id+"F0.wireOp",EDGE,"E8.top"),sQuery(id+"F0.wireOp",EDGE,"E8.left")])]}),"instanceName":"1"}),"instanceName":"1"}),"instanceName":"1"});
            var Q17;
            Q17=makeQuery(id+"F10.opPattern","COPY",BODY,{"derivedFrom":makeQuery(id+"F8.opPattern","COPY",BODY,{"derivedFrom":makeQuery(id+"F2.opExtrude","SWEPT_BODY",BODY,{"disambiguationData":[OSD([sQuery(id+"F0.wireOp",EDGE,"E7.left"),sQuery(id+"F0.wireOp",EDGE,"E8.bottom"),sQuery(id+"F0.wireOp",EDGE,"E8.top"),sQuery(id+"F0.wireOp",EDGE,"E8.left")])]}),"instanceName":"1"}),"instanceName":"1"});
            var Q18;
            Q18=makeQuery(id+"F10.opPattern","COPY",BODY,{"derivedFrom":makeQuery(id+"F8.opPattern","COPY",BODY,{"derivedFrom":makeQuery(id+"F2.opExtrude","SWEPT_BODY",BODY,{"disambiguationData":[OSD([sQuery(id+"F0.wireOp",EDGE,"E5.right"),sQuery(id+"F0.wireOp",EDGE,"E6.right"),sQuery(id+"F0.wireOp",EDGE,"E8.bottom"),sQuery(id+"F0.wireOp",EDGE,"E8.top")])]}),"instanceName":"1"}),"instanceName":"1"});
            var Q19;
            Q19=makeQuery(id+"F10.opPattern","COPY",BODY,{"derivedFrom":makeQuery(id+"F8.opPattern","COPY",BODY,{"derivedFrom":makeQuery(id+"F2.opExtrude","SWEPT_BODY",BODY,{"disambiguationData":[OSD([sQuery(id+"F0.wireOp",EDGE,"E5.left"),sQuery(id+"F0.wireOp",EDGE,"E6.left"),sQuery(id+"F0.wireOp",EDGE,"E8.bottom"),sQuery(id+"F0.wireOp",EDGE,"E8.top")])]}),"instanceName":"1"}),"instanceName":"1"});
            var Q20;
            Q20=makeQuery(id+"F10.opPattern","COPY",BODY,{"derivedFrom":makeQuery(id+"F8.opPattern","COPY",BODY,{"derivedFrom":makeQuery(id+"F2.opExtrude","SWEPT_BODY",BODY,{"disambiguationData":[OSD([sQuery(id+"F0.wireOp",EDGE,"E3.right"),sQuery(id+"F0.wireOp",EDGE,"E4.right"),sQuery(id+"F0.wireOp",EDGE,"E8.bottom"),sQuery(id+"F0.wireOp",EDGE,"E8.top")])]}),"instanceName":"1"}),"instanceName":"1"});
            var Q21;
            Q21=makeQuery(id+"F10.opPattern","COPY",BODY,{"derivedFrom":makeQuery(id+"F8.opPattern","COPY",BODY,{"derivedFrom":makeQuery(id+"F1.opExtrude","SWEPT_BODY",BODY,{"disambiguationData":[OSD([sQuery(id+"F0.wireOp",EDGE,"E0.bottom"),sQuery(id+"F0.wireOp",EDGE,"E0.top"),sQuery(id+"F0.wireOp",EDGE,"E0.left"),sQuery(id+"F0.wireOp",EDGE,"E8.right")])]}),"instanceName":"1"}),"instanceName":"1"});
            var Q22;
            Q22=makeQuery(id+"F10.opPattern","COPY",BODY,{"derivedFrom":makeQuery(id+"F8.opPattern","COPY",BODY,{"derivedFrom":makeQuery(id+"F1.opExtrude","SWEPT_BODY",BODY,{"disambiguationData":[OSD([sQuery(id+"F0.wireOp",EDGE,"E0.bottom"),sQuery(id+"F0.wireOp",EDGE,"E0.top"),sQuery(id+"F0.wireOp",EDGE,"E0.right"),sQuery(id+"F0.wireOp",EDGE,"E8.left")])]}),"instanceName":"1"}),"instanceName":"1"});
            var Q23;
            Q23=makeQuery(id+"F10.opPattern","COPY",BODY,{"derivedFrom":makeQuery(id+"F8.opPattern","COPY",BODY,{"derivedFrom":makeQuery(id+"F1.opExtrude","SWEPT_BODY",BODY,{"disambiguationData":[OSD([sQuery(id+"F0.wireOp",EDGE,"E1.left"),sQuery(id+"F0.wireOp",EDGE,"E1.right"),sQuery(id+"F0.wireOp",EDGE,"E8.bottom"),sQuery(id+"F0.wireOp",EDGE,"E8.top")])]}),"instanceName":"1"}),"instanceName":"1"});
            var Q24;
            Q24=makeQuery(id+"F10.opPattern","COPY",BODY,{"derivedFrom":makeQuery(id+"F8.opPattern","COPY",BODY,{"derivedFrom":makeQuery(id+"F1.opExtrude","SWEPT_BODY",BODY,{"disambiguationData":[OSD([sQuery(id+"F0.wireOp",EDGE,"E2.left"),sQuery(id+"F0.wireOp",EDGE,"E3.left"),sQuery(id+"F0.wireOp",EDGE,"E8.bottom"),sQuery(id+"F0.wireOp",EDGE,"E8.top")])]}),"instanceName":"1"}),"instanceName":"1"});
            var Q25;
            Q25=makeQuery(id+"F10.opPattern","COPY",BODY,{"derivedFrom":makeQuery(id+"F8.opPattern","COPY",BODY,{"derivedFrom":makeQuery(id+"F1.opExtrude","SWEPT_BODY",BODY,{"disambiguationData":[OSD([sQuery(id+"F0.wireOp",EDGE,"E2.right"),sQuery(id+"F0.wireOp",EDGE,"E3.right"),sQuery(id+"F0.wireOp",EDGE,"E8.bottom"),sQuery(id+"F0.wireOp",EDGE,"E8.top")])]}),"instanceName":"1"}),"instanceName":"1"});
            var Q26;
            Q26=makeQuery(id+"F10.opPattern","COPY",BODY,{"derivedFrom":makeQuery(id+"F8.opPattern","COPY",BODY,{"derivedFrom":makeQuery(id+"F1.opExtrude","SWEPT_BODY",BODY,{"disambiguationData":[OSD([sQuery(id+"F0.wireOp",EDGE,"E4.left"),sQuery(id+"F0.wireOp",EDGE,"E5.left"),sQuery(id+"F0.wireOp",EDGE,"E8.bottom"),sQuery(id+"F0.wireOp",EDGE,"E8.top")])]}),"instanceName":"1"}),"instanceName":"1"});
            var Q27;
            Q27=makeQuery(id+"F10.opPattern","COPY",BODY,{"derivedFrom":makeQuery(id+"F8.opPattern","COPY",BODY,{"derivedFrom":makeQuery(id+"F1.opExtrude","SWEPT_BODY",BODY,{"disambiguationData":[OSD([sQuery(id+"F0.wireOp",EDGE,"E4.right"),sQuery(id+"F0.wireOp",EDGE,"E5.right"),sQuery(id+"F0.wireOp",EDGE,"E8.bottom"),sQuery(id+"F0.wireOp",EDGE,"E8.top")])]}),"instanceName":"1"}),"instanceName":"1"});
            var Q28;
            Q28=makeQuery(id+"F10.opPattern","COPY",BODY,{"derivedFrom":makeQuery(id+"F8.opPattern","COPY",BODY,{"derivedFrom":makeQuery(id+"F1.opExtrude","SWEPT_BODY",BODY,{"disambiguationData":[OSD([sQuery(id+"F0.wireOp",EDGE,"E6.left"),sQuery(id+"F0.wireOp",EDGE,"E7.left"),sQuery(id+"F0.wireOp",EDGE,"E8.bottom"),sQuery(id+"F0.wireOp",EDGE,"E8.top")])]}),"instanceName":"1"}),"instanceName":"1"});
            var Q29;
            Q29=makeQuery(id+"F10.opPattern","COPY",BODY,{"derivedFrom":makeQuery(id+"F8.opPattern","COPY",BODY,{"derivedFrom":makeQuery(id+"F1.opExtrude","SWEPT_BODY",BODY,{"disambiguationData":[OSD([sQuery(id+"F0.wireOp",EDGE,"E6.right"),sQuery(id+"F0.wireOp",EDGE,"E7.right"),sQuery(id+"F0.wireOp",EDGE,"E8.bottom"),sQuery(id+"F0.wireOp",EDGE,"E8.top")])]}),"instanceName":"1"}),"instanceName":"1"});
            var Q30;
            Q30=makeQuery(id+"F10.opPattern","COPY",BODY,{"derivedFrom":makeQuery(id+"F8.opPattern","COPY",BODY,{"derivedFrom":makeQuery(id+"F2.opExtrude","SWEPT_BODY",BODY,{"disambiguationData":[OSD([sQuery(id+"F0.wireOp",EDGE,"E1.left"),sQuery(id+"F0.wireOp",EDGE,"E2.left"),sQuery(id+"F0.wireOp",EDGE,"E8.bottom"),sQuery(id+"F0.wireOp",EDGE,"E8.top")])]}),"instanceName":"1"}),"instanceName":"1"});
            var Q31;
            Q31=makeQuery(id+"F10.opPattern","COPY",BODY,{"derivedFrom":makeQuery(id+"F8.opPattern","COPY",BODY,{"derivedFrom":makeQuery(id+"F2.opExtrude","SWEPT_BODY",BODY,{"disambiguationData":[OSD([sQuery(id+"F0.wireOp",EDGE,"E1.right"),sQuery(id+"F0.wireOp",EDGE,"E2.right"),sQuery(id+"F0.wireOp",EDGE,"E8.bottom"),sQuery(id+"F0.wireOp",EDGE,"E8.top")])]}),"instanceName":"1"}),"instanceName":"1"});
            var Q32;
            Q32=makeQuery(id+"F10.opPattern","COPY",BODY,{"derivedFrom":makeQuery(id+"F8.opPattern","COPY",BODY,{"derivedFrom":makeQuery(id+"F2.opExtrude","SWEPT_BODY",BODY,{"disambiguationData":[OSD([sQuery(id+"F0.wireOp",EDGE,"E3.left"),sQuery(id+"F0.wireOp",EDGE,"E4.left"),sQuery(id+"F0.wireOp",EDGE,"E8.bottom"),sQuery(id+"F0.wireOp",EDGE,"E8.top")])]}),"instanceName":"1"}),"instanceName":"1"});
            var Q33;
            Q33=makeQuery(id+"F10.opPattern","COPY",BODY,{"derivedFrom":makeQuery(id+"F8.opPattern","COPY",BODY,{"derivedFrom":makeQuery(id+"F3.opPattern","COPY",BODY,{"derivedFrom":makeQuery(id+"F1.opExtrude","SWEPT_BODY",BODY,{"disambiguationData":[OSD([sQuery(id+"F0.wireOp",EDGE,"E0.bottom"),sQuery(id+"F0.wireOp",EDGE,"E0.top"),sQuery(id+"F0.wireOp",EDGE,"E0.left"),sQuery(id+"F0.wireOp",EDGE,"E8.right")])]}),"instanceName":"1"}),"instanceName":"1"}),"instanceName":"1"});
            var Q34;
            Q34=makeQuery(id+"F10.opPattern","COPY",BODY,{"derivedFrom":makeQuery(id+"F8.opPattern","COPY",BODY,{"derivedFrom":makeQuery(id+"F3.opPattern","COPY",BODY,{"derivedFrom":makeQuery(id+"F2.opExtrude","SWEPT_BODY",BODY,{"disambiguationData":[OSD([sQuery(id+"F0.wireOp",EDGE,"E5.right"),sQuery(id+"F0.wireOp",EDGE,"E6.right"),sQuery(id+"F0.wireOp",EDGE,"E8.bottom"),sQuery(id+"F0.wireOp",EDGE,"E8.top")])]}),"instanceName":"1"}),"instanceName":"1"}),"instanceName":"1"});
            var Q35;
            Q35=makeQuery(id+"F10.opPattern","COPY",BODY,{"derivedFrom":makeQuery(id+"F8.opPattern","COPY",BODY,{"derivedFrom":makeQuery(id+"F6.opPattern","COPY",BODY,{"derivedFrom":makeQuery(id+"F1.opExtrude","SWEPT_BODY",BODY,{"disambiguationData":[OSD([sQuery(id+"F0.wireOp",EDGE,"E1.left"),sQuery(id+"F0.wireOp",EDGE,"E1.right"),sQuery(id+"F0.wireOp",EDGE,"E8.bottom"),sQuery(id+"F0.wireOp",EDGE,"E8.top")])]}),"instanceName":"1"}),"instanceName":"1"}),"instanceName":"1"});
            var Q36;
            Q36=makeQuery(id+"F10.opPattern","COPY",BODY,{"derivedFrom":makeQuery(id+"F8.opPattern","COPY",BODY,{"derivedFrom":makeQuery(id+"F6.opPattern","COPY",BODY,{"derivedFrom":makeQuery(id+"F1.opExtrude","SWEPT_BODY",BODY,{"disambiguationData":[OSD([sQuery(id+"F0.wireOp",EDGE,"E0.bottom"),sQuery(id+"F0.wireOp",EDGE,"E0.top"),sQuery(id+"F0.wireOp",EDGE,"E0.right"),sQuery(id+"F0.wireOp",EDGE,"E8.left")])]}),"instanceName":"1"}),"instanceName":"1"}),"instanceName":"1"});
            var Q37;
            Q37=makeQuery(id+"F10.opPattern","COPY",BODY,{"derivedFrom":makeQuery(id+"F8.opPattern","COPY",BODY,{"derivedFrom":makeQuery(id+"F6.opPattern","COPY",BODY,{"derivedFrom":makeQuery(id+"F1.opExtrude","SWEPT_BODY",BODY,{"disambiguationData":[OSD([sQuery(id+"F0.wireOp",EDGE,"E2.left"),sQuery(id+"F0.wireOp",EDGE,"E3.left"),sQuery(id+"F0.wireOp",EDGE,"E8.bottom"),sQuery(id+"F0.wireOp",EDGE,"E8.top")])]}),"instanceName":"1"}),"instanceName":"1"}),"instanceName":"1"});
            var Q38;
            Q38=makeQuery(id+"F10.opPattern","COPY",BODY,{"derivedFrom":makeQuery(id+"F8.opPattern","COPY",BODY,{"derivedFrom":makeQuery(id+"F6.opPattern","COPY",BODY,{"derivedFrom":makeQuery(id+"F1.opExtrude","SWEPT_BODY",BODY,{"disambiguationData":[OSD([sQuery(id+"F0.wireOp",EDGE,"E2.right"),sQuery(id+"F0.wireOp",EDGE,"E3.right"),sQuery(id+"F0.wireOp",EDGE,"E8.bottom"),sQuery(id+"F0.wireOp",EDGE,"E8.top")])]}),"instanceName":"1"}),"instanceName":"1"}),"instanceName":"1"});
            var Q39;
            Q39=makeQuery(id+"F10.opPattern","COPY",BODY,{"derivedFrom":makeQuery(id+"F8.opPattern","COPY",BODY,{"derivedFrom":makeQuery(id+"F6.opPattern","COPY",BODY,{"derivedFrom":makeQuery(id+"F1.opExtrude","SWEPT_BODY",BODY,{"disambiguationData":[OSD([sQuery(id+"F0.wireOp",EDGE,"E4.left"),sQuery(id+"F0.wireOp",EDGE,"E5.left"),sQuery(id+"F0.wireOp",EDGE,"E8.bottom"),sQuery(id+"F0.wireOp",EDGE,"E8.top")])]}),"instanceName":"1"}),"instanceName":"1"}),"instanceName":"1"});
            var Q40;
            Q40=makeQuery(id+"F10.opPattern","COPY",BODY,{"derivedFrom":makeQuery(id+"F8.opPattern","COPY",BODY,{"derivedFrom":makeQuery(id+"F6.opPattern","COPY",BODY,{"derivedFrom":makeQuery(id+"F1.opExtrude","SWEPT_BODY",BODY,{"disambiguationData":[OSD([sQuery(id+"F0.wireOp",EDGE,"E4.right"),sQuery(id+"F0.wireOp",EDGE,"E5.right"),sQuery(id+"F0.wireOp",EDGE,"E8.bottom"),sQuery(id+"F0.wireOp",EDGE,"E8.top")])]}),"instanceName":"1"}),"instanceName":"1"}),"instanceName":"1"});
            var Q41;
            Q41=makeQuery(id+"F10.opPattern","COPY",BODY,{"derivedFrom":makeQuery(id+"F8.opPattern","COPY",BODY,{"derivedFrom":makeQuery(id+"F6.opPattern","COPY",BODY,{"derivedFrom":makeQuery(id+"F1.opExtrude","SWEPT_BODY",BODY,{"disambiguationData":[OSD([sQuery(id+"F0.wireOp",EDGE,"E6.left"),sQuery(id+"F0.wireOp",EDGE,"E7.left"),sQuery(id+"F0.wireOp",EDGE,"E8.bottom"),sQuery(id+"F0.wireOp",EDGE,"E8.top")])]}),"instanceName":"1"}),"instanceName":"1"}),"instanceName":"1"});
            var Q42;
            Q42=makeQuery(id+"F10.opPattern","COPY",BODY,{"derivedFrom":makeQuery(id+"F8.opPattern","COPY",BODY,{"derivedFrom":makeQuery(id+"F6.opPattern","COPY",BODY,{"derivedFrom":makeQuery(id+"F1.opExtrude","SWEPT_BODY",BODY,{"disambiguationData":[OSD([sQuery(id+"F0.wireOp",EDGE,"E6.right"),sQuery(id+"F0.wireOp",EDGE,"E7.right"),sQuery(id+"F0.wireOp",EDGE,"E8.bottom"),sQuery(id+"F0.wireOp",EDGE,"E8.top")])]}),"instanceName":"1"}),"instanceName":"1"}),"instanceName":"1"});
            var Q43;
            Q43=makeQuery(id+"F10.opPattern","COPY",BODY,{"derivedFrom":makeQuery(id+"F8.opPattern","COPY",BODY,{"derivedFrom":makeQuery(id+"F6.opPattern","COPY",BODY,{"derivedFrom":makeQuery(id+"F2.opExtrude","SWEPT_BODY",BODY,{"disambiguationData":[OSD([sQuery(id+"F0.wireOp",EDGE,"E1.left"),sQuery(id+"F0.wireOp",EDGE,"E2.left"),sQuery(id+"F0.wireOp",EDGE,"E8.bottom"),sQuery(id+"F0.wireOp",EDGE,"E8.top")])]}),"instanceName":"1"}),"instanceName":"1"}),"instanceName":"1"});
            var Q44;
            Q44=makeQuery(id+"F10.opPattern","COPY",BODY,{"derivedFrom":makeQuery(id+"F8.opPattern","COPY",BODY,{"derivedFrom":makeQuery(id+"F6.opPattern","COPY",BODY,{"derivedFrom":makeQuery(id+"F2.opExtrude","SWEPT_BODY",BODY,{"disambiguationData":[OSD([sQuery(id+"F0.wireOp",EDGE,"E1.right"),sQuery(id+"F0.wireOp",EDGE,"E2.right"),sQuery(id+"F0.wireOp",EDGE,"E8.bottom"),sQuery(id+"F0.wireOp",EDGE,"E8.top")])]}),"instanceName":"1"}),"instanceName":"1"}),"instanceName":"1"});
            var Q45;
            Q45=makeQuery(id+"F10.opPattern","COPY",BODY,{"derivedFrom":makeQuery(id+"F8.opPattern","COPY",BODY,{"derivedFrom":makeQuery(id+"F6.opPattern","COPY",BODY,{"derivedFrom":makeQuery(id+"F2.opExtrude","SWEPT_BODY",BODY,{"disambiguationData":[OSD([sQuery(id+"F0.wireOp",EDGE,"E3.left"),sQuery(id+"F0.wireOp",EDGE,"E4.left"),sQuery(id+"F0.wireOp",EDGE,"E8.bottom"),sQuery(id+"F0.wireOp",EDGE,"E8.top")])]}),"instanceName":"1"}),"instanceName":"1"}),"instanceName":"1"});
            var Q46;
            Q46=makeQuery(id+"F10.opPattern","COPY",BODY,{"derivedFrom":makeQuery(id+"F8.opPattern","COPY",BODY,{"derivedFrom":makeQuery(id+"F6.opPattern","COPY",BODY,{"derivedFrom":makeQuery(id+"F2.opExtrude","SWEPT_BODY",BODY,{"disambiguationData":[OSD([sQuery(id+"F0.wireOp",EDGE,"E3.right"),sQuery(id+"F0.wireOp",EDGE,"E4.right"),sQuery(id+"F0.wireOp",EDGE,"E8.bottom"),sQuery(id+"F0.wireOp",EDGE,"E8.top")])]}),"instanceName":"1"}),"instanceName":"1"}),"instanceName":"1"});
            var Q47;
            Q47=makeQuery(id+"F10.opPattern","COPY",BODY,{"derivedFrom":makeQuery(id+"F8.opPattern","COPY",BODY,{"derivedFrom":makeQuery(id+"F6.opPattern","COPY",BODY,{"derivedFrom":makeQuery(id+"F2.opExtrude","SWEPT_BODY",BODY,{"disambiguationData":[OSD([sQuery(id+"F0.wireOp",EDGE,"E5.left"),sQuery(id+"F0.wireOp",EDGE,"E6.left"),sQuery(id+"F0.wireOp",EDGE,"E8.bottom"),sQuery(id+"F0.wireOp",EDGE,"E8.top")])]}),"instanceName":"1"}),"instanceName":"1"}),"instanceName":"1"});
            var Q48;
            Q48=makeQuery(id+"F10.opPattern","COPY",BODY,{"derivedFrom":makeQuery(id+"F8.opPattern","COPY",BODY,{"derivedFrom":makeQuery(id+"F6.opPattern","COPY",BODY,{"derivedFrom":makeQuery(id+"F2.opExtrude","SWEPT_BODY",BODY,{"disambiguationData":[OSD([sQuery(id+"F0.wireOp",EDGE,"E5.right"),sQuery(id+"F0.wireOp",EDGE,"E6.right"),sQuery(id+"F0.wireOp",EDGE,"E8.bottom"),sQuery(id+"F0.wireOp",EDGE,"E8.top")])]}),"instanceName":"1"}),"instanceName":"1"}),"instanceName":"1"});
            var Q49;
            Q49=makeQuery(id+"F10.opPattern","COPY",BODY,{"derivedFrom":makeQuery(id+"F8.opPattern","COPY",BODY,{"derivedFrom":makeQuery(id+"F6.opPattern","COPY",BODY,{"derivedFrom":makeQuery(id+"F2.opExtrude","SWEPT_BODY",BODY,{"disambiguationData":[OSD([sQuery(id+"F0.wireOp",EDGE,"E7.left"),sQuery(id+"F0.wireOp",EDGE,"E8.bottom"),sQuery(id+"F0.wireOp",EDGE,"E8.top"),sQuery(id+"F0.wireOp",EDGE,"E8.left")])]}),"instanceName":"1"}),"instanceName":"1"}),"instanceName":"1"});
            var Q50;
            Q50=makeQuery(id+"F10.opPattern","COPY",BODY,{"derivedFrom":makeQuery(id+"F8.opPattern","COPY",BODY,{"derivedFrom":makeQuery(id+"F6.opPattern","COPY",BODY,{"derivedFrom":makeQuery(id+"F2.opExtrude","SWEPT_BODY",BODY,{"disambiguationData":[OSD([sQuery(id+"F0.wireOp",EDGE,"E7.right"),sQuery(id+"F0.wireOp",EDGE,"E8.bottom"),sQuery(id+"F0.wireOp",EDGE,"E8.top"),sQuery(id+"F0.wireOp",EDGE,"E8.right")])]}),"instanceName":"1"}),"instanceName":"1"}),"instanceName":"1"});
            var Q51;
            Q51=makeQuery(id+"F10.opPattern","COPY",BODY,{"derivedFrom":makeQuery(id+"F8.opPattern","COPY",BODY,{"derivedFrom":makeQuery(id+"F6.opPattern","COPY",BODY,{"derivedFrom":makeQuery(id+"F3.opPattern","COPY",BODY,{"derivedFrom":makeQuery(id+"F1.opExtrude","SWEPT_BODY",BODY,{"disambiguationData":[OSD([sQuery(id+"F0.wireOp",EDGE,"E0.bottom"),sQuery(id+"F0.wireOp",EDGE,"E0.top"),sQuery(id+"F0.wireOp",EDGE,"E0.right"),sQuery(id+"F0.wireOp",EDGE,"E8.left")])]}),"instanceName":"1"}),"instanceName":"1"}),"instanceName":"1"}),"instanceName":"1"});
            var Q52;
            Q52=makeQuery(id+"F10.opPattern","COPY",BODY,{"derivedFrom":makeQuery(id+"F8.opPattern","COPY",BODY,{"derivedFrom":makeQuery(id+"F6.opPattern","COPY",BODY,{"derivedFrom":makeQuery(id+"F3.opPattern","COPY",BODY,{"derivedFrom":makeQuery(id+"F1.opExtrude","SWEPT_BODY",BODY,{"disambiguationData":[OSD([sQuery(id+"F0.wireOp",EDGE,"E1.left"),sQuery(id+"F0.wireOp",EDGE,"E1.right"),sQuery(id+"F0.wireOp",EDGE,"E8.bottom"),sQuery(id+"F0.wireOp",EDGE,"E8.top")])]}),"instanceName":"1"}),"instanceName":"1"}),"instanceName":"1"}),"instanceName":"1"});
            var Q53;
            Q53=makeQuery(id+"F10.opPattern","COPY",BODY,{"derivedFrom":makeQuery(id+"F8.opPattern","COPY",BODY,{"derivedFrom":makeQuery(id+"F6.opPattern","COPY",BODY,{"derivedFrom":makeQuery(id+"F3.opPattern","COPY",BODY,{"derivedFrom":makeQuery(id+"F1.opExtrude","SWEPT_BODY",BODY,{"disambiguationData":[OSD([sQuery(id+"F0.wireOp",EDGE,"E2.left"),sQuery(id+"F0.wireOp",EDGE,"E3.left"),sQuery(id+"F0.wireOp",EDGE,"E8.bottom"),sQuery(id+"F0.wireOp",EDGE,"E8.top")])]}),"instanceName":"1"}),"instanceName":"1"}),"instanceName":"1"}),"instanceName":"1"});
            var Q54;
            Q54=makeQuery(id+"F10.opPattern","COPY",BODY,{"derivedFrom":makeQuery(id+"F8.opPattern","COPY",BODY,{"derivedFrom":makeQuery(id+"F6.opPattern","COPY",BODY,{"derivedFrom":makeQuery(id+"F3.opPattern","COPY",BODY,{"derivedFrom":makeQuery(id+"F1.opExtrude","SWEPT_BODY",BODY,{"disambiguationData":[OSD([sQuery(id+"F0.wireOp",EDGE,"E6.left"),sQuery(id+"F0.wireOp",EDGE,"E7.left"),sQuery(id+"F0.wireOp",EDGE,"E8.bottom"),sQuery(id+"F0.wireOp",EDGE,"E8.top")])]}),"instanceName":"1"}),"instanceName":"1"}),"instanceName":"1"}),"instanceName":"1"});
            var Q55;
            Q55=makeQuery(id+"F10.opPattern","COPY",BODY,{"derivedFrom":makeQuery(id+"F8.opPattern","COPY",BODY,{"derivedFrom":makeQuery(id+"F6.opPattern","COPY",BODY,{"derivedFrom":makeQuery(id+"F3.opPattern","COPY",BODY,{"derivedFrom":makeQuery(id+"F1.opExtrude","SWEPT_BODY",BODY,{"disambiguationData":[OSD([sQuery(id+"F0.wireOp",EDGE,"E6.right"),sQuery(id+"F0.wireOp",EDGE,"E7.right"),sQuery(id+"F0.wireOp",EDGE,"E8.bottom"),sQuery(id+"F0.wireOp",EDGE,"E8.top")])]}),"instanceName":"1"}),"instanceName":"1"}),"instanceName":"1"}),"instanceName":"1"});
            var Q56;
            Q56=makeQuery(id+"F10.opPattern","COPY",BODY,{"derivedFrom":makeQuery(id+"F8.opPattern","COPY",BODY,{"derivedFrom":makeQuery(id+"F6.opPattern","COPY",BODY,{"derivedFrom":makeQuery(id+"F3.opPattern","COPY",BODY,{"derivedFrom":makeQuery(id+"F2.opExtrude","SWEPT_BODY",BODY,{"disambiguationData":[OSD([sQuery(id+"F0.wireOp",EDGE,"E3.left"),sQuery(id+"F0.wireOp",EDGE,"E4.left"),sQuery(id+"F0.wireOp",EDGE,"E8.bottom"),sQuery(id+"F0.wireOp",EDGE,"E8.top")])]}),"instanceName":"1"}),"instanceName":"1"}),"instanceName":"1"}),"instanceName":"1"});
            var Q57;
            Q57=makeQuery(id+"F10.opPattern","COPY",BODY,{"derivedFrom":makeQuery(id+"F8.opPattern","COPY",BODY,{"derivedFrom":makeQuery(id+"F6.opPattern","COPY",BODY,{"derivedFrom":makeQuery(id+"F3.opPattern","COPY",BODY,{"derivedFrom":makeQuery(id+"F2.opExtrude","SWEPT_BODY",BODY,{"disambiguationData":[OSD([sQuery(id+"F0.wireOp",EDGE,"E3.right"),sQuery(id+"F0.wireOp",EDGE,"E4.right"),sQuery(id+"F0.wireOp",EDGE,"E8.bottom"),sQuery(id+"F0.wireOp",EDGE,"E8.top")])]}),"instanceName":"1"}),"instanceName":"1"}),"instanceName":"1"}),"instanceName":"1"});
            var Q58;
            Q58=makeQuery(id+"F10.opPattern","COPY",BODY,{"derivedFrom":makeQuery(id+"F8.opPattern","COPY",BODY,{"derivedFrom":makeQuery(id+"F6.opPattern","COPY",BODY,{"derivedFrom":makeQuery(id+"F3.opPattern","COPY",BODY,{"derivedFrom":makeQuery(id+"F2.opExtrude","SWEPT_BODY",BODY,{"disambiguationData":[OSD([sQuery(id+"F0.wireOp",EDGE,"E5.left"),sQuery(id+"F0.wireOp",EDGE,"E6.left"),sQuery(id+"F0.wireOp",EDGE,"E8.bottom"),sQuery(id+"F0.wireOp",EDGE,"E8.top")])]}),"instanceName":"1"}),"instanceName":"1"}),"instanceName":"1"}),"instanceName":"1"});
            var Q59;
            Q59=makeQuery(id+"F10.opPattern","COPY",BODY,{"derivedFrom":makeQuery(id+"F8.opPattern","COPY",BODY,{"derivedFrom":makeQuery(id+"F6.opPattern","COPY",BODY,{"derivedFrom":makeQuery(id+"F3.opPattern","COPY",BODY,{"derivedFrom":makeQuery(id+"F1.opExtrude","SWEPT_BODY",BODY,{"disambiguationData":[OSD([sQuery(id+"F0.wireOp",EDGE,"E0.bottom"),sQuery(id+"F0.wireOp",EDGE,"E0.top"),sQuery(id+"F0.wireOp",EDGE,"E0.left"),sQuery(id+"F0.wireOp",EDGE,"E8.right")])]}),"instanceName":"1"}),"instanceName":"1"}),"instanceName":"1"}),"instanceName":"1"});
            var Q60;
            Q60=makeQuery(id+"F10.opPattern","COPY",BODY,{"derivedFrom":makeQuery(id+"F8.opPattern","COPY",BODY,{"derivedFrom":makeQuery(id+"F6.opPattern","COPY",BODY,{"derivedFrom":makeQuery(id+"F3.opPattern","COPY",BODY,{"derivedFrom":makeQuery(id+"F2.opExtrude","SWEPT_BODY",BODY,{"disambiguationData":[OSD([sQuery(id+"F0.wireOp",EDGE,"E7.left"),sQuery(id+"F0.wireOp",EDGE,"E8.bottom"),sQuery(id+"F0.wireOp",EDGE,"E8.top"),sQuery(id+"F0.wireOp",EDGE,"E8.left")])]}),"instanceName":"1"}),"instanceName":"1"}),"instanceName":"1"}),"instanceName":"1"});
            var Q61;
            Q61=makeQuery(id+"F10.opPattern","COPY",BODY,{"derivedFrom":makeQuery(id+"F8.opPattern","COPY",BODY,{"derivedFrom":makeQuery(id+"F6.opPattern","COPY",BODY,{"derivedFrom":makeQuery(id+"F3.opPattern","COPY",BODY,{"derivedFrom":makeQuery(id+"F1.opExtrude","SWEPT_BODY",BODY,{"disambiguationData":[OSD([sQuery(id+"F0.wireOp",EDGE,"E2.right"),sQuery(id+"F0.wireOp",EDGE,"E3.right"),sQuery(id+"F0.wireOp",EDGE,"E8.bottom"),sQuery(id+"F0.wireOp",EDGE,"E8.top")])]}),"instanceName":"1"}),"instanceName":"1"}),"instanceName":"1"}),"instanceName":"1"});
            var Q62;
            Q62=makeQuery(id+"F10.opPattern","COPY",BODY,{"derivedFrom":makeQuery(id+"F8.opPattern","COPY",BODY,{"derivedFrom":makeQuery(id+"F6.opPattern","COPY",BODY,{"derivedFrom":makeQuery(id+"F3.opPattern","COPY",BODY,{"derivedFrom":makeQuery(id+"F1.opExtrude","SWEPT_BODY",BODY,{"disambiguationData":[OSD([sQuery(id+"F0.wireOp",EDGE,"E4.left"),sQuery(id+"F0.wireOp",EDGE,"E5.left"),sQuery(id+"F0.wireOp",EDGE,"E8.bottom"),sQuery(id+"F0.wireOp",EDGE,"E8.top")])]}),"instanceName":"1"}),"instanceName":"1"}),"instanceName":"1"}),"instanceName":"1"});
            var Q63;
            Q63=makeQuery(id+"F10.opPattern","COPY",BODY,{"derivedFrom":makeQuery(id+"F8.opPattern","COPY",BODY,{"derivedFrom":makeQuery(id+"F6.opPattern","COPY",BODY,{"derivedFrom":makeQuery(id+"F3.opPattern","COPY",BODY,{"derivedFrom":makeQuery(id+"F1.opExtrude","SWEPT_BODY",BODY,{"disambiguationData":[OSD([sQuery(id+"F0.wireOp",EDGE,"E4.right"),sQuery(id+"F0.wireOp",EDGE,"E5.right"),sQuery(id+"F0.wireOp",EDGE,"E8.bottom"),sQuery(id+"F0.wireOp",EDGE,"E8.top")])]}),"instanceName":"1"}),"instanceName":"1"}),"instanceName":"1"}),"instanceName":"1"});
            var Q64;
            Q64=makeQuery(id+"F10.opPattern","COPY",BODY,{"derivedFrom":makeQuery(id+"F8.opPattern","COPY",BODY,{"derivedFrom":makeQuery(id+"F6.opPattern","COPY",BODY,{"derivedFrom":makeQuery(id+"F3.opPattern","COPY",BODY,{"derivedFrom":makeQuery(id+"F2.opExtrude","SWEPT_BODY",BODY,{"disambiguationData":[OSD([sQuery(id+"F0.wireOp",EDGE,"E5.right"),sQuery(id+"F0.wireOp",EDGE,"E6.right"),sQuery(id+"F0.wireOp",EDGE,"E8.bottom"),sQuery(id+"F0.wireOp",EDGE,"E8.top")])]}),"instanceName":"1"}),"instanceName":"1"}),"instanceName":"1"}),"instanceName":"1"});
            var Q65;
            Q65=makeQuery(id+"F10.opPattern","COPY",BODY,{"derivedFrom":makeQuery(id+"F8.opPattern","COPY",BODY,{"derivedFrom":makeQuery(id+"F6.opPattern","COPY",BODY,{"derivedFrom":makeQuery(id+"F3.opPattern","COPY",BODY,{"derivedFrom":makeQuery(id+"F2.opExtrude","SWEPT_BODY",BODY,{"disambiguationData":[OSD([sQuery(id+"F0.wireOp",EDGE,"E7.right"),sQuery(id+"F0.wireOp",EDGE,"E8.bottom"),sQuery(id+"F0.wireOp",EDGE,"E8.top"),sQuery(id+"F0.wireOp",EDGE,"E8.right")])]}),"instanceName":"1"}),"instanceName":"1"}),"instanceName":"1"}),"instanceName":"1"});
            var Q66;
            Q66=makeQuery(id+"F10.opPattern","COPY",BODY,{"derivedFrom":makeQuery(id+"F8.opPattern","COPY",BODY,{"derivedFrom":makeQuery(id+"F6.opPattern","COPY",BODY,{"derivedFrom":makeQuery(id+"F3.opPattern","COPY",BODY,{"derivedFrom":makeQuery(id+"F2.opExtrude","SWEPT_BODY",BODY,{"disambiguationData":[OSD([sQuery(id+"F0.wireOp",EDGE,"E1.left"),sQuery(id+"F0.wireOp",EDGE,"E2.left"),sQuery(id+"F0.wireOp",EDGE,"E8.bottom"),sQuery(id+"F0.wireOp",EDGE,"E8.top")])]}),"instanceName":"1"}),"instanceName":"1"}),"instanceName":"1"}),"instanceName":"1"});
            var Q67;
            Q67=makeQuery(id+"F10.opPattern","COPY",BODY,{"derivedFrom":makeQuery(id+"F8.opPattern","COPY",BODY,{"derivedFrom":makeQuery(id+"F6.opPattern","COPY",BODY,{"derivedFrom":makeQuery(id+"F3.opPattern","COPY",BODY,{"derivedFrom":makeQuery(id+"F2.opExtrude","SWEPT_BODY",BODY,{"disambiguationData":[OSD([sQuery(id+"F0.wireOp",EDGE,"E1.right"),sQuery(id+"F0.wireOp",EDGE,"E2.right"),sQuery(id+"F0.wireOp",EDGE,"E8.bottom"),sQuery(id+"F0.wireOp",EDGE,"E8.top")])]}),"instanceName":"1"}),"instanceName":"1"}),"instanceName":"1"}),"instanceName":"1"});
            var Q68;
            Q68=sQuery(id+"F4.wireOp",EDGE,"E9");
            transform(context, id + "F11", {"entities" : qUnion([Q0, Q1, Q2, Q3, Q4, Q5, Q6, Q7, Q8, Q9, Q10, Q11, Q12, Q13, Q14, Q15, Q16, Q17, Q18, Q19, Q20, Q21, Q22, Q23, Q24, Q25, Q26, Q27, Q28, Q29, Q30, Q31, Q32, Q33, Q34, Q35, Q36, Q37, Q38, Q39, Q40, Q41, Q42, Q43, Q44, Q45, Q46, Q47, Q48, Q49, Q50, Q51, Q52, Q53, Q54, Q55, Q56, Q57, Q58, Q59, Q60, Q61, Q62, Q63, Q64, Q65, Q66, Q67]), "transformType" : TransformType.ROTATION, "transformAxis" : qUnion([Q68]), "angle" : 48 * degree, "makeCopy" : false});
        }
        {
            var Q0;
            Q0=qCreatedBy(makeId("Front.planeOp"),FACE);
            var sketch = newSketch(context, id + "F12", { "sketchPlane" : qUnion([Q0])});
            skLineSegment(sketch, "E10", {"start": v(0, 0) * mm, "end": v(-114.3, 0) * mm, "construction": true});
            skLineSegment(sketch, "E11", {"start": v(-114.3, 0) * mm, "end": v(-114.3, 76.2) * mm, "construction": true});
            skLineSegment(sketch, "E12", {"start": v(-114.3, 76.2) * mm, "end": v(-114.3, 66.04) * mm});
            skLineSegment(sketch, "E13", {"start": v(0, 0) * mm, "end": v(0, 10.16) * mm});
            skLineSegment(sketch, "E14", {"start": v(0, 0) * mm, "end": v(-38.1, 0) * mm});
            skLineSegment(sketch, "E15", {"start": v(-114.3, 76.2) * mm, "end": v(0, 10.16) * mm});
            skLineSegment(sketch, "E16", {"start": v(-114.3, 66.04) * mm, "end": v(-17.58, 10.16) * mm});
            skLineSegment(sketch, "E17", {"start": v(-17.58, 10.16) * mm, "end": v(-38.1, 0) * mm});
            skSolve(sketch);
        }
        {
            var Q0;
            Q0 = qSketchRegion(id + "F12", true);
            var Q1;
            Q1=sQuery(id+"F4.wireOp",EDGE,"E9");
            revolve(context, id + "F13", {"entities" : qUnion([Q0]), "axis" : qUnion([Q1]), "revolveType" : RevolveType.FULL});
        }
        {
            var Q0;
            Q0=qCreatedBy(makeId("Top.planeOp"),FACE);
            var sketch = newSketch(context, id + "F14", { "sketchPlane" : qUnion([Q0])});
            skLineSegment(sketch, "E18.bottom", {"start": v(-190.5, -190.5) * mm, "end": v(190.5, -190.5) * mm});
            skLineSegment(sketch, "E18.top", {"start": v(-190.5, 190.5) * mm, "end": v(190.5, 190.5) * mm});
            skLineSegment(sketch, "E18.left", {"start": v(-190.5, -190.5) * mm, "end": v(-190.5, 190.5) * mm});
            skLineSegment(sketch, "E18.right", {"start": v(190.5, -190.5) * mm, "end": v(190.5, 190.5) * mm});
            skPoint(sketch, "E18.middle", {"position": v(0, 0) * mm});
            skSolve(sketch);
        }
        {
            var Q0;
            Q0=makeQuery(id+"F14.imprint","IMPRINT",FACE,{"disambiguationData":[TD([[makeQuery(id+"F14.imprint","IMPRINT",EDGE,{"derivedFrom":sQuery(id+"F14.wireOp",EDGE,"E18.bottom")}),1.0]])]});
            extrude(context, id + "F15", {"entities" : qUnion([Q0]), "depth" : 76.2 * mm});
        }
        {
            var Q0;
            Q0=makeQuery(id+"F13.opRevolve","SWEPT_BODY",BODY,{"disambiguationData":[OSD([sQuery(id+"F12.wireOp",EDGE,"E12"),sQuery(id+"F12.wireOp",EDGE,"E13"),sQuery(id+"F12.wireOp",EDGE,"c6142da0-9d5d-4dc3-a049-3a31ba379ea4"),sQuery(id+"F12.wireOp",EDGE,"E14"),sQuery(id+"F12.wireOp",EDGE,"e2a201c3-6099-4dac-b623-006856d8e651")])]});
            var Q1;
            Q1=makeQuery(id+"F15.opExtrude","SWEPT_BODY",BODY,{"disambiguationData":[OSD([sQuery(id+"F14.wireOp",EDGE,"E18.bottom"),sQuery(id+"F14.wireOp",EDGE,"E18.top"),sQuery(id+"F14.wireOp",EDGE,"E18.left"),sQuery(id+"F14.wireOp",EDGE,"E18.right")])]});
            booleanBodies(context, id + "F16", {"operationType" : BooleanOperationType.SUBTRACTION, "tools" : qUnion([Q0]), "targets" : qUnion([Q1])});
        }
        {
            var Q0;
            Q0=makeQuery(id+"F16.opBoolean","SPLIT",BODY,{"disambiguationData":[OD(0.0)],"derivedFrom":makeQuery(id+"F15.opExtrude","SWEPT_BODY",BODY,{"disambiguationData":[OSD([sQuery(id+"F14.wireOp",EDGE,"E18.bottom"),sQuery(id+"F14.wireOp",EDGE,"E18.top"),sQuery(id+"F14.wireOp",EDGE,"E18.left"),sQuery(id+"F14.wireOp",EDGE,"E18.right")])]})});
            var Q1;
            Q1=makeQuery(id+"F16.opBoolean","SPLIT",BODY,{"disambiguationData":[OD(1.0)],"derivedFrom":makeQuery(id+"F15.opExtrude","SWEPT_BODY",BODY,{"disambiguationData":[OSD([sQuery(id+"F14.wireOp",EDGE,"E18.bottom"),sQuery(id+"F14.wireOp",EDGE,"E18.top"),sQuery(id+"F14.wireOp",EDGE,"E18.left"),sQuery(id+"F14.wireOp",EDGE,"E18.right")])]})});
            var Q2;
            Q2=makeQuery(id+"F10.opPattern","COPY",BODY,{"derivedFrom":makeQuery(id+"F8.opPattern","COPY",BODY,{"derivedFrom":makeQuery(id+"F6.opPattern","COPY",BODY,{"derivedFrom":makeQuery(id+"F3.opPattern","COPY",BODY,{"derivedFrom":makeQuery(id+"F2.opExtrude","SWEPT_BODY",BODY,{"disambiguationData":[OSD([sQuery(id+"F0.wireOp",EDGE,"E7.right"),sQuery(id+"F0.wireOp",EDGE,"E8.bottom"),sQuery(id+"F0.wireOp",EDGE,"E8.top"),sQuery(id+"F0.wireOp",EDGE,"E8.right")])]}),"instanceName":"1"}),"instanceName":"1"}),"instanceName":"1"}),"instanceName":"1"});
            var Q3;
            Q3=makeQuery(id+"F1.opExtrude","SWEPT_BODY",BODY,{"disambiguationData":[OSD([sQuery(id+"F0.wireOp",EDGE,"E0.bottom"),sQuery(id+"F0.wireOp",EDGE,"E0.top"),sQuery(id+"F0.wireOp",EDGE,"E0.left"),sQuery(id+"F0.wireOp",EDGE,"E8.right")])]});
            var Q4;
            Q4=makeQuery(id+"F1.opExtrude","SWEPT_BODY",BODY,{"disambiguationData":[OSD([sQuery(id+"F0.wireOp",EDGE,"E0.bottom"),sQuery(id+"F0.wireOp",EDGE,"E0.top"),sQuery(id+"F0.wireOp",EDGE,"E0.right"),sQuery(id+"F0.wireOp",EDGE,"E8.left")])]});
            var Q5;
            Q5=makeQuery(id+"F1.opExtrude","SWEPT_BODY",BODY,{"disambiguationData":[OSD([sQuery(id+"F0.wireOp",EDGE,"E1.left"),sQuery(id+"F0.wireOp",EDGE,"E1.right"),sQuery(id+"F0.wireOp",EDGE,"E8.bottom"),sQuery(id+"F0.wireOp",EDGE,"E8.top")])]});
            var Q6;
            Q6=makeQuery(id+"F1.opExtrude","SWEPT_BODY",BODY,{"disambiguationData":[OSD([sQuery(id+"F0.wireOp",EDGE,"E2.left"),sQuery(id+"F0.wireOp",EDGE,"E3.left"),sQuery(id+"F0.wireOp",EDGE,"E8.bottom"),sQuery(id+"F0.wireOp",EDGE,"E8.top")])]});
            var Q7;
            Q7=makeQuery(id+"F1.opExtrude","SWEPT_BODY",BODY,{"disambiguationData":[OSD([sQuery(id+"F0.wireOp",EDGE,"E2.right"),sQuery(id+"F0.wireOp",EDGE,"E3.right"),sQuery(id+"F0.wireOp",EDGE,"E8.bottom"),sQuery(id+"F0.wireOp",EDGE,"E8.top")])]});
            var Q8;
            Q8=makeQuery(id+"F1.opExtrude","SWEPT_BODY",BODY,{"disambiguationData":[OSD([sQuery(id+"F0.wireOp",EDGE,"E4.left"),sQuery(id+"F0.wireOp",EDGE,"E5.left"),sQuery(id+"F0.wireOp",EDGE,"E8.bottom"),sQuery(id+"F0.wireOp",EDGE,"E8.top")])]});
            var Q9;
            Q9=makeQuery(id+"F1.opExtrude","SWEPT_BODY",BODY,{"disambiguationData":[OSD([sQuery(id+"F0.wireOp",EDGE,"E4.right"),sQuery(id+"F0.wireOp",EDGE,"E5.right"),sQuery(id+"F0.wireOp",EDGE,"E8.bottom"),sQuery(id+"F0.wireOp",EDGE,"E8.top")])]});
            var Q10;
            Q10=makeQuery(id+"F1.opExtrude","SWEPT_BODY",BODY,{"disambiguationData":[OSD([sQuery(id+"F0.wireOp",EDGE,"E6.left"),sQuery(id+"F0.wireOp",EDGE,"E7.left"),sQuery(id+"F0.wireOp",EDGE,"E8.bottom"),sQuery(id+"F0.wireOp",EDGE,"E8.top")])]});
            var Q11;
            Q11=makeQuery(id+"F1.opExtrude","SWEPT_BODY",BODY,{"disambiguationData":[OSD([sQuery(id+"F0.wireOp",EDGE,"E6.right"),sQuery(id+"F0.wireOp",EDGE,"E7.right"),sQuery(id+"F0.wireOp",EDGE,"E8.bottom"),sQuery(id+"F0.wireOp",EDGE,"E8.top")])]});
            var Q12;
            Q12=makeQuery(id+"F2.opExtrude","SWEPT_BODY",BODY,{"disambiguationData":[OSD([sQuery(id+"F0.wireOp",EDGE,"E1.left"),sQuery(id+"F0.wireOp",EDGE,"E2.left"),sQuery(id+"F0.wireOp",EDGE,"E8.bottom"),sQuery(id+"F0.wireOp",EDGE,"E8.top")])]});
            var Q13;
            Q13=makeQuery(id+"F2.opExtrude","SWEPT_BODY",BODY,{"disambiguationData":[OSD([sQuery(id+"F0.wireOp",EDGE,"E1.right"),sQuery(id+"F0.wireOp",EDGE,"E2.right"),sQuery(id+"F0.wireOp",EDGE,"E8.bottom"),sQuery(id+"F0.wireOp",EDGE,"E8.top")])]});
            var Q14;
            Q14=makeQuery(id+"F2.opExtrude","SWEPT_BODY",BODY,{"disambiguationData":[OSD([sQuery(id+"F0.wireOp",EDGE,"E3.left"),sQuery(id+"F0.wireOp",EDGE,"E4.left"),sQuery(id+"F0.wireOp",EDGE,"E8.bottom"),sQuery(id+"F0.wireOp",EDGE,"E8.top")])]});
            var Q15;
            Q15=makeQuery(id+"F2.opExtrude","SWEPT_BODY",BODY,{"disambiguationData":[OSD([sQuery(id+"F0.wireOp",EDGE,"E3.right"),sQuery(id+"F0.wireOp",EDGE,"E4.right"),sQuery(id+"F0.wireOp",EDGE,"E8.bottom"),sQuery(id+"F0.wireOp",EDGE,"E8.top")])]});
            var Q16;
            Q16=makeQuery(id+"F2.opExtrude","SWEPT_BODY",BODY,{"disambiguationData":[OSD([sQuery(id+"F0.wireOp",EDGE,"E5.left"),sQuery(id+"F0.wireOp",EDGE,"E6.left"),sQuery(id+"F0.wireOp",EDGE,"E8.bottom"),sQuery(id+"F0.wireOp",EDGE,"E8.top")])]});
            var Q17;
            Q17=makeQuery(id+"F2.opExtrude","SWEPT_BODY",BODY,{"disambiguationData":[OSD([sQuery(id+"F0.wireOp",EDGE,"E5.right"),sQuery(id+"F0.wireOp",EDGE,"E6.right"),sQuery(id+"F0.wireOp",EDGE,"E8.bottom"),sQuery(id+"F0.wireOp",EDGE,"E8.top")])]});
            var Q18;
            Q18=makeQuery(id+"F2.opExtrude","SWEPT_BODY",BODY,{"disambiguationData":[OSD([sQuery(id+"F0.wireOp",EDGE,"E7.left"),sQuery(id+"F0.wireOp",EDGE,"E8.bottom"),sQuery(id+"F0.wireOp",EDGE,"E8.top"),sQuery(id+"F0.wireOp",EDGE,"E8.left")])]});
            var Q19;
            Q19=makeQuery(id+"F2.opExtrude","SWEPT_BODY",BODY,{"disambiguationData":[OSD([sQuery(id+"F0.wireOp",EDGE,"E7.right"),sQuery(id+"F0.wireOp",EDGE,"E8.bottom"),sQuery(id+"F0.wireOp",EDGE,"E8.top"),sQuery(id+"F0.wireOp",EDGE,"E8.right")])]});
            var Q20;
            Q20=makeQuery(id+"F3.opPattern","COPY",BODY,{"derivedFrom":makeQuery(id+"F1.opExtrude","SWEPT_BODY",BODY,{"disambiguationData":[OSD([sQuery(id+"F0.wireOp",EDGE,"E0.bottom"),sQuery(id+"F0.wireOp",EDGE,"E0.top"),sQuery(id+"F0.wireOp",EDGE,"E0.left"),sQuery(id+"F0.wireOp",EDGE,"E8.right")])]}),"instanceName":"1"});
            var Q21;
            Q21=makeQuery(id+"F3.opPattern","COPY",BODY,{"derivedFrom":makeQuery(id+"F1.opExtrude","SWEPT_BODY",BODY,{"disambiguationData":[OSD([sQuery(id+"F0.wireOp",EDGE,"E0.bottom"),sQuery(id+"F0.wireOp",EDGE,"E0.top"),sQuery(id+"F0.wireOp",EDGE,"E0.right"),sQuery(id+"F0.wireOp",EDGE,"E8.left")])]}),"instanceName":"1"});
            var Q22;
            Q22=makeQuery(id+"F3.opPattern","COPY",BODY,{"derivedFrom":makeQuery(id+"F1.opExtrude","SWEPT_BODY",BODY,{"disambiguationData":[OSD([sQuery(id+"F0.wireOp",EDGE,"E1.left"),sQuery(id+"F0.wireOp",EDGE,"E1.right"),sQuery(id+"F0.wireOp",EDGE,"E8.bottom"),sQuery(id+"F0.wireOp",EDGE,"E8.top")])]}),"instanceName":"1"});
            var Q23;
            Q23=makeQuery(id+"F3.opPattern","COPY",BODY,{"derivedFrom":makeQuery(id+"F1.opExtrude","SWEPT_BODY",BODY,{"disambiguationData":[OSD([sQuery(id+"F0.wireOp",EDGE,"E2.left"),sQuery(id+"F0.wireOp",EDGE,"E3.left"),sQuery(id+"F0.wireOp",EDGE,"E8.bottom"),sQuery(id+"F0.wireOp",EDGE,"E8.top")])]}),"instanceName":"1"});
            var Q24;
            Q24=makeQuery(id+"F3.opPattern","COPY",BODY,{"derivedFrom":makeQuery(id+"F1.opExtrude","SWEPT_BODY",BODY,{"disambiguationData":[OSD([sQuery(id+"F0.wireOp",EDGE,"E2.right"),sQuery(id+"F0.wireOp",EDGE,"E3.right"),sQuery(id+"F0.wireOp",EDGE,"E8.bottom"),sQuery(id+"F0.wireOp",EDGE,"E8.top")])]}),"instanceName":"1"});
            var Q25;
            Q25=makeQuery(id+"F3.opPattern","COPY",BODY,{"derivedFrom":makeQuery(id+"F1.opExtrude","SWEPT_BODY",BODY,{"disambiguationData":[OSD([sQuery(id+"F0.wireOp",EDGE,"E4.left"),sQuery(id+"F0.wireOp",EDGE,"E5.left"),sQuery(id+"F0.wireOp",EDGE,"E8.bottom"),sQuery(id+"F0.wireOp",EDGE,"E8.top")])]}),"instanceName":"1"});
            var Q26;
            Q26=makeQuery(id+"F3.opPattern","COPY",BODY,{"derivedFrom":makeQuery(id+"F1.opExtrude","SWEPT_BODY",BODY,{"disambiguationData":[OSD([sQuery(id+"F0.wireOp",EDGE,"E4.right"),sQuery(id+"F0.wireOp",EDGE,"E5.right"),sQuery(id+"F0.wireOp",EDGE,"E8.bottom"),sQuery(id+"F0.wireOp",EDGE,"E8.top")])]}),"instanceName":"1"});
            var Q27;
            Q27=makeQuery(id+"F3.opPattern","COPY",BODY,{"derivedFrom":makeQuery(id+"F1.opExtrude","SWEPT_BODY",BODY,{"disambiguationData":[OSD([sQuery(id+"F0.wireOp",EDGE,"E6.left"),sQuery(id+"F0.wireOp",EDGE,"E7.left"),sQuery(id+"F0.wireOp",EDGE,"E8.bottom"),sQuery(id+"F0.wireOp",EDGE,"E8.top")])]}),"instanceName":"1"});
            var Q28;
            Q28=makeQuery(id+"F3.opPattern","COPY",BODY,{"derivedFrom":makeQuery(id+"F1.opExtrude","SWEPT_BODY",BODY,{"disambiguationData":[OSD([sQuery(id+"F0.wireOp",EDGE,"E6.right"),sQuery(id+"F0.wireOp",EDGE,"E7.right"),sQuery(id+"F0.wireOp",EDGE,"E8.bottom"),sQuery(id+"F0.wireOp",EDGE,"E8.top")])]}),"instanceName":"1"});
            var Q29;
            Q29=makeQuery(id+"F3.opPattern","COPY",BODY,{"derivedFrom":makeQuery(id+"F2.opExtrude","SWEPT_BODY",BODY,{"disambiguationData":[OSD([sQuery(id+"F0.wireOp",EDGE,"E1.left"),sQuery(id+"F0.wireOp",EDGE,"E2.left"),sQuery(id+"F0.wireOp",EDGE,"E8.bottom"),sQuery(id+"F0.wireOp",EDGE,"E8.top")])]}),"instanceName":"1"});
            var Q30;
            Q30=makeQuery(id+"F3.opPattern","COPY",BODY,{"derivedFrom":makeQuery(id+"F2.opExtrude","SWEPT_BODY",BODY,{"disambiguationData":[OSD([sQuery(id+"F0.wireOp",EDGE,"E1.right"),sQuery(id+"F0.wireOp",EDGE,"E2.right"),sQuery(id+"F0.wireOp",EDGE,"E8.bottom"),sQuery(id+"F0.wireOp",EDGE,"E8.top")])]}),"instanceName":"1"});
            var Q31;
            Q31=makeQuery(id+"F3.opPattern","COPY",BODY,{"derivedFrom":makeQuery(id+"F2.opExtrude","SWEPT_BODY",BODY,{"disambiguationData":[OSD([sQuery(id+"F0.wireOp",EDGE,"E3.left"),sQuery(id+"F0.wireOp",EDGE,"E4.left"),sQuery(id+"F0.wireOp",EDGE,"E8.bottom"),sQuery(id+"F0.wireOp",EDGE,"E8.top")])]}),"instanceName":"1"});
            var Q32;
            Q32=makeQuery(id+"F3.opPattern","COPY",BODY,{"derivedFrom":makeQuery(id+"F2.opExtrude","SWEPT_BODY",BODY,{"disambiguationData":[OSD([sQuery(id+"F0.wireOp",EDGE,"E3.right"),sQuery(id+"F0.wireOp",EDGE,"E4.right"),sQuery(id+"F0.wireOp",EDGE,"E8.bottom"),sQuery(id+"F0.wireOp",EDGE,"E8.top")])]}),"instanceName":"1"});
            var Q33;
            Q33=makeQuery(id+"F3.opPattern","COPY",BODY,{"derivedFrom":makeQuery(id+"F2.opExtrude","SWEPT_BODY",BODY,{"disambiguationData":[OSD([sQuery(id+"F0.wireOp",EDGE,"E5.left"),sQuery(id+"F0.wireOp",EDGE,"E6.left"),sQuery(id+"F0.wireOp",EDGE,"E8.bottom"),sQuery(id+"F0.wireOp",EDGE,"E8.top")])]}),"instanceName":"1"});
            var Q34;
            Q34=makeQuery(id+"F3.opPattern","COPY",BODY,{"derivedFrom":makeQuery(id+"F2.opExtrude","SWEPT_BODY",BODY,{"disambiguationData":[OSD([sQuery(id+"F0.wireOp",EDGE,"E5.right"),sQuery(id+"F0.wireOp",EDGE,"E6.right"),sQuery(id+"F0.wireOp",EDGE,"E8.bottom"),sQuery(id+"F0.wireOp",EDGE,"E8.top")])]}),"instanceName":"1"});
            var Q35;
            Q35=makeQuery(id+"F3.opPattern","COPY",BODY,{"derivedFrom":makeQuery(id+"F2.opExtrude","SWEPT_BODY",BODY,{"disambiguationData":[OSD([sQuery(id+"F0.wireOp",EDGE,"E7.left"),sQuery(id+"F0.wireOp",EDGE,"E8.bottom"),sQuery(id+"F0.wireOp",EDGE,"E8.top"),sQuery(id+"F0.wireOp",EDGE,"E8.left")])]}),"instanceName":"1"});
            var Q36;
            Q36=makeQuery(id+"F3.opPattern","COPY",BODY,{"derivedFrom":makeQuery(id+"F2.opExtrude","SWEPT_BODY",BODY,{"disambiguationData":[OSD([sQuery(id+"F0.wireOp",EDGE,"E7.right"),sQuery(id+"F0.wireOp",EDGE,"E8.bottom"),sQuery(id+"F0.wireOp",EDGE,"E8.top"),sQuery(id+"F0.wireOp",EDGE,"E8.right")])]}),"instanceName":"1"});
            var Q37;
            Q37=makeQuery(id+"F6.opPattern","COPY",BODY,{"derivedFrom":makeQuery(id+"F1.opExtrude","SWEPT_BODY",BODY,{"disambiguationData":[OSD([sQuery(id+"F0.wireOp",EDGE,"E0.bottom"),sQuery(id+"F0.wireOp",EDGE,"E0.top"),sQuery(id+"F0.wireOp",EDGE,"E0.left"),sQuery(id+"F0.wireOp",EDGE,"E8.right")])]}),"instanceName":"1"});
            var Q38;
            Q38=makeQuery(id+"F6.opPattern","COPY",BODY,{"derivedFrom":makeQuery(id+"F1.opExtrude","SWEPT_BODY",BODY,{"disambiguationData":[OSD([sQuery(id+"F0.wireOp",EDGE,"E0.bottom"),sQuery(id+"F0.wireOp",EDGE,"E0.top"),sQuery(id+"F0.wireOp",EDGE,"E0.right"),sQuery(id+"F0.wireOp",EDGE,"E8.left")])]}),"instanceName":"1"});
            var Q39;
            Q39=makeQuery(id+"F6.opPattern","COPY",BODY,{"derivedFrom":makeQuery(id+"F1.opExtrude","SWEPT_BODY",BODY,{"disambiguationData":[OSD([sQuery(id+"F0.wireOp",EDGE,"E1.left"),sQuery(id+"F0.wireOp",EDGE,"E1.right"),sQuery(id+"F0.wireOp",EDGE,"E8.bottom"),sQuery(id+"F0.wireOp",EDGE,"E8.top")])]}),"instanceName":"1"});
            var Q40;
            Q40=makeQuery(id+"F6.opPattern","COPY",BODY,{"derivedFrom":makeQuery(id+"F1.opExtrude","SWEPT_BODY",BODY,{"disambiguationData":[OSD([sQuery(id+"F0.wireOp",EDGE,"E2.left"),sQuery(id+"F0.wireOp",EDGE,"E3.left"),sQuery(id+"F0.wireOp",EDGE,"E8.bottom"),sQuery(id+"F0.wireOp",EDGE,"E8.top")])]}),"instanceName":"1"});
            var Q41;
            Q41=makeQuery(id+"F6.opPattern","COPY",BODY,{"derivedFrom":makeQuery(id+"F1.opExtrude","SWEPT_BODY",BODY,{"disambiguationData":[OSD([sQuery(id+"F0.wireOp",EDGE,"E2.right"),sQuery(id+"F0.wireOp",EDGE,"E3.right"),sQuery(id+"F0.wireOp",EDGE,"E8.bottom"),sQuery(id+"F0.wireOp",EDGE,"E8.top")])]}),"instanceName":"1"});
            var Q42;
            Q42=makeQuery(id+"F6.opPattern","COPY",BODY,{"derivedFrom":makeQuery(id+"F1.opExtrude","SWEPT_BODY",BODY,{"disambiguationData":[OSD([sQuery(id+"F0.wireOp",EDGE,"E4.left"),sQuery(id+"F0.wireOp",EDGE,"E5.left"),sQuery(id+"F0.wireOp",EDGE,"E8.bottom"),sQuery(id+"F0.wireOp",EDGE,"E8.top")])]}),"instanceName":"1"});
            var Q43;
            Q43=makeQuery(id+"F6.opPattern","COPY",BODY,{"derivedFrom":makeQuery(id+"F1.opExtrude","SWEPT_BODY",BODY,{"disambiguationData":[OSD([sQuery(id+"F0.wireOp",EDGE,"E4.right"),sQuery(id+"F0.wireOp",EDGE,"E5.right"),sQuery(id+"F0.wireOp",EDGE,"E8.bottom"),sQuery(id+"F0.wireOp",EDGE,"E8.top")])]}),"instanceName":"1"});
            var Q44;
            Q44=makeQuery(id+"F6.opPattern","COPY",BODY,{"derivedFrom":makeQuery(id+"F1.opExtrude","SWEPT_BODY",BODY,{"disambiguationData":[OSD([sQuery(id+"F0.wireOp",EDGE,"E6.left"),sQuery(id+"F0.wireOp",EDGE,"E7.left"),sQuery(id+"F0.wireOp",EDGE,"E8.bottom"),sQuery(id+"F0.wireOp",EDGE,"E8.top")])]}),"instanceName":"1"});
            var Q45;
            Q45=makeQuery(id+"F6.opPattern","COPY",BODY,{"derivedFrom":makeQuery(id+"F1.opExtrude","SWEPT_BODY",BODY,{"disambiguationData":[OSD([sQuery(id+"F0.wireOp",EDGE,"E6.right"),sQuery(id+"F0.wireOp",EDGE,"E7.right"),sQuery(id+"F0.wireOp",EDGE,"E8.bottom"),sQuery(id+"F0.wireOp",EDGE,"E8.top")])]}),"instanceName":"1"});
            var Q46;
            Q46=makeQuery(id+"F6.opPattern","COPY",BODY,{"derivedFrom":makeQuery(id+"F2.opExtrude","SWEPT_BODY",BODY,{"disambiguationData":[OSD([sQuery(id+"F0.wireOp",EDGE,"E1.left"),sQuery(id+"F0.wireOp",EDGE,"E2.left"),sQuery(id+"F0.wireOp",EDGE,"E8.bottom"),sQuery(id+"F0.wireOp",EDGE,"E8.top")])]}),"instanceName":"1"});
            var Q47;
            Q47=makeQuery(id+"F6.opPattern","COPY",BODY,{"derivedFrom":makeQuery(id+"F2.opExtrude","SWEPT_BODY",BODY,{"disambiguationData":[OSD([sQuery(id+"F0.wireOp",EDGE,"E1.right"),sQuery(id+"F0.wireOp",EDGE,"E2.right"),sQuery(id+"F0.wireOp",EDGE,"E8.bottom"),sQuery(id+"F0.wireOp",EDGE,"E8.top")])]}),"instanceName":"1"});
            var Q48;
            Q48=makeQuery(id+"F6.opPattern","COPY",BODY,{"derivedFrom":makeQuery(id+"F2.opExtrude","SWEPT_BODY",BODY,{"disambiguationData":[OSD([sQuery(id+"F0.wireOp",EDGE,"E3.left"),sQuery(id+"F0.wireOp",EDGE,"E4.left"),sQuery(id+"F0.wireOp",EDGE,"E8.bottom"),sQuery(id+"F0.wireOp",EDGE,"E8.top")])]}),"instanceName":"1"});
            var Q49;
            Q49=makeQuery(id+"F6.opPattern","COPY",BODY,{"derivedFrom":makeQuery(id+"F2.opExtrude","SWEPT_BODY",BODY,{"disambiguationData":[OSD([sQuery(id+"F0.wireOp",EDGE,"E3.right"),sQuery(id+"F0.wireOp",EDGE,"E4.right"),sQuery(id+"F0.wireOp",EDGE,"E8.bottom"),sQuery(id+"F0.wireOp",EDGE,"E8.top")])]}),"instanceName":"1"});
            var Q50;
            Q50=makeQuery(id+"F6.opPattern","COPY",BODY,{"derivedFrom":makeQuery(id+"F2.opExtrude","SWEPT_BODY",BODY,{"disambiguationData":[OSD([sQuery(id+"F0.wireOp",EDGE,"E5.left"),sQuery(id+"F0.wireOp",EDGE,"E6.left"),sQuery(id+"F0.wireOp",EDGE,"E8.bottom"),sQuery(id+"F0.wireOp",EDGE,"E8.top")])]}),"instanceName":"1"});
            var Q51;
            Q51=makeQuery(id+"F6.opPattern","COPY",BODY,{"derivedFrom":makeQuery(id+"F2.opExtrude","SWEPT_BODY",BODY,{"disambiguationData":[OSD([sQuery(id+"F0.wireOp",EDGE,"E5.right"),sQuery(id+"F0.wireOp",EDGE,"E6.right"),sQuery(id+"F0.wireOp",EDGE,"E8.bottom"),sQuery(id+"F0.wireOp",EDGE,"E8.top")])]}),"instanceName":"1"});
            var Q52;
            Q52=makeQuery(id+"F6.opPattern","COPY",BODY,{"derivedFrom":makeQuery(id+"F2.opExtrude","SWEPT_BODY",BODY,{"disambiguationData":[OSD([sQuery(id+"F0.wireOp",EDGE,"E7.left"),sQuery(id+"F0.wireOp",EDGE,"E8.bottom"),sQuery(id+"F0.wireOp",EDGE,"E8.top"),sQuery(id+"F0.wireOp",EDGE,"E8.left")])]}),"instanceName":"1"});
            var Q53;
            Q53=makeQuery(id+"F6.opPattern","COPY",BODY,{"derivedFrom":makeQuery(id+"F2.opExtrude","SWEPT_BODY",BODY,{"disambiguationData":[OSD([sQuery(id+"F0.wireOp",EDGE,"E7.right"),sQuery(id+"F0.wireOp",EDGE,"E8.bottom"),sQuery(id+"F0.wireOp",EDGE,"E8.top"),sQuery(id+"F0.wireOp",EDGE,"E8.right")])]}),"instanceName":"1"});
            var Q54;
            Q54=makeQuery(id+"F6.opPattern","COPY",BODY,{"derivedFrom":makeQuery(id+"F3.opPattern","COPY",BODY,{"derivedFrom":makeQuery(id+"F1.opExtrude","SWEPT_BODY",BODY,{"disambiguationData":[OSD([sQuery(id+"F0.wireOp",EDGE,"E0.bottom"),sQuery(id+"F0.wireOp",EDGE,"E0.top"),sQuery(id+"F0.wireOp",EDGE,"E0.left"),sQuery(id+"F0.wireOp",EDGE,"E8.right")])]}),"instanceName":"1"}),"instanceName":"1"});
            var Q55;
            Q55=makeQuery(id+"F6.opPattern","COPY",BODY,{"derivedFrom":makeQuery(id+"F3.opPattern","COPY",BODY,{"derivedFrom":makeQuery(id+"F1.opExtrude","SWEPT_BODY",BODY,{"disambiguationData":[OSD([sQuery(id+"F0.wireOp",EDGE,"E0.bottom"),sQuery(id+"F0.wireOp",EDGE,"E0.top"),sQuery(id+"F0.wireOp",EDGE,"E0.right"),sQuery(id+"F0.wireOp",EDGE,"E8.left")])]}),"instanceName":"1"}),"instanceName":"1"});
            var Q56;
            Q56=makeQuery(id+"F6.opPattern","COPY",BODY,{"derivedFrom":makeQuery(id+"F3.opPattern","COPY",BODY,{"derivedFrom":makeQuery(id+"F1.opExtrude","SWEPT_BODY",BODY,{"disambiguationData":[OSD([sQuery(id+"F0.wireOp",EDGE,"E1.left"),sQuery(id+"F0.wireOp",EDGE,"E1.right"),sQuery(id+"F0.wireOp",EDGE,"E8.bottom"),sQuery(id+"F0.wireOp",EDGE,"E8.top")])]}),"instanceName":"1"}),"instanceName":"1"});
            var Q57;
            Q57=makeQuery(id+"F6.opPattern","COPY",BODY,{"derivedFrom":makeQuery(id+"F3.opPattern","COPY",BODY,{"derivedFrom":makeQuery(id+"F1.opExtrude","SWEPT_BODY",BODY,{"disambiguationData":[OSD([sQuery(id+"F0.wireOp",EDGE,"E2.left"),sQuery(id+"F0.wireOp",EDGE,"E3.left"),sQuery(id+"F0.wireOp",EDGE,"E8.bottom"),sQuery(id+"F0.wireOp",EDGE,"E8.top")])]}),"instanceName":"1"}),"instanceName":"1"});
            var Q58;
            Q58=makeQuery(id+"F6.opPattern","COPY",BODY,{"derivedFrom":makeQuery(id+"F3.opPattern","COPY",BODY,{"derivedFrom":makeQuery(id+"F1.opExtrude","SWEPT_BODY",BODY,{"disambiguationData":[OSD([sQuery(id+"F0.wireOp",EDGE,"E2.right"),sQuery(id+"F0.wireOp",EDGE,"E3.right"),sQuery(id+"F0.wireOp",EDGE,"E8.bottom"),sQuery(id+"F0.wireOp",EDGE,"E8.top")])]}),"instanceName":"1"}),"instanceName":"1"});
            var Q59;
            Q59=makeQuery(id+"F6.opPattern","COPY",BODY,{"derivedFrom":makeQuery(id+"F3.opPattern","COPY",BODY,{"derivedFrom":makeQuery(id+"F1.opExtrude","SWEPT_BODY",BODY,{"disambiguationData":[OSD([sQuery(id+"F0.wireOp",EDGE,"E4.left"),sQuery(id+"F0.wireOp",EDGE,"E5.left"),sQuery(id+"F0.wireOp",EDGE,"E8.bottom"),sQuery(id+"F0.wireOp",EDGE,"E8.top")])]}),"instanceName":"1"}),"instanceName":"1"});
            var Q60;
            Q60=makeQuery(id+"F6.opPattern","COPY",BODY,{"derivedFrom":makeQuery(id+"F3.opPattern","COPY",BODY,{"derivedFrom":makeQuery(id+"F1.opExtrude","SWEPT_BODY",BODY,{"disambiguationData":[OSD([sQuery(id+"F0.wireOp",EDGE,"E4.right"),sQuery(id+"F0.wireOp",EDGE,"E5.right"),sQuery(id+"F0.wireOp",EDGE,"E8.bottom"),sQuery(id+"F0.wireOp",EDGE,"E8.top")])]}),"instanceName":"1"}),"instanceName":"1"});
            var Q61;
            Q61=makeQuery(id+"F6.opPattern","COPY",BODY,{"derivedFrom":makeQuery(id+"F3.opPattern","COPY",BODY,{"derivedFrom":makeQuery(id+"F1.opExtrude","SWEPT_BODY",BODY,{"disambiguationData":[OSD([sQuery(id+"F0.wireOp",EDGE,"E6.left"),sQuery(id+"F0.wireOp",EDGE,"E7.left"),sQuery(id+"F0.wireOp",EDGE,"E8.bottom"),sQuery(id+"F0.wireOp",EDGE,"E8.top")])]}),"instanceName":"1"}),"instanceName":"1"});
            var Q62;
            Q62=makeQuery(id+"F6.opPattern","COPY",BODY,{"derivedFrom":makeQuery(id+"F3.opPattern","COPY",BODY,{"derivedFrom":makeQuery(id+"F1.opExtrude","SWEPT_BODY",BODY,{"disambiguationData":[OSD([sQuery(id+"F0.wireOp",EDGE,"E6.right"),sQuery(id+"F0.wireOp",EDGE,"E7.right"),sQuery(id+"F0.wireOp",EDGE,"E8.bottom"),sQuery(id+"F0.wireOp",EDGE,"E8.top")])]}),"instanceName":"1"}),"instanceName":"1"});
            var Q63;
            Q63=makeQuery(id+"F6.opPattern","COPY",BODY,{"derivedFrom":makeQuery(id+"F3.opPattern","COPY",BODY,{"derivedFrom":makeQuery(id+"F2.opExtrude","SWEPT_BODY",BODY,{"disambiguationData":[OSD([sQuery(id+"F0.wireOp",EDGE,"E1.left"),sQuery(id+"F0.wireOp",EDGE,"E2.left"),sQuery(id+"F0.wireOp",EDGE,"E8.bottom"),sQuery(id+"F0.wireOp",EDGE,"E8.top")])]}),"instanceName":"1"}),"instanceName":"1"});
            var Q64;
            Q64=makeQuery(id+"F6.opPattern","COPY",BODY,{"derivedFrom":makeQuery(id+"F3.opPattern","COPY",BODY,{"derivedFrom":makeQuery(id+"F2.opExtrude","SWEPT_BODY",BODY,{"disambiguationData":[OSD([sQuery(id+"F0.wireOp",EDGE,"E1.right"),sQuery(id+"F0.wireOp",EDGE,"E2.right"),sQuery(id+"F0.wireOp",EDGE,"E8.bottom"),sQuery(id+"F0.wireOp",EDGE,"E8.top")])]}),"instanceName":"1"}),"instanceName":"1"});
            var Q65;
            Q65=makeQuery(id+"F6.opPattern","COPY",BODY,{"derivedFrom":makeQuery(id+"F3.opPattern","COPY",BODY,{"derivedFrom":makeQuery(id+"F2.opExtrude","SWEPT_BODY",BODY,{"disambiguationData":[OSD([sQuery(id+"F0.wireOp",EDGE,"E3.left"),sQuery(id+"F0.wireOp",EDGE,"E4.left"),sQuery(id+"F0.wireOp",EDGE,"E8.bottom"),sQuery(id+"F0.wireOp",EDGE,"E8.top")])]}),"instanceName":"1"}),"instanceName":"1"});
            var Q66;
            Q66=makeQuery(id+"F6.opPattern","COPY",BODY,{"derivedFrom":makeQuery(id+"F3.opPattern","COPY",BODY,{"derivedFrom":makeQuery(id+"F2.opExtrude","SWEPT_BODY",BODY,{"disambiguationData":[OSD([sQuery(id+"F0.wireOp",EDGE,"E3.right"),sQuery(id+"F0.wireOp",EDGE,"E4.right"),sQuery(id+"F0.wireOp",EDGE,"E8.bottom"),sQuery(id+"F0.wireOp",EDGE,"E8.top")])]}),"instanceName":"1"}),"instanceName":"1"});
            var Q67;
            Q67=makeQuery(id+"F6.opPattern","COPY",BODY,{"derivedFrom":makeQuery(id+"F3.opPattern","COPY",BODY,{"derivedFrom":makeQuery(id+"F2.opExtrude","SWEPT_BODY",BODY,{"disambiguationData":[OSD([sQuery(id+"F0.wireOp",EDGE,"E5.left"),sQuery(id+"F0.wireOp",EDGE,"E6.left"),sQuery(id+"F0.wireOp",EDGE,"E8.bottom"),sQuery(id+"F0.wireOp",EDGE,"E8.top")])]}),"instanceName":"1"}),"instanceName":"1"});
            var Q68;
            Q68=makeQuery(id+"F6.opPattern","COPY",BODY,{"derivedFrom":makeQuery(id+"F3.opPattern","COPY",BODY,{"derivedFrom":makeQuery(id+"F2.opExtrude","SWEPT_BODY",BODY,{"disambiguationData":[OSD([sQuery(id+"F0.wireOp",EDGE,"E5.right"),sQuery(id+"F0.wireOp",EDGE,"E6.right"),sQuery(id+"F0.wireOp",EDGE,"E8.bottom"),sQuery(id+"F0.wireOp",EDGE,"E8.top")])]}),"instanceName":"1"}),"instanceName":"1"});
            var Q69;
            Q69=makeQuery(id+"F6.opPattern","COPY",BODY,{"derivedFrom":makeQuery(id+"F3.opPattern","COPY",BODY,{"derivedFrom":makeQuery(id+"F2.opExtrude","SWEPT_BODY",BODY,{"disambiguationData":[OSD([sQuery(id+"F0.wireOp",EDGE,"E7.left"),sQuery(id+"F0.wireOp",EDGE,"E8.bottom"),sQuery(id+"F0.wireOp",EDGE,"E8.top"),sQuery(id+"F0.wireOp",EDGE,"E8.left")])]}),"instanceName":"1"}),"instanceName":"1"});
            var Q70;
            Q70=makeQuery(id+"F6.opPattern","COPY",BODY,{"derivedFrom":makeQuery(id+"F3.opPattern","COPY",BODY,{"derivedFrom":makeQuery(id+"F2.opExtrude","SWEPT_BODY",BODY,{"disambiguationData":[OSD([sQuery(id+"F0.wireOp",EDGE,"E7.right"),sQuery(id+"F0.wireOp",EDGE,"E8.bottom"),sQuery(id+"F0.wireOp",EDGE,"E8.top"),sQuery(id+"F0.wireOp",EDGE,"E8.right")])]}),"instanceName":"1"}),"instanceName":"1"});
            var Q71;
            Q71=makeQuery(id+"F8.opPattern","COPY",BODY,{"derivedFrom":makeQuery(id+"F1.opExtrude","SWEPT_BODY",BODY,{"disambiguationData":[OSD([sQuery(id+"F0.wireOp",EDGE,"E0.bottom"),sQuery(id+"F0.wireOp",EDGE,"E0.top"),sQuery(id+"F0.wireOp",EDGE,"E0.left"),sQuery(id+"F0.wireOp",EDGE,"E8.right")])]}),"instanceName":"1"});
            var Q72;
            Q72=makeQuery(id+"F8.opPattern","COPY",BODY,{"derivedFrom":makeQuery(id+"F1.opExtrude","SWEPT_BODY",BODY,{"disambiguationData":[OSD([sQuery(id+"F0.wireOp",EDGE,"E0.bottom"),sQuery(id+"F0.wireOp",EDGE,"E0.top"),sQuery(id+"F0.wireOp",EDGE,"E0.right"),sQuery(id+"F0.wireOp",EDGE,"E8.left")])]}),"instanceName":"1"});
            var Q73;
            Q73=makeQuery(id+"F8.opPattern","COPY",BODY,{"derivedFrom":makeQuery(id+"F1.opExtrude","SWEPT_BODY",BODY,{"disambiguationData":[OSD([sQuery(id+"F0.wireOp",EDGE,"E1.left"),sQuery(id+"F0.wireOp",EDGE,"E1.right"),sQuery(id+"F0.wireOp",EDGE,"E8.bottom"),sQuery(id+"F0.wireOp",EDGE,"E8.top")])]}),"instanceName":"1"});
            var Q74;
            Q74=makeQuery(id+"F8.opPattern","COPY",BODY,{"derivedFrom":makeQuery(id+"F1.opExtrude","SWEPT_BODY",BODY,{"disambiguationData":[OSD([sQuery(id+"F0.wireOp",EDGE,"E2.left"),sQuery(id+"F0.wireOp",EDGE,"E3.left"),sQuery(id+"F0.wireOp",EDGE,"E8.bottom"),sQuery(id+"F0.wireOp",EDGE,"E8.top")])]}),"instanceName":"1"});
            var Q75;
            Q75=makeQuery(id+"F8.opPattern","COPY",BODY,{"derivedFrom":makeQuery(id+"F1.opExtrude","SWEPT_BODY",BODY,{"disambiguationData":[OSD([sQuery(id+"F0.wireOp",EDGE,"E2.right"),sQuery(id+"F0.wireOp",EDGE,"E3.right"),sQuery(id+"F0.wireOp",EDGE,"E8.bottom"),sQuery(id+"F0.wireOp",EDGE,"E8.top")])]}),"instanceName":"1"});
            var Q76;
            Q76=makeQuery(id+"F8.opPattern","COPY",BODY,{"derivedFrom":makeQuery(id+"F1.opExtrude","SWEPT_BODY",BODY,{"disambiguationData":[OSD([sQuery(id+"F0.wireOp",EDGE,"E4.left"),sQuery(id+"F0.wireOp",EDGE,"E5.left"),sQuery(id+"F0.wireOp",EDGE,"E8.bottom"),sQuery(id+"F0.wireOp",EDGE,"E8.top")])]}),"instanceName":"1"});
            var Q77;
            Q77=makeQuery(id+"F8.opPattern","COPY",BODY,{"derivedFrom":makeQuery(id+"F1.opExtrude","SWEPT_BODY",BODY,{"disambiguationData":[OSD([sQuery(id+"F0.wireOp",EDGE,"E4.right"),sQuery(id+"F0.wireOp",EDGE,"E5.right"),sQuery(id+"F0.wireOp",EDGE,"E8.bottom"),sQuery(id+"F0.wireOp",EDGE,"E8.top")])]}),"instanceName":"1"});
            var Q78;
            Q78=makeQuery(id+"F8.opPattern","COPY",BODY,{"derivedFrom":makeQuery(id+"F1.opExtrude","SWEPT_BODY",BODY,{"disambiguationData":[OSD([sQuery(id+"F0.wireOp",EDGE,"E6.left"),sQuery(id+"F0.wireOp",EDGE,"E7.left"),sQuery(id+"F0.wireOp",EDGE,"E8.bottom"),sQuery(id+"F0.wireOp",EDGE,"E8.top")])]}),"instanceName":"1"});
            var Q79;
            Q79=makeQuery(id+"F8.opPattern","COPY",BODY,{"derivedFrom":makeQuery(id+"F1.opExtrude","SWEPT_BODY",BODY,{"disambiguationData":[OSD([sQuery(id+"F0.wireOp",EDGE,"E6.right"),sQuery(id+"F0.wireOp",EDGE,"E7.right"),sQuery(id+"F0.wireOp",EDGE,"E8.bottom"),sQuery(id+"F0.wireOp",EDGE,"E8.top")])]}),"instanceName":"1"});
            var Q80;
            Q80=makeQuery(id+"F8.opPattern","COPY",BODY,{"derivedFrom":makeQuery(id+"F2.opExtrude","SWEPT_BODY",BODY,{"disambiguationData":[OSD([sQuery(id+"F0.wireOp",EDGE,"E1.left"),sQuery(id+"F0.wireOp",EDGE,"E2.left"),sQuery(id+"F0.wireOp",EDGE,"E8.bottom"),sQuery(id+"F0.wireOp",EDGE,"E8.top")])]}),"instanceName":"1"});
            var Q81;
            Q81=makeQuery(id+"F8.opPattern","COPY",BODY,{"derivedFrom":makeQuery(id+"F2.opExtrude","SWEPT_BODY",BODY,{"disambiguationData":[OSD([sQuery(id+"F0.wireOp",EDGE,"E1.right"),sQuery(id+"F0.wireOp",EDGE,"E2.right"),sQuery(id+"F0.wireOp",EDGE,"E8.bottom"),sQuery(id+"F0.wireOp",EDGE,"E8.top")])]}),"instanceName":"1"});
            var Q82;
            Q82=makeQuery(id+"F8.opPattern","COPY",BODY,{"derivedFrom":makeQuery(id+"F2.opExtrude","SWEPT_BODY",BODY,{"disambiguationData":[OSD([sQuery(id+"F0.wireOp",EDGE,"E3.left"),sQuery(id+"F0.wireOp",EDGE,"E4.left"),sQuery(id+"F0.wireOp",EDGE,"E8.bottom"),sQuery(id+"F0.wireOp",EDGE,"E8.top")])]}),"instanceName":"1"});
            var Q83;
            Q83=makeQuery(id+"F8.opPattern","COPY",BODY,{"derivedFrom":makeQuery(id+"F2.opExtrude","SWEPT_BODY",BODY,{"disambiguationData":[OSD([sQuery(id+"F0.wireOp",EDGE,"E3.right"),sQuery(id+"F0.wireOp",EDGE,"E4.right"),sQuery(id+"F0.wireOp",EDGE,"E8.bottom"),sQuery(id+"F0.wireOp",EDGE,"E8.top")])]}),"instanceName":"1"});
            var Q84;
            Q84=makeQuery(id+"F8.opPattern","COPY",BODY,{"derivedFrom":makeQuery(id+"F2.opExtrude","SWEPT_BODY",BODY,{"disambiguationData":[OSD([sQuery(id+"F0.wireOp",EDGE,"E5.left"),sQuery(id+"F0.wireOp",EDGE,"E6.left"),sQuery(id+"F0.wireOp",EDGE,"E8.bottom"),sQuery(id+"F0.wireOp",EDGE,"E8.top")])]}),"instanceName":"1"});
            var Q85;
            Q85=makeQuery(id+"F8.opPattern","COPY",BODY,{"derivedFrom":makeQuery(id+"F2.opExtrude","SWEPT_BODY",BODY,{"disambiguationData":[OSD([sQuery(id+"F0.wireOp",EDGE,"E5.right"),sQuery(id+"F0.wireOp",EDGE,"E6.right"),sQuery(id+"F0.wireOp",EDGE,"E8.bottom"),sQuery(id+"F0.wireOp",EDGE,"E8.top")])]}),"instanceName":"1"});
            var Q86;
            Q86=makeQuery(id+"F8.opPattern","COPY",BODY,{"derivedFrom":makeQuery(id+"F2.opExtrude","SWEPT_BODY",BODY,{"disambiguationData":[OSD([sQuery(id+"F0.wireOp",EDGE,"E7.left"),sQuery(id+"F0.wireOp",EDGE,"E8.bottom"),sQuery(id+"F0.wireOp",EDGE,"E8.top"),sQuery(id+"F0.wireOp",EDGE,"E8.left")])]}),"instanceName":"1"});
            var Q87;
            Q87=makeQuery(id+"F8.opPattern","COPY",BODY,{"derivedFrom":makeQuery(id+"F2.opExtrude","SWEPT_BODY",BODY,{"disambiguationData":[OSD([sQuery(id+"F0.wireOp",EDGE,"E7.right"),sQuery(id+"F0.wireOp",EDGE,"E8.bottom"),sQuery(id+"F0.wireOp",EDGE,"E8.top"),sQuery(id+"F0.wireOp",EDGE,"E8.right")])]}),"instanceName":"1"});
            var Q88;
            Q88=makeQuery(id+"F8.opPattern","COPY",BODY,{"derivedFrom":makeQuery(id+"F3.opPattern","COPY",BODY,{"derivedFrom":makeQuery(id+"F1.opExtrude","SWEPT_BODY",BODY,{"disambiguationData":[OSD([sQuery(id+"F0.wireOp",EDGE,"E0.bottom"),sQuery(id+"F0.wireOp",EDGE,"E0.top"),sQuery(id+"F0.wireOp",EDGE,"E0.left"),sQuery(id+"F0.wireOp",EDGE,"E8.right")])]}),"instanceName":"1"}),"instanceName":"1"});
            var Q89;
            Q89=makeQuery(id+"F8.opPattern","COPY",BODY,{"derivedFrom":makeQuery(id+"F3.opPattern","COPY",BODY,{"derivedFrom":makeQuery(id+"F1.opExtrude","SWEPT_BODY",BODY,{"disambiguationData":[OSD([sQuery(id+"F0.wireOp",EDGE,"E0.bottom"),sQuery(id+"F0.wireOp",EDGE,"E0.top"),sQuery(id+"F0.wireOp",EDGE,"E0.right"),sQuery(id+"F0.wireOp",EDGE,"E8.left")])]}),"instanceName":"1"}),"instanceName":"1"});
            var Q90;
            Q90=makeQuery(id+"F8.opPattern","COPY",BODY,{"derivedFrom":makeQuery(id+"F3.opPattern","COPY",BODY,{"derivedFrom":makeQuery(id+"F1.opExtrude","SWEPT_BODY",BODY,{"disambiguationData":[OSD([sQuery(id+"F0.wireOp",EDGE,"E1.left"),sQuery(id+"F0.wireOp",EDGE,"E1.right"),sQuery(id+"F0.wireOp",EDGE,"E8.bottom"),sQuery(id+"F0.wireOp",EDGE,"E8.top")])]}),"instanceName":"1"}),"instanceName":"1"});
            var Q91;
            Q91=makeQuery(id+"F8.opPattern","COPY",BODY,{"derivedFrom":makeQuery(id+"F3.opPattern","COPY",BODY,{"derivedFrom":makeQuery(id+"F1.opExtrude","SWEPT_BODY",BODY,{"disambiguationData":[OSD([sQuery(id+"F0.wireOp",EDGE,"E2.left"),sQuery(id+"F0.wireOp",EDGE,"E3.left"),sQuery(id+"F0.wireOp",EDGE,"E8.bottom"),sQuery(id+"F0.wireOp",EDGE,"E8.top")])]}),"instanceName":"1"}),"instanceName":"1"});
            var Q92;
            Q92=makeQuery(id+"F8.opPattern","COPY",BODY,{"derivedFrom":makeQuery(id+"F3.opPattern","COPY",BODY,{"derivedFrom":makeQuery(id+"F1.opExtrude","SWEPT_BODY",BODY,{"disambiguationData":[OSD([sQuery(id+"F0.wireOp",EDGE,"E2.right"),sQuery(id+"F0.wireOp",EDGE,"E3.right"),sQuery(id+"F0.wireOp",EDGE,"E8.bottom"),sQuery(id+"F0.wireOp",EDGE,"E8.top")])]}),"instanceName":"1"}),"instanceName":"1"});
            var Q93;
            Q93=makeQuery(id+"F8.opPattern","COPY",BODY,{"derivedFrom":makeQuery(id+"F3.opPattern","COPY",BODY,{"derivedFrom":makeQuery(id+"F1.opExtrude","SWEPT_BODY",BODY,{"disambiguationData":[OSD([sQuery(id+"F0.wireOp",EDGE,"E4.left"),sQuery(id+"F0.wireOp",EDGE,"E5.left"),sQuery(id+"F0.wireOp",EDGE,"E8.bottom"),sQuery(id+"F0.wireOp",EDGE,"E8.top")])]}),"instanceName":"1"}),"instanceName":"1"});
            var Q94;
            Q94=makeQuery(id+"F8.opPattern","COPY",BODY,{"derivedFrom":makeQuery(id+"F3.opPattern","COPY",BODY,{"derivedFrom":makeQuery(id+"F1.opExtrude","SWEPT_BODY",BODY,{"disambiguationData":[OSD([sQuery(id+"F0.wireOp",EDGE,"E4.right"),sQuery(id+"F0.wireOp",EDGE,"E5.right"),sQuery(id+"F0.wireOp",EDGE,"E8.bottom"),sQuery(id+"F0.wireOp",EDGE,"E8.top")])]}),"instanceName":"1"}),"instanceName":"1"});
            var Q95;
            Q95=makeQuery(id+"F8.opPattern","COPY",BODY,{"derivedFrom":makeQuery(id+"F3.opPattern","COPY",BODY,{"derivedFrom":makeQuery(id+"F1.opExtrude","SWEPT_BODY",BODY,{"disambiguationData":[OSD([sQuery(id+"F0.wireOp",EDGE,"E6.left"),sQuery(id+"F0.wireOp",EDGE,"E7.left"),sQuery(id+"F0.wireOp",EDGE,"E8.bottom"),sQuery(id+"F0.wireOp",EDGE,"E8.top")])]}),"instanceName":"1"}),"instanceName":"1"});
            var Q96;
            Q96=makeQuery(id+"F8.opPattern","COPY",BODY,{"derivedFrom":makeQuery(id+"F3.opPattern","COPY",BODY,{"derivedFrom":makeQuery(id+"F1.opExtrude","SWEPT_BODY",BODY,{"disambiguationData":[OSD([sQuery(id+"F0.wireOp",EDGE,"E6.right"),sQuery(id+"F0.wireOp",EDGE,"E7.right"),sQuery(id+"F0.wireOp",EDGE,"E8.bottom"),sQuery(id+"F0.wireOp",EDGE,"E8.top")])]}),"instanceName":"1"}),"instanceName":"1"});
            var Q97;
            Q97=makeQuery(id+"F8.opPattern","COPY",BODY,{"derivedFrom":makeQuery(id+"F3.opPattern","COPY",BODY,{"derivedFrom":makeQuery(id+"F2.opExtrude","SWEPT_BODY",BODY,{"disambiguationData":[OSD([sQuery(id+"F0.wireOp",EDGE,"E1.left"),sQuery(id+"F0.wireOp",EDGE,"E2.left"),sQuery(id+"F0.wireOp",EDGE,"E8.bottom"),sQuery(id+"F0.wireOp",EDGE,"E8.top")])]}),"instanceName":"1"}),"instanceName":"1"});
            var Q98;
            Q98=makeQuery(id+"F8.opPattern","COPY",BODY,{"derivedFrom":makeQuery(id+"F3.opPattern","COPY",BODY,{"derivedFrom":makeQuery(id+"F2.opExtrude","SWEPT_BODY",BODY,{"disambiguationData":[OSD([sQuery(id+"F0.wireOp",EDGE,"E1.right"),sQuery(id+"F0.wireOp",EDGE,"E2.right"),sQuery(id+"F0.wireOp",EDGE,"E8.bottom"),sQuery(id+"F0.wireOp",EDGE,"E8.top")])]}),"instanceName":"1"}),"instanceName":"1"});
            var Q99;
            Q99=makeQuery(id+"F8.opPattern","COPY",BODY,{"derivedFrom":makeQuery(id+"F3.opPattern","COPY",BODY,{"derivedFrom":makeQuery(id+"F2.opExtrude","SWEPT_BODY",BODY,{"disambiguationData":[OSD([sQuery(id+"F0.wireOp",EDGE,"E3.left"),sQuery(id+"F0.wireOp",EDGE,"E4.left"),sQuery(id+"F0.wireOp",EDGE,"E8.bottom"),sQuery(id+"F0.wireOp",EDGE,"E8.top")])]}),"instanceName":"1"}),"instanceName":"1"});
            var Q100;
            Q100=makeQuery(id+"F8.opPattern","COPY",BODY,{"derivedFrom":makeQuery(id+"F3.opPattern","COPY",BODY,{"derivedFrom":makeQuery(id+"F2.opExtrude","SWEPT_BODY",BODY,{"disambiguationData":[OSD([sQuery(id+"F0.wireOp",EDGE,"E3.right"),sQuery(id+"F0.wireOp",EDGE,"E4.right"),sQuery(id+"F0.wireOp",EDGE,"E8.bottom"),sQuery(id+"F0.wireOp",EDGE,"E8.top")])]}),"instanceName":"1"}),"instanceName":"1"});
            var Q101;
            Q101=makeQuery(id+"F8.opPattern","COPY",BODY,{"derivedFrom":makeQuery(id+"F3.opPattern","COPY",BODY,{"derivedFrom":makeQuery(id+"F2.opExtrude","SWEPT_BODY",BODY,{"disambiguationData":[OSD([sQuery(id+"F0.wireOp",EDGE,"E5.left"),sQuery(id+"F0.wireOp",EDGE,"E6.left"),sQuery(id+"F0.wireOp",EDGE,"E8.bottom"),sQuery(id+"F0.wireOp",EDGE,"E8.top")])]}),"instanceName":"1"}),"instanceName":"1"});
            var Q102;
            Q102=makeQuery(id+"F8.opPattern","COPY",BODY,{"derivedFrom":makeQuery(id+"F3.opPattern","COPY",BODY,{"derivedFrom":makeQuery(id+"F2.opExtrude","SWEPT_BODY",BODY,{"disambiguationData":[OSD([sQuery(id+"F0.wireOp",EDGE,"E5.right"),sQuery(id+"F0.wireOp",EDGE,"E6.right"),sQuery(id+"F0.wireOp",EDGE,"E8.bottom"),sQuery(id+"F0.wireOp",EDGE,"E8.top")])]}),"instanceName":"1"}),"instanceName":"1"});
            var Q103;
            Q103=makeQuery(id+"F8.opPattern","COPY",BODY,{"derivedFrom":makeQuery(id+"F3.opPattern","COPY",BODY,{"derivedFrom":makeQuery(id+"F2.opExtrude","SWEPT_BODY",BODY,{"disambiguationData":[OSD([sQuery(id+"F0.wireOp",EDGE,"E7.left"),sQuery(id+"F0.wireOp",EDGE,"E8.bottom"),sQuery(id+"F0.wireOp",EDGE,"E8.top"),sQuery(id+"F0.wireOp",EDGE,"E8.left")])]}),"instanceName":"1"}),"instanceName":"1"});
            var Q104;
            Q104=makeQuery(id+"F8.opPattern","COPY",BODY,{"derivedFrom":makeQuery(id+"F3.opPattern","COPY",BODY,{"derivedFrom":makeQuery(id+"F2.opExtrude","SWEPT_BODY",BODY,{"disambiguationData":[OSD([sQuery(id+"F0.wireOp",EDGE,"E7.right"),sQuery(id+"F0.wireOp",EDGE,"E8.bottom"),sQuery(id+"F0.wireOp",EDGE,"E8.top"),sQuery(id+"F0.wireOp",EDGE,"E8.right")])]}),"instanceName":"1"}),"instanceName":"1"});
            var Q105;
            Q105=makeQuery(id+"F8.opPattern","COPY",BODY,{"derivedFrom":makeQuery(id+"F6.opPattern","COPY",BODY,{"derivedFrom":makeQuery(id+"F1.opExtrude","SWEPT_BODY",BODY,{"disambiguationData":[OSD([sQuery(id+"F0.wireOp",EDGE,"E0.bottom"),sQuery(id+"F0.wireOp",EDGE,"E0.top"),sQuery(id+"F0.wireOp",EDGE,"E0.left"),sQuery(id+"F0.wireOp",EDGE,"E8.right")])]}),"instanceName":"1"}),"instanceName":"1"});
            var Q106;
            Q106=makeQuery(id+"F8.opPattern","COPY",BODY,{"derivedFrom":makeQuery(id+"F6.opPattern","COPY",BODY,{"derivedFrom":makeQuery(id+"F1.opExtrude","SWEPT_BODY",BODY,{"disambiguationData":[OSD([sQuery(id+"F0.wireOp",EDGE,"E0.bottom"),sQuery(id+"F0.wireOp",EDGE,"E0.top"),sQuery(id+"F0.wireOp",EDGE,"E0.right"),sQuery(id+"F0.wireOp",EDGE,"E8.left")])]}),"instanceName":"1"}),"instanceName":"1"});
            var Q107;
            Q107=makeQuery(id+"F8.opPattern","COPY",BODY,{"derivedFrom":makeQuery(id+"F6.opPattern","COPY",BODY,{"derivedFrom":makeQuery(id+"F1.opExtrude","SWEPT_BODY",BODY,{"disambiguationData":[OSD([sQuery(id+"F0.wireOp",EDGE,"E1.left"),sQuery(id+"F0.wireOp",EDGE,"E1.right"),sQuery(id+"F0.wireOp",EDGE,"E8.bottom"),sQuery(id+"F0.wireOp",EDGE,"E8.top")])]}),"instanceName":"1"}),"instanceName":"1"});
            var Q108;
            Q108=makeQuery(id+"F8.opPattern","COPY",BODY,{"derivedFrom":makeQuery(id+"F6.opPattern","COPY",BODY,{"derivedFrom":makeQuery(id+"F1.opExtrude","SWEPT_BODY",BODY,{"disambiguationData":[OSD([sQuery(id+"F0.wireOp",EDGE,"E2.left"),sQuery(id+"F0.wireOp",EDGE,"E3.left"),sQuery(id+"F0.wireOp",EDGE,"E8.bottom"),sQuery(id+"F0.wireOp",EDGE,"E8.top")])]}),"instanceName":"1"}),"instanceName":"1"});
            var Q109;
            Q109=makeQuery(id+"F8.opPattern","COPY",BODY,{"derivedFrom":makeQuery(id+"F6.opPattern","COPY",BODY,{"derivedFrom":makeQuery(id+"F1.opExtrude","SWEPT_BODY",BODY,{"disambiguationData":[OSD([sQuery(id+"F0.wireOp",EDGE,"E2.right"),sQuery(id+"F0.wireOp",EDGE,"E3.right"),sQuery(id+"F0.wireOp",EDGE,"E8.bottom"),sQuery(id+"F0.wireOp",EDGE,"E8.top")])]}),"instanceName":"1"}),"instanceName":"1"});
            var Q110;
            Q110=makeQuery(id+"F8.opPattern","COPY",BODY,{"derivedFrom":makeQuery(id+"F6.opPattern","COPY",BODY,{"derivedFrom":makeQuery(id+"F1.opExtrude","SWEPT_BODY",BODY,{"disambiguationData":[OSD([sQuery(id+"F0.wireOp",EDGE,"E4.left"),sQuery(id+"F0.wireOp",EDGE,"E5.left"),sQuery(id+"F0.wireOp",EDGE,"E8.bottom"),sQuery(id+"F0.wireOp",EDGE,"E8.top")])]}),"instanceName":"1"}),"instanceName":"1"});
            var Q111;
            Q111=makeQuery(id+"F8.opPattern","COPY",BODY,{"derivedFrom":makeQuery(id+"F6.opPattern","COPY",BODY,{"derivedFrom":makeQuery(id+"F1.opExtrude","SWEPT_BODY",BODY,{"disambiguationData":[OSD([sQuery(id+"F0.wireOp",EDGE,"E4.right"),sQuery(id+"F0.wireOp",EDGE,"E5.right"),sQuery(id+"F0.wireOp",EDGE,"E8.bottom"),sQuery(id+"F0.wireOp",EDGE,"E8.top")])]}),"instanceName":"1"}),"instanceName":"1"});
            var Q112;
            Q112=makeQuery(id+"F8.opPattern","COPY",BODY,{"derivedFrom":makeQuery(id+"F6.opPattern","COPY",BODY,{"derivedFrom":makeQuery(id+"F1.opExtrude","SWEPT_BODY",BODY,{"disambiguationData":[OSD([sQuery(id+"F0.wireOp",EDGE,"E6.left"),sQuery(id+"F0.wireOp",EDGE,"E7.left"),sQuery(id+"F0.wireOp",EDGE,"E8.bottom"),sQuery(id+"F0.wireOp",EDGE,"E8.top")])]}),"instanceName":"1"}),"instanceName":"1"});
            var Q113;
            Q113=makeQuery(id+"F8.opPattern","COPY",BODY,{"derivedFrom":makeQuery(id+"F6.opPattern","COPY",BODY,{"derivedFrom":makeQuery(id+"F1.opExtrude","SWEPT_BODY",BODY,{"disambiguationData":[OSD([sQuery(id+"F0.wireOp",EDGE,"E6.right"),sQuery(id+"F0.wireOp",EDGE,"E7.right"),sQuery(id+"F0.wireOp",EDGE,"E8.bottom"),sQuery(id+"F0.wireOp",EDGE,"E8.top")])]}),"instanceName":"1"}),"instanceName":"1"});
            var Q114;
            Q114=makeQuery(id+"F8.opPattern","COPY",BODY,{"derivedFrom":makeQuery(id+"F6.opPattern","COPY",BODY,{"derivedFrom":makeQuery(id+"F2.opExtrude","SWEPT_BODY",BODY,{"disambiguationData":[OSD([sQuery(id+"F0.wireOp",EDGE,"E1.left"),sQuery(id+"F0.wireOp",EDGE,"E2.left"),sQuery(id+"F0.wireOp",EDGE,"E8.bottom"),sQuery(id+"F0.wireOp",EDGE,"E8.top")])]}),"instanceName":"1"}),"instanceName":"1"});
            var Q115;
            Q115=makeQuery(id+"F8.opPattern","COPY",BODY,{"derivedFrom":makeQuery(id+"F6.opPattern","COPY",BODY,{"derivedFrom":makeQuery(id+"F2.opExtrude","SWEPT_BODY",BODY,{"disambiguationData":[OSD([sQuery(id+"F0.wireOp",EDGE,"E1.right"),sQuery(id+"F0.wireOp",EDGE,"E2.right"),sQuery(id+"F0.wireOp",EDGE,"E8.bottom"),sQuery(id+"F0.wireOp",EDGE,"E8.top")])]}),"instanceName":"1"}),"instanceName":"1"});
            var Q116;
            Q116=makeQuery(id+"F8.opPattern","COPY",BODY,{"derivedFrom":makeQuery(id+"F6.opPattern","COPY",BODY,{"derivedFrom":makeQuery(id+"F2.opExtrude","SWEPT_BODY",BODY,{"disambiguationData":[OSD([sQuery(id+"F0.wireOp",EDGE,"E3.left"),sQuery(id+"F0.wireOp",EDGE,"E4.left"),sQuery(id+"F0.wireOp",EDGE,"E8.bottom"),sQuery(id+"F0.wireOp",EDGE,"E8.top")])]}),"instanceName":"1"}),"instanceName":"1"});
            var Q117;
            Q117=makeQuery(id+"F8.opPattern","COPY",BODY,{"derivedFrom":makeQuery(id+"F6.opPattern","COPY",BODY,{"derivedFrom":makeQuery(id+"F2.opExtrude","SWEPT_BODY",BODY,{"disambiguationData":[OSD([sQuery(id+"F0.wireOp",EDGE,"E3.right"),sQuery(id+"F0.wireOp",EDGE,"E4.right"),sQuery(id+"F0.wireOp",EDGE,"E8.bottom"),sQuery(id+"F0.wireOp",EDGE,"E8.top")])]}),"instanceName":"1"}),"instanceName":"1"});
            var Q118;
            Q118=makeQuery(id+"F8.opPattern","COPY",BODY,{"derivedFrom":makeQuery(id+"F6.opPattern","COPY",BODY,{"derivedFrom":makeQuery(id+"F2.opExtrude","SWEPT_BODY",BODY,{"disambiguationData":[OSD([sQuery(id+"F0.wireOp",EDGE,"E5.left"),sQuery(id+"F0.wireOp",EDGE,"E6.left"),sQuery(id+"F0.wireOp",EDGE,"E8.bottom"),sQuery(id+"F0.wireOp",EDGE,"E8.top")])]}),"instanceName":"1"}),"instanceName":"1"});
            var Q119;
            Q119=makeQuery(id+"F8.opPattern","COPY",BODY,{"derivedFrom":makeQuery(id+"F6.opPattern","COPY",BODY,{"derivedFrom":makeQuery(id+"F2.opExtrude","SWEPT_BODY",BODY,{"disambiguationData":[OSD([sQuery(id+"F0.wireOp",EDGE,"E5.right"),sQuery(id+"F0.wireOp",EDGE,"E6.right"),sQuery(id+"F0.wireOp",EDGE,"E8.bottom"),sQuery(id+"F0.wireOp",EDGE,"E8.top")])]}),"instanceName":"1"}),"instanceName":"1"});
            var Q120;
            Q120=makeQuery(id+"F8.opPattern","COPY",BODY,{"derivedFrom":makeQuery(id+"F6.opPattern","COPY",BODY,{"derivedFrom":makeQuery(id+"F2.opExtrude","SWEPT_BODY",BODY,{"disambiguationData":[OSD([sQuery(id+"F0.wireOp",EDGE,"E7.left"),sQuery(id+"F0.wireOp",EDGE,"E8.bottom"),sQuery(id+"F0.wireOp",EDGE,"E8.top"),sQuery(id+"F0.wireOp",EDGE,"E8.left")])]}),"instanceName":"1"}),"instanceName":"1"});
            var Q121;
            Q121=makeQuery(id+"F8.opPattern","COPY",BODY,{"derivedFrom":makeQuery(id+"F6.opPattern","COPY",BODY,{"derivedFrom":makeQuery(id+"F2.opExtrude","SWEPT_BODY",BODY,{"disambiguationData":[OSD([sQuery(id+"F0.wireOp",EDGE,"E7.right"),sQuery(id+"F0.wireOp",EDGE,"E8.bottom"),sQuery(id+"F0.wireOp",EDGE,"E8.top"),sQuery(id+"F0.wireOp",EDGE,"E8.right")])]}),"instanceName":"1"}),"instanceName":"1"});
            var Q122;
            Q122=makeQuery(id+"F8.opPattern","COPY",BODY,{"derivedFrom":makeQuery(id+"F6.opPattern","COPY",BODY,{"derivedFrom":makeQuery(id+"F3.opPattern","COPY",BODY,{"derivedFrom":makeQuery(id+"F1.opExtrude","SWEPT_BODY",BODY,{"disambiguationData":[OSD([sQuery(id+"F0.wireOp",EDGE,"E0.bottom"),sQuery(id+"F0.wireOp",EDGE,"E0.top"),sQuery(id+"F0.wireOp",EDGE,"E0.left"),sQuery(id+"F0.wireOp",EDGE,"E8.right")])]}),"instanceName":"1"}),"instanceName":"1"}),"instanceName":"1"});
            var Q123;
            Q123=makeQuery(id+"F8.opPattern","COPY",BODY,{"derivedFrom":makeQuery(id+"F6.opPattern","COPY",BODY,{"derivedFrom":makeQuery(id+"F3.opPattern","COPY",BODY,{"derivedFrom":makeQuery(id+"F1.opExtrude","SWEPT_BODY",BODY,{"disambiguationData":[OSD([sQuery(id+"F0.wireOp",EDGE,"E0.bottom"),sQuery(id+"F0.wireOp",EDGE,"E0.top"),sQuery(id+"F0.wireOp",EDGE,"E0.right"),sQuery(id+"F0.wireOp",EDGE,"E8.left")])]}),"instanceName":"1"}),"instanceName":"1"}),"instanceName":"1"});
            var Q124;
            Q124=makeQuery(id+"F8.opPattern","COPY",BODY,{"derivedFrom":makeQuery(id+"F6.opPattern","COPY",BODY,{"derivedFrom":makeQuery(id+"F3.opPattern","COPY",BODY,{"derivedFrom":makeQuery(id+"F1.opExtrude","SWEPT_BODY",BODY,{"disambiguationData":[OSD([sQuery(id+"F0.wireOp",EDGE,"E1.left"),sQuery(id+"F0.wireOp",EDGE,"E1.right"),sQuery(id+"F0.wireOp",EDGE,"E8.bottom"),sQuery(id+"F0.wireOp",EDGE,"E8.top")])]}),"instanceName":"1"}),"instanceName":"1"}),"instanceName":"1"});
            var Q125;
            Q125=makeQuery(id+"F8.opPattern","COPY",BODY,{"derivedFrom":makeQuery(id+"F6.opPattern","COPY",BODY,{"derivedFrom":makeQuery(id+"F3.opPattern","COPY",BODY,{"derivedFrom":makeQuery(id+"F1.opExtrude","SWEPT_BODY",BODY,{"disambiguationData":[OSD([sQuery(id+"F0.wireOp",EDGE,"E2.left"),sQuery(id+"F0.wireOp",EDGE,"E3.left"),sQuery(id+"F0.wireOp",EDGE,"E8.bottom"),sQuery(id+"F0.wireOp",EDGE,"E8.top")])]}),"instanceName":"1"}),"instanceName":"1"}),"instanceName":"1"});
            var Q126;
            Q126=makeQuery(id+"F8.opPattern","COPY",BODY,{"derivedFrom":makeQuery(id+"F6.opPattern","COPY",BODY,{"derivedFrom":makeQuery(id+"F3.opPattern","COPY",BODY,{"derivedFrom":makeQuery(id+"F1.opExtrude","SWEPT_BODY",BODY,{"disambiguationData":[OSD([sQuery(id+"F0.wireOp",EDGE,"E2.right"),sQuery(id+"F0.wireOp",EDGE,"E3.right"),sQuery(id+"F0.wireOp",EDGE,"E8.bottom"),sQuery(id+"F0.wireOp",EDGE,"E8.top")])]}),"instanceName":"1"}),"instanceName":"1"}),"instanceName":"1"});
            var Q127;
            Q127=makeQuery(id+"F8.opPattern","COPY",BODY,{"derivedFrom":makeQuery(id+"F6.opPattern","COPY",BODY,{"derivedFrom":makeQuery(id+"F3.opPattern","COPY",BODY,{"derivedFrom":makeQuery(id+"F1.opExtrude","SWEPT_BODY",BODY,{"disambiguationData":[OSD([sQuery(id+"F0.wireOp",EDGE,"E4.left"),sQuery(id+"F0.wireOp",EDGE,"E5.left"),sQuery(id+"F0.wireOp",EDGE,"E8.bottom"),sQuery(id+"F0.wireOp",EDGE,"E8.top")])]}),"instanceName":"1"}),"instanceName":"1"}),"instanceName":"1"});
            var Q128;
            Q128=makeQuery(id+"F8.opPattern","COPY",BODY,{"derivedFrom":makeQuery(id+"F6.opPattern","COPY",BODY,{"derivedFrom":makeQuery(id+"F3.opPattern","COPY",BODY,{"derivedFrom":makeQuery(id+"F1.opExtrude","SWEPT_BODY",BODY,{"disambiguationData":[OSD([sQuery(id+"F0.wireOp",EDGE,"E4.right"),sQuery(id+"F0.wireOp",EDGE,"E5.right"),sQuery(id+"F0.wireOp",EDGE,"E8.bottom"),sQuery(id+"F0.wireOp",EDGE,"E8.top")])]}),"instanceName":"1"}),"instanceName":"1"}),"instanceName":"1"});
            var Q129;
            Q129=makeQuery(id+"F8.opPattern","COPY",BODY,{"derivedFrom":makeQuery(id+"F6.opPattern","COPY",BODY,{"derivedFrom":makeQuery(id+"F3.opPattern","COPY",BODY,{"derivedFrom":makeQuery(id+"F1.opExtrude","SWEPT_BODY",BODY,{"disambiguationData":[OSD([sQuery(id+"F0.wireOp",EDGE,"E6.left"),sQuery(id+"F0.wireOp",EDGE,"E7.left"),sQuery(id+"F0.wireOp",EDGE,"E8.bottom"),sQuery(id+"F0.wireOp",EDGE,"E8.top")])]}),"instanceName":"1"}),"instanceName":"1"}),"instanceName":"1"});
            var Q130;
            Q130=makeQuery(id+"F8.opPattern","COPY",BODY,{"derivedFrom":makeQuery(id+"F6.opPattern","COPY",BODY,{"derivedFrom":makeQuery(id+"F3.opPattern","COPY",BODY,{"derivedFrom":makeQuery(id+"F1.opExtrude","SWEPT_BODY",BODY,{"disambiguationData":[OSD([sQuery(id+"F0.wireOp",EDGE,"E6.right"),sQuery(id+"F0.wireOp",EDGE,"E7.right"),sQuery(id+"F0.wireOp",EDGE,"E8.bottom"),sQuery(id+"F0.wireOp",EDGE,"E8.top")])]}),"instanceName":"1"}),"instanceName":"1"}),"instanceName":"1"});
            var Q131;
            Q131=makeQuery(id+"F8.opPattern","COPY",BODY,{"derivedFrom":makeQuery(id+"F6.opPattern","COPY",BODY,{"derivedFrom":makeQuery(id+"F3.opPattern","COPY",BODY,{"derivedFrom":makeQuery(id+"F2.opExtrude","SWEPT_BODY",BODY,{"disambiguationData":[OSD([sQuery(id+"F0.wireOp",EDGE,"E1.left"),sQuery(id+"F0.wireOp",EDGE,"E2.left"),sQuery(id+"F0.wireOp",EDGE,"E8.bottom"),sQuery(id+"F0.wireOp",EDGE,"E8.top")])]}),"instanceName":"1"}),"instanceName":"1"}),"instanceName":"1"});
            var Q132;
            Q132=makeQuery(id+"F8.opPattern","COPY",BODY,{"derivedFrom":makeQuery(id+"F6.opPattern","COPY",BODY,{"derivedFrom":makeQuery(id+"F3.opPattern","COPY",BODY,{"derivedFrom":makeQuery(id+"F2.opExtrude","SWEPT_BODY",BODY,{"disambiguationData":[OSD([sQuery(id+"F0.wireOp",EDGE,"E1.right"),sQuery(id+"F0.wireOp",EDGE,"E2.right"),sQuery(id+"F0.wireOp",EDGE,"E8.bottom"),sQuery(id+"F0.wireOp",EDGE,"E8.top")])]}),"instanceName":"1"}),"instanceName":"1"}),"instanceName":"1"});
            var Q133;
            Q133=makeQuery(id+"F8.opPattern","COPY",BODY,{"derivedFrom":makeQuery(id+"F6.opPattern","COPY",BODY,{"derivedFrom":makeQuery(id+"F3.opPattern","COPY",BODY,{"derivedFrom":makeQuery(id+"F2.opExtrude","SWEPT_BODY",BODY,{"disambiguationData":[OSD([sQuery(id+"F0.wireOp",EDGE,"E3.left"),sQuery(id+"F0.wireOp",EDGE,"E4.left"),sQuery(id+"F0.wireOp",EDGE,"E8.bottom"),sQuery(id+"F0.wireOp",EDGE,"E8.top")])]}),"instanceName":"1"}),"instanceName":"1"}),"instanceName":"1"});
            var Q134;
            Q134=makeQuery(id+"F8.opPattern","COPY",BODY,{"derivedFrom":makeQuery(id+"F6.opPattern","COPY",BODY,{"derivedFrom":makeQuery(id+"F3.opPattern","COPY",BODY,{"derivedFrom":makeQuery(id+"F2.opExtrude","SWEPT_BODY",BODY,{"disambiguationData":[OSD([sQuery(id+"F0.wireOp",EDGE,"E3.right"),sQuery(id+"F0.wireOp",EDGE,"E4.right"),sQuery(id+"F0.wireOp",EDGE,"E8.bottom"),sQuery(id+"F0.wireOp",EDGE,"E8.top")])]}),"instanceName":"1"}),"instanceName":"1"}),"instanceName":"1"});
            var Q135;
            Q135=makeQuery(id+"F8.opPattern","COPY",BODY,{"derivedFrom":makeQuery(id+"F6.opPattern","COPY",BODY,{"derivedFrom":makeQuery(id+"F3.opPattern","COPY",BODY,{"derivedFrom":makeQuery(id+"F2.opExtrude","SWEPT_BODY",BODY,{"disambiguationData":[OSD([sQuery(id+"F0.wireOp",EDGE,"E5.left"),sQuery(id+"F0.wireOp",EDGE,"E6.left"),sQuery(id+"F0.wireOp",EDGE,"E8.bottom"),sQuery(id+"F0.wireOp",EDGE,"E8.top")])]}),"instanceName":"1"}),"instanceName":"1"}),"instanceName":"1"});
            var Q136;
            Q136=makeQuery(id+"F8.opPattern","COPY",BODY,{"derivedFrom":makeQuery(id+"F6.opPattern","COPY",BODY,{"derivedFrom":makeQuery(id+"F3.opPattern","COPY",BODY,{"derivedFrom":makeQuery(id+"F2.opExtrude","SWEPT_BODY",BODY,{"disambiguationData":[OSD([sQuery(id+"F0.wireOp",EDGE,"E5.right"),sQuery(id+"F0.wireOp",EDGE,"E6.right"),sQuery(id+"F0.wireOp",EDGE,"E8.bottom"),sQuery(id+"F0.wireOp",EDGE,"E8.top")])]}),"instanceName":"1"}),"instanceName":"1"}),"instanceName":"1"});
            var Q137;
            Q137=makeQuery(id+"F8.opPattern","COPY",BODY,{"derivedFrom":makeQuery(id+"F6.opPattern","COPY",BODY,{"derivedFrom":makeQuery(id+"F3.opPattern","COPY",BODY,{"derivedFrom":makeQuery(id+"F2.opExtrude","SWEPT_BODY",BODY,{"disambiguationData":[OSD([sQuery(id+"F0.wireOp",EDGE,"E7.left"),sQuery(id+"F0.wireOp",EDGE,"E8.bottom"),sQuery(id+"F0.wireOp",EDGE,"E8.top"),sQuery(id+"F0.wireOp",EDGE,"E8.left")])]}),"instanceName":"1"}),"instanceName":"1"}),"instanceName":"1"});
            var Q138;
            Q138=makeQuery(id+"F8.opPattern","COPY",BODY,{"derivedFrom":makeQuery(id+"F6.opPattern","COPY",BODY,{"derivedFrom":makeQuery(id+"F3.opPattern","COPY",BODY,{"derivedFrom":makeQuery(id+"F2.opExtrude","SWEPT_BODY",BODY,{"disambiguationData":[OSD([sQuery(id+"F0.wireOp",EDGE,"E7.right"),sQuery(id+"F0.wireOp",EDGE,"E8.bottom"),sQuery(id+"F0.wireOp",EDGE,"E8.top"),sQuery(id+"F0.wireOp",EDGE,"E8.right")])]}),"instanceName":"1"}),"instanceName":"1"}),"instanceName":"1"});
            var Q139;
            Q139=makeQuery(id+"F10.opPattern","COPY",BODY,{"derivedFrom":makeQuery(id+"F8.opPattern","COPY",BODY,{"derivedFrom":makeQuery(id+"F1.opExtrude","SWEPT_BODY",BODY,{"disambiguationData":[OSD([sQuery(id+"F0.wireOp",EDGE,"E0.bottom"),sQuery(id+"F0.wireOp",EDGE,"E0.top"),sQuery(id+"F0.wireOp",EDGE,"E0.left"),sQuery(id+"F0.wireOp",EDGE,"E8.right")])]}),"instanceName":"1"}),"instanceName":"1"});
            var Q140;
            Q140=makeQuery(id+"F10.opPattern","COPY",BODY,{"derivedFrom":makeQuery(id+"F8.opPattern","COPY",BODY,{"derivedFrom":makeQuery(id+"F1.opExtrude","SWEPT_BODY",BODY,{"disambiguationData":[OSD([sQuery(id+"F0.wireOp",EDGE,"E0.bottom"),sQuery(id+"F0.wireOp",EDGE,"E0.top"),sQuery(id+"F0.wireOp",EDGE,"E0.right"),sQuery(id+"F0.wireOp",EDGE,"E8.left")])]}),"instanceName":"1"}),"instanceName":"1"});
            var Q141;
            Q141=makeQuery(id+"F10.opPattern","COPY",BODY,{"derivedFrom":makeQuery(id+"F8.opPattern","COPY",BODY,{"derivedFrom":makeQuery(id+"F1.opExtrude","SWEPT_BODY",BODY,{"disambiguationData":[OSD([sQuery(id+"F0.wireOp",EDGE,"E1.left"),sQuery(id+"F0.wireOp",EDGE,"E1.right"),sQuery(id+"F0.wireOp",EDGE,"E8.bottom"),sQuery(id+"F0.wireOp",EDGE,"E8.top")])]}),"instanceName":"1"}),"instanceName":"1"});
            var Q142;
            Q142=makeQuery(id+"F10.opPattern","COPY",BODY,{"derivedFrom":makeQuery(id+"F8.opPattern","COPY",BODY,{"derivedFrom":makeQuery(id+"F1.opExtrude","SWEPT_BODY",BODY,{"disambiguationData":[OSD([sQuery(id+"F0.wireOp",EDGE,"E2.left"),sQuery(id+"F0.wireOp",EDGE,"E3.left"),sQuery(id+"F0.wireOp",EDGE,"E8.bottom"),sQuery(id+"F0.wireOp",EDGE,"E8.top")])]}),"instanceName":"1"}),"instanceName":"1"});
            var Q143;
            Q143=makeQuery(id+"F10.opPattern","COPY",BODY,{"derivedFrom":makeQuery(id+"F8.opPattern","COPY",BODY,{"derivedFrom":makeQuery(id+"F1.opExtrude","SWEPT_BODY",BODY,{"disambiguationData":[OSD([sQuery(id+"F0.wireOp",EDGE,"E2.right"),sQuery(id+"F0.wireOp",EDGE,"E3.right"),sQuery(id+"F0.wireOp",EDGE,"E8.bottom"),sQuery(id+"F0.wireOp",EDGE,"E8.top")])]}),"instanceName":"1"}),"instanceName":"1"});
            var Q144;
            Q144=makeQuery(id+"F10.opPattern","COPY",BODY,{"derivedFrom":makeQuery(id+"F8.opPattern","COPY",BODY,{"derivedFrom":makeQuery(id+"F1.opExtrude","SWEPT_BODY",BODY,{"disambiguationData":[OSD([sQuery(id+"F0.wireOp",EDGE,"E4.left"),sQuery(id+"F0.wireOp",EDGE,"E5.left"),sQuery(id+"F0.wireOp",EDGE,"E8.bottom"),sQuery(id+"F0.wireOp",EDGE,"E8.top")])]}),"instanceName":"1"}),"instanceName":"1"});
            var Q145;
            Q145=makeQuery(id+"F10.opPattern","COPY",BODY,{"derivedFrom":makeQuery(id+"F8.opPattern","COPY",BODY,{"derivedFrom":makeQuery(id+"F1.opExtrude","SWEPT_BODY",BODY,{"disambiguationData":[OSD([sQuery(id+"F0.wireOp",EDGE,"E4.right"),sQuery(id+"F0.wireOp",EDGE,"E5.right"),sQuery(id+"F0.wireOp",EDGE,"E8.bottom"),sQuery(id+"F0.wireOp",EDGE,"E8.top")])]}),"instanceName":"1"}),"instanceName":"1"});
            var Q146;
            Q146=makeQuery(id+"F10.opPattern","COPY",BODY,{"derivedFrom":makeQuery(id+"F8.opPattern","COPY",BODY,{"derivedFrom":makeQuery(id+"F1.opExtrude","SWEPT_BODY",BODY,{"disambiguationData":[OSD([sQuery(id+"F0.wireOp",EDGE,"E6.left"),sQuery(id+"F0.wireOp",EDGE,"E7.left"),sQuery(id+"F0.wireOp",EDGE,"E8.bottom"),sQuery(id+"F0.wireOp",EDGE,"E8.top")])]}),"instanceName":"1"}),"instanceName":"1"});
            var Q147;
            Q147=makeQuery(id+"F10.opPattern","COPY",BODY,{"derivedFrom":makeQuery(id+"F8.opPattern","COPY",BODY,{"derivedFrom":makeQuery(id+"F1.opExtrude","SWEPT_BODY",BODY,{"disambiguationData":[OSD([sQuery(id+"F0.wireOp",EDGE,"E6.right"),sQuery(id+"F0.wireOp",EDGE,"E7.right"),sQuery(id+"F0.wireOp",EDGE,"E8.bottom"),sQuery(id+"F0.wireOp",EDGE,"E8.top")])]}),"instanceName":"1"}),"instanceName":"1"});
            var Q148;
            Q148=makeQuery(id+"F10.opPattern","COPY",BODY,{"derivedFrom":makeQuery(id+"F8.opPattern","COPY",BODY,{"derivedFrom":makeQuery(id+"F2.opExtrude","SWEPT_BODY",BODY,{"disambiguationData":[OSD([sQuery(id+"F0.wireOp",EDGE,"E1.left"),sQuery(id+"F0.wireOp",EDGE,"E2.left"),sQuery(id+"F0.wireOp",EDGE,"E8.bottom"),sQuery(id+"F0.wireOp",EDGE,"E8.top")])]}),"instanceName":"1"}),"instanceName":"1"});
            var Q149;
            Q149=makeQuery(id+"F10.opPattern","COPY",BODY,{"derivedFrom":makeQuery(id+"F8.opPattern","COPY",BODY,{"derivedFrom":makeQuery(id+"F2.opExtrude","SWEPT_BODY",BODY,{"disambiguationData":[OSD([sQuery(id+"F0.wireOp",EDGE,"E1.right"),sQuery(id+"F0.wireOp",EDGE,"E2.right"),sQuery(id+"F0.wireOp",EDGE,"E8.bottom"),sQuery(id+"F0.wireOp",EDGE,"E8.top")])]}),"instanceName":"1"}),"instanceName":"1"});
            var Q150;
            Q150=makeQuery(id+"F10.opPattern","COPY",BODY,{"derivedFrom":makeQuery(id+"F8.opPattern","COPY",BODY,{"derivedFrom":makeQuery(id+"F2.opExtrude","SWEPT_BODY",BODY,{"disambiguationData":[OSD([sQuery(id+"F0.wireOp",EDGE,"E3.left"),sQuery(id+"F0.wireOp",EDGE,"E4.left"),sQuery(id+"F0.wireOp",EDGE,"E8.bottom"),sQuery(id+"F0.wireOp",EDGE,"E8.top")])]}),"instanceName":"1"}),"instanceName":"1"});
            var Q151;
            Q151=makeQuery(id+"F10.opPattern","COPY",BODY,{"derivedFrom":makeQuery(id+"F8.opPattern","COPY",BODY,{"derivedFrom":makeQuery(id+"F2.opExtrude","SWEPT_BODY",BODY,{"disambiguationData":[OSD([sQuery(id+"F0.wireOp",EDGE,"E3.right"),sQuery(id+"F0.wireOp",EDGE,"E4.right"),sQuery(id+"F0.wireOp",EDGE,"E8.bottom"),sQuery(id+"F0.wireOp",EDGE,"E8.top")])]}),"instanceName":"1"}),"instanceName":"1"});
            var Q152;
            Q152=makeQuery(id+"F10.opPattern","COPY",BODY,{"derivedFrom":makeQuery(id+"F8.opPattern","COPY",BODY,{"derivedFrom":makeQuery(id+"F2.opExtrude","SWEPT_BODY",BODY,{"disambiguationData":[OSD([sQuery(id+"F0.wireOp",EDGE,"E5.left"),sQuery(id+"F0.wireOp",EDGE,"E6.left"),sQuery(id+"F0.wireOp",EDGE,"E8.bottom"),sQuery(id+"F0.wireOp",EDGE,"E8.top")])]}),"instanceName":"1"}),"instanceName":"1"});
            var Q153;
            Q153=makeQuery(id+"F10.opPattern","COPY",BODY,{"derivedFrom":makeQuery(id+"F8.opPattern","COPY",BODY,{"derivedFrom":makeQuery(id+"F2.opExtrude","SWEPT_BODY",BODY,{"disambiguationData":[OSD([sQuery(id+"F0.wireOp",EDGE,"E5.right"),sQuery(id+"F0.wireOp",EDGE,"E6.right"),sQuery(id+"F0.wireOp",EDGE,"E8.bottom"),sQuery(id+"F0.wireOp",EDGE,"E8.top")])]}),"instanceName":"1"}),"instanceName":"1"});
            var Q154;
            Q154=makeQuery(id+"F10.opPattern","COPY",BODY,{"derivedFrom":makeQuery(id+"F8.opPattern","COPY",BODY,{"derivedFrom":makeQuery(id+"F2.opExtrude","SWEPT_BODY",BODY,{"disambiguationData":[OSD([sQuery(id+"F0.wireOp",EDGE,"E7.left"),sQuery(id+"F0.wireOp",EDGE,"E8.bottom"),sQuery(id+"F0.wireOp",EDGE,"E8.top"),sQuery(id+"F0.wireOp",EDGE,"E8.left")])]}),"instanceName":"1"}),"instanceName":"1"});
            var Q155;
            Q155=makeQuery(id+"F10.opPattern","COPY",BODY,{"derivedFrom":makeQuery(id+"F8.opPattern","COPY",BODY,{"derivedFrom":makeQuery(id+"F2.opExtrude","SWEPT_BODY",BODY,{"disambiguationData":[OSD([sQuery(id+"F0.wireOp",EDGE,"E7.right"),sQuery(id+"F0.wireOp",EDGE,"E8.bottom"),sQuery(id+"F0.wireOp",EDGE,"E8.top"),sQuery(id+"F0.wireOp",EDGE,"E8.right")])]}),"instanceName":"1"}),"instanceName":"1"});
            var Q156;
            Q156=makeQuery(id+"F10.opPattern","COPY",BODY,{"derivedFrom":makeQuery(id+"F8.opPattern","COPY",BODY,{"derivedFrom":makeQuery(id+"F3.opPattern","COPY",BODY,{"derivedFrom":makeQuery(id+"F1.opExtrude","SWEPT_BODY",BODY,{"disambiguationData":[OSD([sQuery(id+"F0.wireOp",EDGE,"E0.bottom"),sQuery(id+"F0.wireOp",EDGE,"E0.top"),sQuery(id+"F0.wireOp",EDGE,"E0.left"),sQuery(id+"F0.wireOp",EDGE,"E8.right")])]}),"instanceName":"1"}),"instanceName":"1"}),"instanceName":"1"});
            var Q157;
            Q157=makeQuery(id+"F10.opPattern","COPY",BODY,{"derivedFrom":makeQuery(id+"F8.opPattern","COPY",BODY,{"derivedFrom":makeQuery(id+"F3.opPattern","COPY",BODY,{"derivedFrom":makeQuery(id+"F1.opExtrude","SWEPT_BODY",BODY,{"disambiguationData":[OSD([sQuery(id+"F0.wireOp",EDGE,"E0.bottom"),sQuery(id+"F0.wireOp",EDGE,"E0.top"),sQuery(id+"F0.wireOp",EDGE,"E0.right"),sQuery(id+"F0.wireOp",EDGE,"E8.left")])]}),"instanceName":"1"}),"instanceName":"1"}),"instanceName":"1"});
            var Q158;
            Q158=makeQuery(id+"F10.opPattern","COPY",BODY,{"derivedFrom":makeQuery(id+"F8.opPattern","COPY",BODY,{"derivedFrom":makeQuery(id+"F3.opPattern","COPY",BODY,{"derivedFrom":makeQuery(id+"F1.opExtrude","SWEPT_BODY",BODY,{"disambiguationData":[OSD([sQuery(id+"F0.wireOp",EDGE,"E1.left"),sQuery(id+"F0.wireOp",EDGE,"E1.right"),sQuery(id+"F0.wireOp",EDGE,"E8.bottom"),sQuery(id+"F0.wireOp",EDGE,"E8.top")])]}),"instanceName":"1"}),"instanceName":"1"}),"instanceName":"1"});
            var Q159;
            Q159=makeQuery(id+"F10.opPattern","COPY",BODY,{"derivedFrom":makeQuery(id+"F8.opPattern","COPY",BODY,{"derivedFrom":makeQuery(id+"F3.opPattern","COPY",BODY,{"derivedFrom":makeQuery(id+"F1.opExtrude","SWEPT_BODY",BODY,{"disambiguationData":[OSD([sQuery(id+"F0.wireOp",EDGE,"E2.left"),sQuery(id+"F0.wireOp",EDGE,"E3.left"),sQuery(id+"F0.wireOp",EDGE,"E8.bottom"),sQuery(id+"F0.wireOp",EDGE,"E8.top")])]}),"instanceName":"1"}),"instanceName":"1"}),"instanceName":"1"});
            var Q160;
            Q160=makeQuery(id+"F10.opPattern","COPY",BODY,{"derivedFrom":makeQuery(id+"F8.opPattern","COPY",BODY,{"derivedFrom":makeQuery(id+"F3.opPattern","COPY",BODY,{"derivedFrom":makeQuery(id+"F1.opExtrude","SWEPT_BODY",BODY,{"disambiguationData":[OSD([sQuery(id+"F0.wireOp",EDGE,"E2.right"),sQuery(id+"F0.wireOp",EDGE,"E3.right"),sQuery(id+"F0.wireOp",EDGE,"E8.bottom"),sQuery(id+"F0.wireOp",EDGE,"E8.top")])]}),"instanceName":"1"}),"instanceName":"1"}),"instanceName":"1"});
            var Q161;
            Q161=makeQuery(id+"F10.opPattern","COPY",BODY,{"derivedFrom":makeQuery(id+"F8.opPattern","COPY",BODY,{"derivedFrom":makeQuery(id+"F3.opPattern","COPY",BODY,{"derivedFrom":makeQuery(id+"F1.opExtrude","SWEPT_BODY",BODY,{"disambiguationData":[OSD([sQuery(id+"F0.wireOp",EDGE,"E4.left"),sQuery(id+"F0.wireOp",EDGE,"E5.left"),sQuery(id+"F0.wireOp",EDGE,"E8.bottom"),sQuery(id+"F0.wireOp",EDGE,"E8.top")])]}),"instanceName":"1"}),"instanceName":"1"}),"instanceName":"1"});
            var Q162;
            Q162=makeQuery(id+"F10.opPattern","COPY",BODY,{"derivedFrom":makeQuery(id+"F8.opPattern","COPY",BODY,{"derivedFrom":makeQuery(id+"F3.opPattern","COPY",BODY,{"derivedFrom":makeQuery(id+"F1.opExtrude","SWEPT_BODY",BODY,{"disambiguationData":[OSD([sQuery(id+"F0.wireOp",EDGE,"E4.right"),sQuery(id+"F0.wireOp",EDGE,"E5.right"),sQuery(id+"F0.wireOp",EDGE,"E8.bottom"),sQuery(id+"F0.wireOp",EDGE,"E8.top")])]}),"instanceName":"1"}),"instanceName":"1"}),"instanceName":"1"});
            var Q163;
            Q163=makeQuery(id+"F10.opPattern","COPY",BODY,{"derivedFrom":makeQuery(id+"F8.opPattern","COPY",BODY,{"derivedFrom":makeQuery(id+"F3.opPattern","COPY",BODY,{"derivedFrom":makeQuery(id+"F1.opExtrude","SWEPT_BODY",BODY,{"disambiguationData":[OSD([sQuery(id+"F0.wireOp",EDGE,"E6.left"),sQuery(id+"F0.wireOp",EDGE,"E7.left"),sQuery(id+"F0.wireOp",EDGE,"E8.bottom"),sQuery(id+"F0.wireOp",EDGE,"E8.top")])]}),"instanceName":"1"}),"instanceName":"1"}),"instanceName":"1"});
            var Q164;
            Q164=makeQuery(id+"F10.opPattern","COPY",BODY,{"derivedFrom":makeQuery(id+"F8.opPattern","COPY",BODY,{"derivedFrom":makeQuery(id+"F3.opPattern","COPY",BODY,{"derivedFrom":makeQuery(id+"F1.opExtrude","SWEPT_BODY",BODY,{"disambiguationData":[OSD([sQuery(id+"F0.wireOp",EDGE,"E6.right"),sQuery(id+"F0.wireOp",EDGE,"E7.right"),sQuery(id+"F0.wireOp",EDGE,"E8.bottom"),sQuery(id+"F0.wireOp",EDGE,"E8.top")])]}),"instanceName":"1"}),"instanceName":"1"}),"instanceName":"1"});
            var Q165;
            Q165=makeQuery(id+"F10.opPattern","COPY",BODY,{"derivedFrom":makeQuery(id+"F8.opPattern","COPY",BODY,{"derivedFrom":makeQuery(id+"F3.opPattern","COPY",BODY,{"derivedFrom":makeQuery(id+"F2.opExtrude","SWEPT_BODY",BODY,{"disambiguationData":[OSD([sQuery(id+"F0.wireOp",EDGE,"E1.left"),sQuery(id+"F0.wireOp",EDGE,"E2.left"),sQuery(id+"F0.wireOp",EDGE,"E8.bottom"),sQuery(id+"F0.wireOp",EDGE,"E8.top")])]}),"instanceName":"1"}),"instanceName":"1"}),"instanceName":"1"});
            var Q166;
            Q166=makeQuery(id+"F10.opPattern","COPY",BODY,{"derivedFrom":makeQuery(id+"F8.opPattern","COPY",BODY,{"derivedFrom":makeQuery(id+"F3.opPattern","COPY",BODY,{"derivedFrom":makeQuery(id+"F2.opExtrude","SWEPT_BODY",BODY,{"disambiguationData":[OSD([sQuery(id+"F0.wireOp",EDGE,"E1.right"),sQuery(id+"F0.wireOp",EDGE,"E2.right"),sQuery(id+"F0.wireOp",EDGE,"E8.bottom"),sQuery(id+"F0.wireOp",EDGE,"E8.top")])]}),"instanceName":"1"}),"instanceName":"1"}),"instanceName":"1"});
            var Q167;
            Q167=makeQuery(id+"F10.opPattern","COPY",BODY,{"derivedFrom":makeQuery(id+"F8.opPattern","COPY",BODY,{"derivedFrom":makeQuery(id+"F3.opPattern","COPY",BODY,{"derivedFrom":makeQuery(id+"F2.opExtrude","SWEPT_BODY",BODY,{"disambiguationData":[OSD([sQuery(id+"F0.wireOp",EDGE,"E3.left"),sQuery(id+"F0.wireOp",EDGE,"E4.left"),sQuery(id+"F0.wireOp",EDGE,"E8.bottom"),sQuery(id+"F0.wireOp",EDGE,"E8.top")])]}),"instanceName":"1"}),"instanceName":"1"}),"instanceName":"1"});
            var Q168;
            Q168=makeQuery(id+"F10.opPattern","COPY",BODY,{"derivedFrom":makeQuery(id+"F8.opPattern","COPY",BODY,{"derivedFrom":makeQuery(id+"F3.opPattern","COPY",BODY,{"derivedFrom":makeQuery(id+"F2.opExtrude","SWEPT_BODY",BODY,{"disambiguationData":[OSD([sQuery(id+"F0.wireOp",EDGE,"E3.right"),sQuery(id+"F0.wireOp",EDGE,"E4.right"),sQuery(id+"F0.wireOp",EDGE,"E8.bottom"),sQuery(id+"F0.wireOp",EDGE,"E8.top")])]}),"instanceName":"1"}),"instanceName":"1"}),"instanceName":"1"});
            var Q169;
            Q169=makeQuery(id+"F10.opPattern","COPY",BODY,{"derivedFrom":makeQuery(id+"F8.opPattern","COPY",BODY,{"derivedFrom":makeQuery(id+"F3.opPattern","COPY",BODY,{"derivedFrom":makeQuery(id+"F2.opExtrude","SWEPT_BODY",BODY,{"disambiguationData":[OSD([sQuery(id+"F0.wireOp",EDGE,"E5.left"),sQuery(id+"F0.wireOp",EDGE,"E6.left"),sQuery(id+"F0.wireOp",EDGE,"E8.bottom"),sQuery(id+"F0.wireOp",EDGE,"E8.top")])]}),"instanceName":"1"}),"instanceName":"1"}),"instanceName":"1"});
            var Q170;
            Q170=makeQuery(id+"F10.opPattern","COPY",BODY,{"derivedFrom":makeQuery(id+"F8.opPattern","COPY",BODY,{"derivedFrom":makeQuery(id+"F3.opPattern","COPY",BODY,{"derivedFrom":makeQuery(id+"F2.opExtrude","SWEPT_BODY",BODY,{"disambiguationData":[OSD([sQuery(id+"F0.wireOp",EDGE,"E5.right"),sQuery(id+"F0.wireOp",EDGE,"E6.right"),sQuery(id+"F0.wireOp",EDGE,"E8.bottom"),sQuery(id+"F0.wireOp",EDGE,"E8.top")])]}),"instanceName":"1"}),"instanceName":"1"}),"instanceName":"1"});
            var Q171;
            Q171=makeQuery(id+"F10.opPattern","COPY",BODY,{"derivedFrom":makeQuery(id+"F8.opPattern","COPY",BODY,{"derivedFrom":makeQuery(id+"F3.opPattern","COPY",BODY,{"derivedFrom":makeQuery(id+"F2.opExtrude","SWEPT_BODY",BODY,{"disambiguationData":[OSD([sQuery(id+"F0.wireOp",EDGE,"E7.left"),sQuery(id+"F0.wireOp",EDGE,"E8.bottom"),sQuery(id+"F0.wireOp",EDGE,"E8.top"),sQuery(id+"F0.wireOp",EDGE,"E8.left")])]}),"instanceName":"1"}),"instanceName":"1"}),"instanceName":"1"});
            var Q172;
            Q172=makeQuery(id+"F10.opPattern","COPY",BODY,{"derivedFrom":makeQuery(id+"F8.opPattern","COPY",BODY,{"derivedFrom":makeQuery(id+"F3.opPattern","COPY",BODY,{"derivedFrom":makeQuery(id+"F2.opExtrude","SWEPT_BODY",BODY,{"disambiguationData":[OSD([sQuery(id+"F0.wireOp",EDGE,"E7.right"),sQuery(id+"F0.wireOp",EDGE,"E8.bottom"),sQuery(id+"F0.wireOp",EDGE,"E8.top"),sQuery(id+"F0.wireOp",EDGE,"E8.right")])]}),"instanceName":"1"}),"instanceName":"1"}),"instanceName":"1"});
            var Q173;
            Q173=makeQuery(id+"F10.opPattern","COPY",BODY,{"derivedFrom":makeQuery(id+"F8.opPattern","COPY",BODY,{"derivedFrom":makeQuery(id+"F6.opPattern","COPY",BODY,{"derivedFrom":makeQuery(id+"F1.opExtrude","SWEPT_BODY",BODY,{"disambiguationData":[OSD([sQuery(id+"F0.wireOp",EDGE,"E0.bottom"),sQuery(id+"F0.wireOp",EDGE,"E0.top"),sQuery(id+"F0.wireOp",EDGE,"E0.left"),sQuery(id+"F0.wireOp",EDGE,"E8.right")])]}),"instanceName":"1"}),"instanceName":"1"}),"instanceName":"1"});
            var Q174;
            Q174=makeQuery(id+"F10.opPattern","COPY",BODY,{"derivedFrom":makeQuery(id+"F8.opPattern","COPY",BODY,{"derivedFrom":makeQuery(id+"F6.opPattern","COPY",BODY,{"derivedFrom":makeQuery(id+"F1.opExtrude","SWEPT_BODY",BODY,{"disambiguationData":[OSD([sQuery(id+"F0.wireOp",EDGE,"E0.bottom"),sQuery(id+"F0.wireOp",EDGE,"E0.top"),sQuery(id+"F0.wireOp",EDGE,"E0.right"),sQuery(id+"F0.wireOp",EDGE,"E8.left")])]}),"instanceName":"1"}),"instanceName":"1"}),"instanceName":"1"});
            var Q175;
            Q175=makeQuery(id+"F10.opPattern","COPY",BODY,{"derivedFrom":makeQuery(id+"F8.opPattern","COPY",BODY,{"derivedFrom":makeQuery(id+"F6.opPattern","COPY",BODY,{"derivedFrom":makeQuery(id+"F1.opExtrude","SWEPT_BODY",BODY,{"disambiguationData":[OSD([sQuery(id+"F0.wireOp",EDGE,"E1.left"),sQuery(id+"F0.wireOp",EDGE,"E1.right"),sQuery(id+"F0.wireOp",EDGE,"E8.bottom"),sQuery(id+"F0.wireOp",EDGE,"E8.top")])]}),"instanceName":"1"}),"instanceName":"1"}),"instanceName":"1"});
            var Q176;
            Q176=makeQuery(id+"F10.opPattern","COPY",BODY,{"derivedFrom":makeQuery(id+"F8.opPattern","COPY",BODY,{"derivedFrom":makeQuery(id+"F6.opPattern","COPY",BODY,{"derivedFrom":makeQuery(id+"F1.opExtrude","SWEPT_BODY",BODY,{"disambiguationData":[OSD([sQuery(id+"F0.wireOp",EDGE,"E2.left"),sQuery(id+"F0.wireOp",EDGE,"E3.left"),sQuery(id+"F0.wireOp",EDGE,"E8.bottom"),sQuery(id+"F0.wireOp",EDGE,"E8.top")])]}),"instanceName":"1"}),"instanceName":"1"}),"instanceName":"1"});
            var Q177;
            Q177=makeQuery(id+"F10.opPattern","COPY",BODY,{"derivedFrom":makeQuery(id+"F8.opPattern","COPY",BODY,{"derivedFrom":makeQuery(id+"F6.opPattern","COPY",BODY,{"derivedFrom":makeQuery(id+"F1.opExtrude","SWEPT_BODY",BODY,{"disambiguationData":[OSD([sQuery(id+"F0.wireOp",EDGE,"E2.right"),sQuery(id+"F0.wireOp",EDGE,"E3.right"),sQuery(id+"F0.wireOp",EDGE,"E8.bottom"),sQuery(id+"F0.wireOp",EDGE,"E8.top")])]}),"instanceName":"1"}),"instanceName":"1"}),"instanceName":"1"});
            var Q178;
            Q178=makeQuery(id+"F10.opPattern","COPY",BODY,{"derivedFrom":makeQuery(id+"F8.opPattern","COPY",BODY,{"derivedFrom":makeQuery(id+"F6.opPattern","COPY",BODY,{"derivedFrom":makeQuery(id+"F1.opExtrude","SWEPT_BODY",BODY,{"disambiguationData":[OSD([sQuery(id+"F0.wireOp",EDGE,"E4.left"),sQuery(id+"F0.wireOp",EDGE,"E5.left"),sQuery(id+"F0.wireOp",EDGE,"E8.bottom"),sQuery(id+"F0.wireOp",EDGE,"E8.top")])]}),"instanceName":"1"}),"instanceName":"1"}),"instanceName":"1"});
            var Q179;
            Q179=makeQuery(id+"F10.opPattern","COPY",BODY,{"derivedFrom":makeQuery(id+"F8.opPattern","COPY",BODY,{"derivedFrom":makeQuery(id+"F6.opPattern","COPY",BODY,{"derivedFrom":makeQuery(id+"F1.opExtrude","SWEPT_BODY",BODY,{"disambiguationData":[OSD([sQuery(id+"F0.wireOp",EDGE,"E4.right"),sQuery(id+"F0.wireOp",EDGE,"E5.right"),sQuery(id+"F0.wireOp",EDGE,"E8.bottom"),sQuery(id+"F0.wireOp",EDGE,"E8.top")])]}),"instanceName":"1"}),"instanceName":"1"}),"instanceName":"1"});
            var Q180;
            Q180=makeQuery(id+"F10.opPattern","COPY",BODY,{"derivedFrom":makeQuery(id+"F8.opPattern","COPY",BODY,{"derivedFrom":makeQuery(id+"F6.opPattern","COPY",BODY,{"derivedFrom":makeQuery(id+"F1.opExtrude","SWEPT_BODY",BODY,{"disambiguationData":[OSD([sQuery(id+"F0.wireOp",EDGE,"E6.left"),sQuery(id+"F0.wireOp",EDGE,"E7.left"),sQuery(id+"F0.wireOp",EDGE,"E8.bottom"),sQuery(id+"F0.wireOp",EDGE,"E8.top")])]}),"instanceName":"1"}),"instanceName":"1"}),"instanceName":"1"});
            var Q181;
            Q181=makeQuery(id+"F10.opPattern","COPY",BODY,{"derivedFrom":makeQuery(id+"F8.opPattern","COPY",BODY,{"derivedFrom":makeQuery(id+"F6.opPattern","COPY",BODY,{"derivedFrom":makeQuery(id+"F1.opExtrude","SWEPT_BODY",BODY,{"disambiguationData":[OSD([sQuery(id+"F0.wireOp",EDGE,"E6.right"),sQuery(id+"F0.wireOp",EDGE,"E7.right"),sQuery(id+"F0.wireOp",EDGE,"E8.bottom"),sQuery(id+"F0.wireOp",EDGE,"E8.top")])]}),"instanceName":"1"}),"instanceName":"1"}),"instanceName":"1"});
            var Q182;
            Q182=makeQuery(id+"F10.opPattern","COPY",BODY,{"derivedFrom":makeQuery(id+"F8.opPattern","COPY",BODY,{"derivedFrom":makeQuery(id+"F6.opPattern","COPY",BODY,{"derivedFrom":makeQuery(id+"F2.opExtrude","SWEPT_BODY",BODY,{"disambiguationData":[OSD([sQuery(id+"F0.wireOp",EDGE,"E1.left"),sQuery(id+"F0.wireOp",EDGE,"E2.left"),sQuery(id+"F0.wireOp",EDGE,"E8.bottom"),sQuery(id+"F0.wireOp",EDGE,"E8.top")])]}),"instanceName":"1"}),"instanceName":"1"}),"instanceName":"1"});
            var Q183;
            Q183=makeQuery(id+"F10.opPattern","COPY",BODY,{"derivedFrom":makeQuery(id+"F8.opPattern","COPY",BODY,{"derivedFrom":makeQuery(id+"F6.opPattern","COPY",BODY,{"derivedFrom":makeQuery(id+"F2.opExtrude","SWEPT_BODY",BODY,{"disambiguationData":[OSD([sQuery(id+"F0.wireOp",EDGE,"E1.right"),sQuery(id+"F0.wireOp",EDGE,"E2.right"),sQuery(id+"F0.wireOp",EDGE,"E8.bottom"),sQuery(id+"F0.wireOp",EDGE,"E8.top")])]}),"instanceName":"1"}),"instanceName":"1"}),"instanceName":"1"});
            var Q184;
            Q184=makeQuery(id+"F10.opPattern","COPY",BODY,{"derivedFrom":makeQuery(id+"F8.opPattern","COPY",BODY,{"derivedFrom":makeQuery(id+"F6.opPattern","COPY",BODY,{"derivedFrom":makeQuery(id+"F2.opExtrude","SWEPT_BODY",BODY,{"disambiguationData":[OSD([sQuery(id+"F0.wireOp",EDGE,"E3.left"),sQuery(id+"F0.wireOp",EDGE,"E4.left"),sQuery(id+"F0.wireOp",EDGE,"E8.bottom"),sQuery(id+"F0.wireOp",EDGE,"E8.top")])]}),"instanceName":"1"}),"instanceName":"1"}),"instanceName":"1"});
            var Q185;
            Q185=makeQuery(id+"F10.opPattern","COPY",BODY,{"derivedFrom":makeQuery(id+"F8.opPattern","COPY",BODY,{"derivedFrom":makeQuery(id+"F6.opPattern","COPY",BODY,{"derivedFrom":makeQuery(id+"F2.opExtrude","SWEPT_BODY",BODY,{"disambiguationData":[OSD([sQuery(id+"F0.wireOp",EDGE,"E3.right"),sQuery(id+"F0.wireOp",EDGE,"E4.right"),sQuery(id+"F0.wireOp",EDGE,"E8.bottom"),sQuery(id+"F0.wireOp",EDGE,"E8.top")])]}),"instanceName":"1"}),"instanceName":"1"}),"instanceName":"1"});
            var Q186;
            Q186=makeQuery(id+"F10.opPattern","COPY",BODY,{"derivedFrom":makeQuery(id+"F8.opPattern","COPY",BODY,{"derivedFrom":makeQuery(id+"F6.opPattern","COPY",BODY,{"derivedFrom":makeQuery(id+"F2.opExtrude","SWEPT_BODY",BODY,{"disambiguationData":[OSD([sQuery(id+"F0.wireOp",EDGE,"E5.left"),sQuery(id+"F0.wireOp",EDGE,"E6.left"),sQuery(id+"F0.wireOp",EDGE,"E8.bottom"),sQuery(id+"F0.wireOp",EDGE,"E8.top")])]}),"instanceName":"1"}),"instanceName":"1"}),"instanceName":"1"});
            var Q187;
            Q187=makeQuery(id+"F10.opPattern","COPY",BODY,{"derivedFrom":makeQuery(id+"F8.opPattern","COPY",BODY,{"derivedFrom":makeQuery(id+"F6.opPattern","COPY",BODY,{"derivedFrom":makeQuery(id+"F2.opExtrude","SWEPT_BODY",BODY,{"disambiguationData":[OSD([sQuery(id+"F0.wireOp",EDGE,"E5.right"),sQuery(id+"F0.wireOp",EDGE,"E6.right"),sQuery(id+"F0.wireOp",EDGE,"E8.bottom"),sQuery(id+"F0.wireOp",EDGE,"E8.top")])]}),"instanceName":"1"}),"instanceName":"1"}),"instanceName":"1"});
            var Q188;
            Q188=makeQuery(id+"F10.opPattern","COPY",BODY,{"derivedFrom":makeQuery(id+"F8.opPattern","COPY",BODY,{"derivedFrom":makeQuery(id+"F6.opPattern","COPY",BODY,{"derivedFrom":makeQuery(id+"F2.opExtrude","SWEPT_BODY",BODY,{"disambiguationData":[OSD([sQuery(id+"F0.wireOp",EDGE,"E7.left"),sQuery(id+"F0.wireOp",EDGE,"E8.bottom"),sQuery(id+"F0.wireOp",EDGE,"E8.top"),sQuery(id+"F0.wireOp",EDGE,"E8.left")])]}),"instanceName":"1"}),"instanceName":"1"}),"instanceName":"1"});
            var Q189;
            Q189=makeQuery(id+"F10.opPattern","COPY",BODY,{"derivedFrom":makeQuery(id+"F8.opPattern","COPY",BODY,{"derivedFrom":makeQuery(id+"F6.opPattern","COPY",BODY,{"derivedFrom":makeQuery(id+"F2.opExtrude","SWEPT_BODY",BODY,{"disambiguationData":[OSD([sQuery(id+"F0.wireOp",EDGE,"E7.right"),sQuery(id+"F0.wireOp",EDGE,"E8.bottom"),sQuery(id+"F0.wireOp",EDGE,"E8.top"),sQuery(id+"F0.wireOp",EDGE,"E8.right")])]}),"instanceName":"1"}),"instanceName":"1"}),"instanceName":"1"});
            var Q190;
            Q190=makeQuery(id+"F10.opPattern","COPY",BODY,{"derivedFrom":makeQuery(id+"F8.opPattern","COPY",BODY,{"derivedFrom":makeQuery(id+"F6.opPattern","COPY",BODY,{"derivedFrom":makeQuery(id+"F3.opPattern","COPY",BODY,{"derivedFrom":makeQuery(id+"F1.opExtrude","SWEPT_BODY",BODY,{"disambiguationData":[OSD([sQuery(id+"F0.wireOp",EDGE,"E0.bottom"),sQuery(id+"F0.wireOp",EDGE,"E0.top"),sQuery(id+"F0.wireOp",EDGE,"E0.left"),sQuery(id+"F0.wireOp",EDGE,"E8.right")])]}),"instanceName":"1"}),"instanceName":"1"}),"instanceName":"1"}),"instanceName":"1"});
            var Q191;
            Q191=makeQuery(id+"F10.opPattern","COPY",BODY,{"derivedFrom":makeQuery(id+"F8.opPattern","COPY",BODY,{"derivedFrom":makeQuery(id+"F6.opPattern","COPY",BODY,{"derivedFrom":makeQuery(id+"F3.opPattern","COPY",BODY,{"derivedFrom":makeQuery(id+"F1.opExtrude","SWEPT_BODY",BODY,{"disambiguationData":[OSD([sQuery(id+"F0.wireOp",EDGE,"E0.bottom"),sQuery(id+"F0.wireOp",EDGE,"E0.top"),sQuery(id+"F0.wireOp",EDGE,"E0.right"),sQuery(id+"F0.wireOp",EDGE,"E8.left")])]}),"instanceName":"1"}),"instanceName":"1"}),"instanceName":"1"}),"instanceName":"1"});
            var Q192;
            Q192=makeQuery(id+"F10.opPattern","COPY",BODY,{"derivedFrom":makeQuery(id+"F8.opPattern","COPY",BODY,{"derivedFrom":makeQuery(id+"F6.opPattern","COPY",BODY,{"derivedFrom":makeQuery(id+"F3.opPattern","COPY",BODY,{"derivedFrom":makeQuery(id+"F1.opExtrude","SWEPT_BODY",BODY,{"disambiguationData":[OSD([sQuery(id+"F0.wireOp",EDGE,"E1.left"),sQuery(id+"F0.wireOp",EDGE,"E1.right"),sQuery(id+"F0.wireOp",EDGE,"E8.bottom"),sQuery(id+"F0.wireOp",EDGE,"E8.top")])]}),"instanceName":"1"}),"instanceName":"1"}),"instanceName":"1"}),"instanceName":"1"});
            var Q193;
            Q193=makeQuery(id+"F10.opPattern","COPY",BODY,{"derivedFrom":makeQuery(id+"F8.opPattern","COPY",BODY,{"derivedFrom":makeQuery(id+"F6.opPattern","COPY",BODY,{"derivedFrom":makeQuery(id+"F3.opPattern","COPY",BODY,{"derivedFrom":makeQuery(id+"F1.opExtrude","SWEPT_BODY",BODY,{"disambiguationData":[OSD([sQuery(id+"F0.wireOp",EDGE,"E2.left"),sQuery(id+"F0.wireOp",EDGE,"E3.left"),sQuery(id+"F0.wireOp",EDGE,"E8.bottom"),sQuery(id+"F0.wireOp",EDGE,"E8.top")])]}),"instanceName":"1"}),"instanceName":"1"}),"instanceName":"1"}),"instanceName":"1"});
            var Q194;
            Q194=makeQuery(id+"F10.opPattern","COPY",BODY,{"derivedFrom":makeQuery(id+"F8.opPattern","COPY",BODY,{"derivedFrom":makeQuery(id+"F6.opPattern","COPY",BODY,{"derivedFrom":makeQuery(id+"F3.opPattern","COPY",BODY,{"derivedFrom":makeQuery(id+"F1.opExtrude","SWEPT_BODY",BODY,{"disambiguationData":[OSD([sQuery(id+"F0.wireOp",EDGE,"E2.right"),sQuery(id+"F0.wireOp",EDGE,"E3.right"),sQuery(id+"F0.wireOp",EDGE,"E8.bottom"),sQuery(id+"F0.wireOp",EDGE,"E8.top")])]}),"instanceName":"1"}),"instanceName":"1"}),"instanceName":"1"}),"instanceName":"1"});
            var Q195;
            Q195=makeQuery(id+"F10.opPattern","COPY",BODY,{"derivedFrom":makeQuery(id+"F8.opPattern","COPY",BODY,{"derivedFrom":makeQuery(id+"F6.opPattern","COPY",BODY,{"derivedFrom":makeQuery(id+"F3.opPattern","COPY",BODY,{"derivedFrom":makeQuery(id+"F1.opExtrude","SWEPT_BODY",BODY,{"disambiguationData":[OSD([sQuery(id+"F0.wireOp",EDGE,"E4.left"),sQuery(id+"F0.wireOp",EDGE,"E5.left"),sQuery(id+"F0.wireOp",EDGE,"E8.bottom"),sQuery(id+"F0.wireOp",EDGE,"E8.top")])]}),"instanceName":"1"}),"instanceName":"1"}),"instanceName":"1"}),"instanceName":"1"});
            var Q196;
            Q196=makeQuery(id+"F10.opPattern","COPY",BODY,{"derivedFrom":makeQuery(id+"F8.opPattern","COPY",BODY,{"derivedFrom":makeQuery(id+"F6.opPattern","COPY",BODY,{"derivedFrom":makeQuery(id+"F3.opPattern","COPY",BODY,{"derivedFrom":makeQuery(id+"F1.opExtrude","SWEPT_BODY",BODY,{"disambiguationData":[OSD([sQuery(id+"F0.wireOp",EDGE,"E4.right"),sQuery(id+"F0.wireOp",EDGE,"E5.right"),sQuery(id+"F0.wireOp",EDGE,"E8.bottom"),sQuery(id+"F0.wireOp",EDGE,"E8.top")])]}),"instanceName":"1"}),"instanceName":"1"}),"instanceName":"1"}),"instanceName":"1"});
            var Q197;
            Q197=makeQuery(id+"F10.opPattern","COPY",BODY,{"derivedFrom":makeQuery(id+"F8.opPattern","COPY",BODY,{"derivedFrom":makeQuery(id+"F6.opPattern","COPY",BODY,{"derivedFrom":makeQuery(id+"F3.opPattern","COPY",BODY,{"derivedFrom":makeQuery(id+"F1.opExtrude","SWEPT_BODY",BODY,{"disambiguationData":[OSD([sQuery(id+"F0.wireOp",EDGE,"E6.left"),sQuery(id+"F0.wireOp",EDGE,"E7.left"),sQuery(id+"F0.wireOp",EDGE,"E8.bottom"),sQuery(id+"F0.wireOp",EDGE,"E8.top")])]}),"instanceName":"1"}),"instanceName":"1"}),"instanceName":"1"}),"instanceName":"1"});
            var Q198;
            Q198=makeQuery(id+"F10.opPattern","COPY",BODY,{"derivedFrom":makeQuery(id+"F8.opPattern","COPY",BODY,{"derivedFrom":makeQuery(id+"F6.opPattern","COPY",BODY,{"derivedFrom":makeQuery(id+"F3.opPattern","COPY",BODY,{"derivedFrom":makeQuery(id+"F1.opExtrude","SWEPT_BODY",BODY,{"disambiguationData":[OSD([sQuery(id+"F0.wireOp",EDGE,"E6.right"),sQuery(id+"F0.wireOp",EDGE,"E7.right"),sQuery(id+"F0.wireOp",EDGE,"E8.bottom"),sQuery(id+"F0.wireOp",EDGE,"E8.top")])]}),"instanceName":"1"}),"instanceName":"1"}),"instanceName":"1"}),"instanceName":"1"});
            var Q199;
            Q199=makeQuery(id+"F10.opPattern","COPY",BODY,{"derivedFrom":makeQuery(id+"F8.opPattern","COPY",BODY,{"derivedFrom":makeQuery(id+"F6.opPattern","COPY",BODY,{"derivedFrom":makeQuery(id+"F3.opPattern","COPY",BODY,{"derivedFrom":makeQuery(id+"F2.opExtrude","SWEPT_BODY",BODY,{"disambiguationData":[OSD([sQuery(id+"F0.wireOp",EDGE,"E1.left"),sQuery(id+"F0.wireOp",EDGE,"E2.left"),sQuery(id+"F0.wireOp",EDGE,"E8.bottom"),sQuery(id+"F0.wireOp",EDGE,"E8.top")])]}),"instanceName":"1"}),"instanceName":"1"}),"instanceName":"1"}),"instanceName":"1"});
            var Q200;
            Q200=makeQuery(id+"F10.opPattern","COPY",BODY,{"derivedFrom":makeQuery(id+"F8.opPattern","COPY",BODY,{"derivedFrom":makeQuery(id+"F6.opPattern","COPY",BODY,{"derivedFrom":makeQuery(id+"F3.opPattern","COPY",BODY,{"derivedFrom":makeQuery(id+"F2.opExtrude","SWEPT_BODY",BODY,{"disambiguationData":[OSD([sQuery(id+"F0.wireOp",EDGE,"E1.right"),sQuery(id+"F0.wireOp",EDGE,"E2.right"),sQuery(id+"F0.wireOp",EDGE,"E8.bottom"),sQuery(id+"F0.wireOp",EDGE,"E8.top")])]}),"instanceName":"1"}),"instanceName":"1"}),"instanceName":"1"}),"instanceName":"1"});
            var Q201;
            Q201=makeQuery(id+"F10.opPattern","COPY",BODY,{"derivedFrom":makeQuery(id+"F8.opPattern","COPY",BODY,{"derivedFrom":makeQuery(id+"F6.opPattern","COPY",BODY,{"derivedFrom":makeQuery(id+"F3.opPattern","COPY",BODY,{"derivedFrom":makeQuery(id+"F2.opExtrude","SWEPT_BODY",BODY,{"disambiguationData":[OSD([sQuery(id+"F0.wireOp",EDGE,"E3.left"),sQuery(id+"F0.wireOp",EDGE,"E4.left"),sQuery(id+"F0.wireOp",EDGE,"E8.bottom"),sQuery(id+"F0.wireOp",EDGE,"E8.top")])]}),"instanceName":"1"}),"instanceName":"1"}),"instanceName":"1"}),"instanceName":"1"});
            var Q202;
            Q202=makeQuery(id+"F10.opPattern","COPY",BODY,{"derivedFrom":makeQuery(id+"F8.opPattern","COPY",BODY,{"derivedFrom":makeQuery(id+"F6.opPattern","COPY",BODY,{"derivedFrom":makeQuery(id+"F3.opPattern","COPY",BODY,{"derivedFrom":makeQuery(id+"F2.opExtrude","SWEPT_BODY",BODY,{"disambiguationData":[OSD([sQuery(id+"F0.wireOp",EDGE,"E3.right"),sQuery(id+"F0.wireOp",EDGE,"E4.right"),sQuery(id+"F0.wireOp",EDGE,"E8.bottom"),sQuery(id+"F0.wireOp",EDGE,"E8.top")])]}),"instanceName":"1"}),"instanceName":"1"}),"instanceName":"1"}),"instanceName":"1"});
            var Q203;
            Q203=makeQuery(id+"F10.opPattern","COPY",BODY,{"derivedFrom":makeQuery(id+"F8.opPattern","COPY",BODY,{"derivedFrom":makeQuery(id+"F6.opPattern","COPY",BODY,{"derivedFrom":makeQuery(id+"F3.opPattern","COPY",BODY,{"derivedFrom":makeQuery(id+"F2.opExtrude","SWEPT_BODY",BODY,{"disambiguationData":[OSD([sQuery(id+"F0.wireOp",EDGE,"E5.left"),sQuery(id+"F0.wireOp",EDGE,"E6.left"),sQuery(id+"F0.wireOp",EDGE,"E8.bottom"),sQuery(id+"F0.wireOp",EDGE,"E8.top")])]}),"instanceName":"1"}),"instanceName":"1"}),"instanceName":"1"}),"instanceName":"1"});
            var Q204;
            Q204=makeQuery(id+"F10.opPattern","COPY",BODY,{"derivedFrom":makeQuery(id+"F8.opPattern","COPY",BODY,{"derivedFrom":makeQuery(id+"F6.opPattern","COPY",BODY,{"derivedFrom":makeQuery(id+"F3.opPattern","COPY",BODY,{"derivedFrom":makeQuery(id+"F2.opExtrude","SWEPT_BODY",BODY,{"disambiguationData":[OSD([sQuery(id+"F0.wireOp",EDGE,"E5.right"),sQuery(id+"F0.wireOp",EDGE,"E6.right"),sQuery(id+"F0.wireOp",EDGE,"E8.bottom"),sQuery(id+"F0.wireOp",EDGE,"E8.top")])]}),"instanceName":"1"}),"instanceName":"1"}),"instanceName":"1"}),"instanceName":"1"});
            var Q205;
            Q205=makeQuery(id+"F10.opPattern","COPY",BODY,{"derivedFrom":makeQuery(id+"F8.opPattern","COPY",BODY,{"derivedFrom":makeQuery(id+"F6.opPattern","COPY",BODY,{"derivedFrom":makeQuery(id+"F3.opPattern","COPY",BODY,{"derivedFrom":makeQuery(id+"F2.opExtrude","SWEPT_BODY",BODY,{"disambiguationData":[OSD([sQuery(id+"F0.wireOp",EDGE,"E7.left"),sQuery(id+"F0.wireOp",EDGE,"E8.bottom"),sQuery(id+"F0.wireOp",EDGE,"E8.top"),sQuery(id+"F0.wireOp",EDGE,"E8.left")])]}),"instanceName":"1"}),"instanceName":"1"}),"instanceName":"1"}),"instanceName":"1"});
            booleanBodies(context, id + "F17", {"operationType" : BooleanOperationType.SUBTRACTION, "tools" : qUnion([Q0, Q1]), "targets" : qUnion([Q2, Q3, Q4, Q5, Q6, Q7, Q8, Q9, Q10, Q11, Q12, Q13, Q14, Q15, Q16, Q17, Q18, Q19, Q20, Q21, Q22, Q23, Q24, Q25, Q26, Q27, Q28, Q29, Q30, Q31, Q32, Q33, Q34, Q35, Q36, Q37, Q38, Q39, Q40, Q41, Q42, Q43, Q44, Q45, Q46, Q47, Q48, Q49, Q50, Q51, Q52, Q53, Q54, Q55, Q56, Q57, Q58, Q59, Q60, Q61, Q62, Q63, Q64, Q65, Q66, Q67, Q68, Q69, Q70, Q71, Q72, Q73, Q74, Q75, Q76, Q77, Q78, Q79, Q80, Q81, Q82, Q83, Q84, Q85, Q86, Q87, Q88, Q89, Q90, Q91, Q92, Q93, Q94, Q95, Q96, Q97, Q98, Q99, Q100, Q101, Q102, Q103, Q104, Q105, Q106, Q107, Q108, Q109, Q110, Q111, Q112, Q113, Q114, Q115, Q116, Q117, Q118, Q119, Q120, Q121, Q122, Q123, Q124, Q125, Q126, Q127, Q128, Q129, Q130, Q131, Q132, Q133, Q134, Q135, Q136, Q137, Q138, Q139, Q140, Q141, Q142, Q143, Q144, Q145, Q146, Q147, Q148, Q149, Q150, Q151, Q152, Q153, Q154, Q155, Q156, Q157, Q158, Q159, Q160, Q161, Q162, Q163, Q164, Q165, Q166, Q167, Q168, Q169, Q170, Q171, Q172, Q173, Q174, Q175, Q176, Q177, Q178, Q179, Q180, Q181, Q182, Q183, Q184, Q185, Q186, Q187, Q188, Q189, Q190, Q191, Q192, Q193, Q194, Q195, Q196, Q197, Q198, Q199, Q200, Q201, Q202, Q203, Q204, Q205])});
        }
    });
